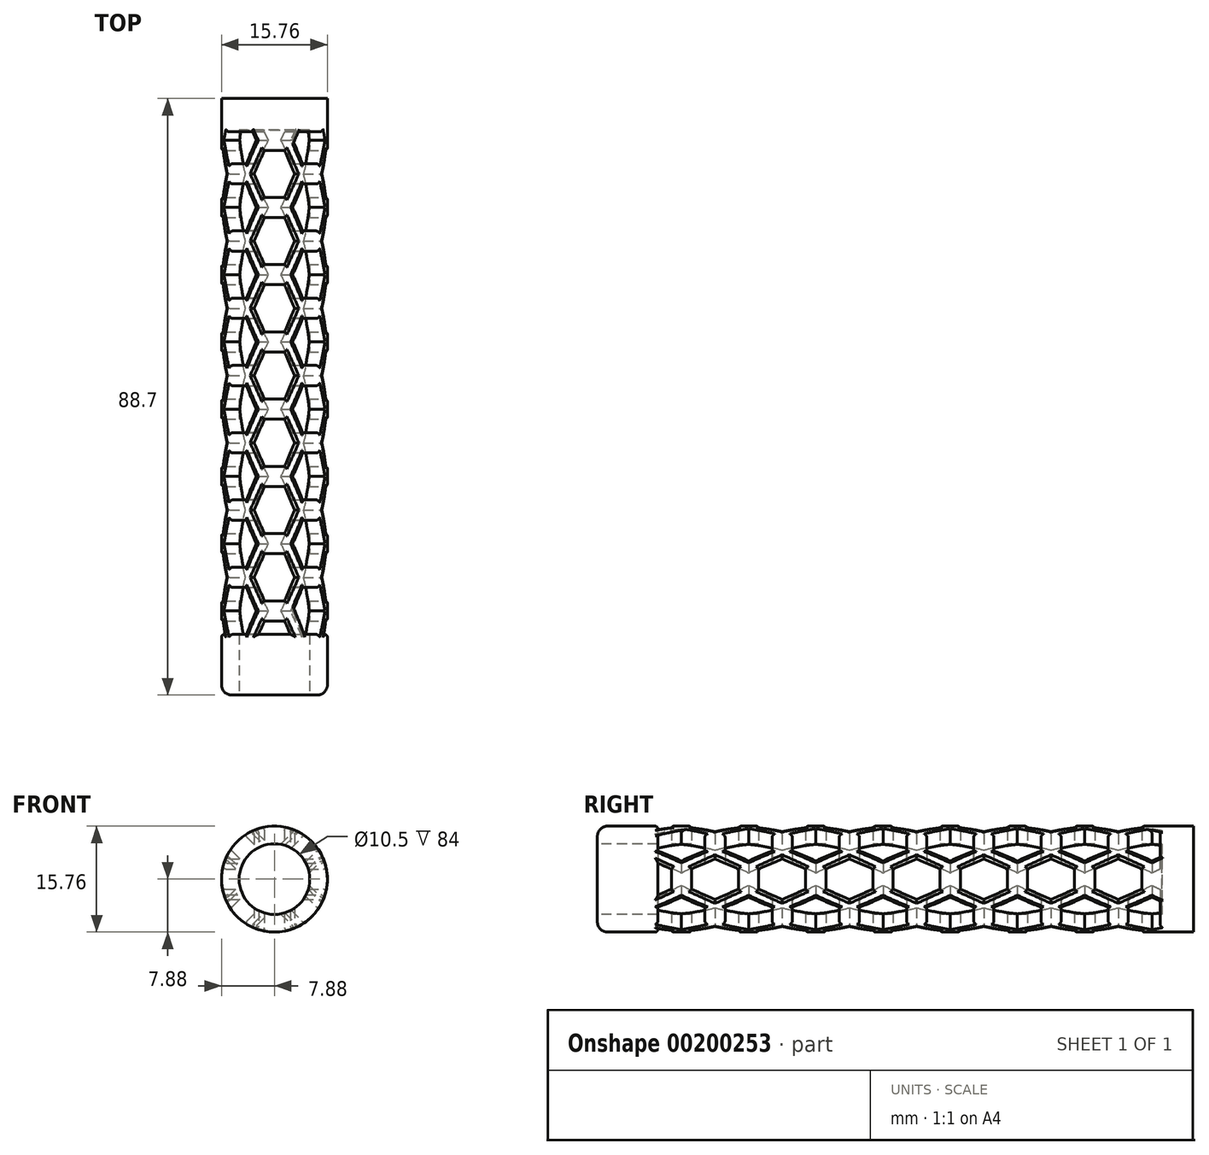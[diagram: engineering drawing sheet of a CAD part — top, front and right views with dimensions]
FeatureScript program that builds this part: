
annotation { "Feature Type Name" : "Feature", "Feature Type Description" : "" }
export const myFeature = defineFeature(function(context is Context, id is Id, definition is map)
    precondition{}
    {
        {
            var Q0;
            Q0=qCreatedBy(makeId("Front.planeOp"),FACE);
            var sketch = newSketch(context, id + "F0", { "sketchPlane" : qUnion([Q0])});
            skCircle(sketch, "E0", {"center": v(0, 0) * mm, "radius": 7.88 * mm});
            skSolve(sketch);
        }
        {
            var Q0;
            Q0=makeQuery(id+"F0.imprint","IMPRINT",FACE,{"disambiguationData":[TD([[makeQuery(id+"F0.imprint","IMPRINT",EDGE,{"derivedFrom":sQuery(id+"F0.wireOp",EDGE,"E0")}),1.0]])]});
            extrude(context, id + "F1", {"entities" : qUnion([Q0]), "oppositeDirection" : true, "depth" : 88.7 * mm});
        }
        {
            var Q0;
            Q0=makeQuery(id+"F1.opExtrude","CAP_FACE",FACE,{"disambiguationData":[OSD([sQuery(id+"F0.wireOp",EDGE,"E0")])],"isStart":true});
            var sketch = newSketch(context, id + "F2", { "sketchPlane" : qUnion([Q0])});
            skCircle(sketch, "E1", {"center": v(0, 0) * mm, "radius": 5.25 * mm});
            skSolve(sketch);
        }
        {
            var Q0;
            Q0=qSketchRegion(id+"F2",true);
            extrude(context, id + "F3", {"entities" : qUnion([Q0]), "operationType" : NewBodyOperationType.REMOVE, "oppositeDirection" : true, "depth" : 84 * mm});
        }
        {
            var Q0;
            Q0=qCreatedBy(makeId("Top.planeOp"),FACE);
            var sketch = newSketch(context, id + "F4", { "sketchPlane" : qUnion([Q0])});
            skLineSegment(sketch, "E2", {"start": v(0, 0) * mm, "end": v(0, 9) * mm, "construction": true});
            skLineSegment(sketch, "E3", {"start": v(0, 9) * mm, "end": v(-3, 9) * mm, "construction": true});
            skLineSegment(sketch, "E4", {"start": v(3, 9) * mm, "end": v(1.5, 9) * mm, "construction": true});
            skLineSegment(sketch, "E5", {"start": v(1.5, 9) * mm, "end": v(-1.5, 9) * mm, "construction": true});
            skLineSegment(sketch, "E6", {"start": v(-1.5, 9) * mm, "end": v(-3, 9) * mm, "construction": true});
            skLineSegment(sketch, "E7", {"start": v(-3, 9) * mm, "end": v(-3, 12.5) * mm, "construction": true});
            skLineSegment(sketch, "E8", {"start": v(-3, 12.5) * mm, "end": v(-3, 16) * mm, "construction": true});
            skLineSegment(sketch, "E9", {"start": v(-3, 16) * mm, "end": v(-1.5, 16) * mm, "construction": true});
            skLineSegment(sketch, "E10", {"start": v(-1.5, 16) * mm, "end": v(1.5, 16) * mm, "construction": true});
            skLineSegment(sketch, "E11", {"start": v(1.5, 16) * mm, "end": v(3, 16) * mm, "construction": true});
            skLineSegment(sketch, "E12", {"start": v(3, 16) * mm, "end": v(3, 12.5) * mm, "construction": true});
            skLineSegment(sketch, "E13", {"start": v(3, 12.5) * mm, "end": v(3, 9) * mm, "construction": true});
            skLineSegment(sketch, "E14", {"start": v(1.5, 16) * mm, "end": v(3, 12.5) * mm});
            skLineSegment(sketch, "E15", {"start": v(3, 12.5) * mm, "end": v(1.5, 9) * mm});
            skLineSegment(sketch, "E16", {"start": v(1.5, 9) * mm, "end": v(-1.5, 9) * mm});
            skLineSegment(sketch, "E17", {"start": v(-1.5, 9) * mm, "end": v(-3, 12.5) * mm});
            skLineSegment(sketch, "E18", {"start": v(-3, 12.5) * mm, "end": v(-1.5, 16) * mm});
            skLineSegment(sketch, "E19", {"start": v(-1.5, 16) * mm, "end": v(1.5, 16) * mm});
            skLineSegment(sketch, "E20", {"start": v(0, 9) * mm, "end": v(0, 19) * mm, "construction": true});
            skLineSegment(sketch, "E21", {"start": v(0, 19) * mm, "end": v(-3, 19) * mm, "construction": true});
            skLineSegment(sketch, "E22", {"start": v(3, 19) * mm, "end": v(1.5, 19) * mm, "construction": true});
            skLineSegment(sketch, "E23", {"start": v(1.5, 19) * mm, "end": v(-1.5, 19) * mm, "construction": true});
            skLineSegment(sketch, "E24", {"start": v(-1.5, 19) * mm, "end": v(-3, 19) * mm, "construction": true});
            skLineSegment(sketch, "E25", {"start": v(-3, 19) * mm, "end": v(-3, 22.5) * mm, "construction": true});
            skLineSegment(sketch, "E26", {"start": v(-3, 22.5) * mm, "end": v(-3, 26) * mm, "construction": true});
            skLineSegment(sketch, "E27", {"start": v(-3, 26) * mm, "end": v(-1.5, 26) * mm, "construction": true});
            skLineSegment(sketch, "E28", {"start": v(-1.5, 26) * mm, "end": v(1.5, 26) * mm, "construction": true});
            skLineSegment(sketch, "E29", {"start": v(1.5, 26) * mm, "end": v(3, 26) * mm, "construction": true});
            skLineSegment(sketch, "E30", {"start": v(3, 26) * mm, "end": v(3, 22.5) * mm, "construction": true});
            skLineSegment(sketch, "E31", {"start": v(3, 22.5) * mm, "end": v(3, 19) * mm, "construction": true});
            skLineSegment(sketch, "E32", {"start": v(1.5, 26) * mm, "end": v(3, 22.5) * mm});
            skLineSegment(sketch, "E33", {"start": v(3, 22.5) * mm, "end": v(1.5, 19) * mm});
            skLineSegment(sketch, "E34", {"start": v(1.5, 19) * mm, "end": v(-1.5, 19) * mm});
            skLineSegment(sketch, "E35", {"start": v(-1.5, 19) * mm, "end": v(-3, 22.5) * mm});
            skLineSegment(sketch, "E36", {"start": v(-3, 22.5) * mm, "end": v(-1.5, 26) * mm});
            skLineSegment(sketch, "E37", {"start": v(-1.5, 26) * mm, "end": v(1.5, 26) * mm});
            skLineSegment(sketch, "E38", {"start": v(0, 19) * mm, "end": v(0, 29) * mm, "construction": true});
            skLineSegment(sketch, "E39", {"start": v(0, 29) * mm, "end": v(-3, 29) * mm, "construction": true});
            skLineSegment(sketch, "E40", {"start": v(3, 29) * mm, "end": v(1.5, 29) * mm, "construction": true});
            skLineSegment(sketch, "E41", {"start": v(1.5, 29) * mm, "end": v(-1.5, 29) * mm, "construction": true});
            skLineSegment(sketch, "E42", {"start": v(-1.5, 29) * mm, "end": v(-3, 29) * mm, "construction": true});
            skLineSegment(sketch, "E43", {"start": v(-3, 29) * mm, "end": v(-3, 32.5) * mm, "construction": true});
            skLineSegment(sketch, "E44", {"start": v(-3, 32.5) * mm, "end": v(-3, 36) * mm, "construction": true});
            skLineSegment(sketch, "E45", {"start": v(-3, 36) * mm, "end": v(-1.5, 36) * mm, "construction": true});
            skLineSegment(sketch, "E46", {"start": v(-1.5, 36) * mm, "end": v(1.5, 36) * mm, "construction": true});
            skLineSegment(sketch, "E47", {"start": v(1.5, 36) * mm, "end": v(3, 36) * mm, "construction": true});
            skLineSegment(sketch, "E48", {"start": v(3, 36) * mm, "end": v(3, 32.5) * mm, "construction": true});
            skLineSegment(sketch, "E49", {"start": v(3, 32.5) * mm, "end": v(3, 29) * mm, "construction": true});
            skLineSegment(sketch, "E50", {"start": v(1.5, 36) * mm, "end": v(3, 32.5) * mm});
            skLineSegment(sketch, "E51", {"start": v(3, 32.5) * mm, "end": v(1.5, 29) * mm});
            skLineSegment(sketch, "E52", {"start": v(1.5, 29) * mm, "end": v(-1.5, 29) * mm});
            skLineSegment(sketch, "E53", {"start": v(-1.5, 29) * mm, "end": v(-3, 32.5) * mm});
            skLineSegment(sketch, "E54", {"start": v(-3, 32.5) * mm, "end": v(-1.5, 36) * mm});
            skLineSegment(sketch, "E55", {"start": v(-1.5, 36) * mm, "end": v(1.5, 36) * mm});
            skLineSegment(sketch, "E56", {"start": v(0, 29) * mm, "end": v(0, 39) * mm, "construction": true});
            skLineSegment(sketch, "E57", {"start": v(0, 39) * mm, "end": v(-3, 39) * mm, "construction": true});
            skLineSegment(sketch, "E58", {"start": v(3, 39) * mm, "end": v(1.5, 39) * mm, "construction": true});
            skLineSegment(sketch, "E59", {"start": v(1.5, 39) * mm, "end": v(-1.5, 39) * mm, "construction": true});
            skLineSegment(sketch, "E60", {"start": v(-1.5, 39) * mm, "end": v(-3, 39) * mm, "construction": true});
            skLineSegment(sketch, "E61", {"start": v(-3, 39) * mm, "end": v(-3, 42.5) * mm, "construction": true});
            skLineSegment(sketch, "E62", {"start": v(-3, 42.5) * mm, "end": v(-3, 46) * mm, "construction": true});
            skLineSegment(sketch, "E63", {"start": v(-3, 46) * mm, "end": v(-1.5, 46) * mm, "construction": true});
            skLineSegment(sketch, "E64", {"start": v(-1.5, 46) * mm, "end": v(1.5, 46) * mm, "construction": true});
            skLineSegment(sketch, "E65", {"start": v(1.5, 46) * mm, "end": v(3, 46) * mm, "construction": true});
            skLineSegment(sketch, "E66", {"start": v(3, 46) * mm, "end": v(3, 42.5) * mm, "construction": true});
            skLineSegment(sketch, "E67", {"start": v(3, 42.5) * mm, "end": v(3, 39) * mm, "construction": true});
            skLineSegment(sketch, "E68", {"start": v(1.5, 46) * mm, "end": v(3, 42.5) * mm});
            skLineSegment(sketch, "E69", {"start": v(3, 42.5) * mm, "end": v(1.5, 39) * mm});
            skLineSegment(sketch, "E70", {"start": v(1.5, 39) * mm, "end": v(-1.5, 39) * mm});
            skLineSegment(sketch, "E71", {"start": v(-1.5, 39) * mm, "end": v(-3, 42.5) * mm});
            skLineSegment(sketch, "E72", {"start": v(-3, 42.5) * mm, "end": v(-1.5, 46) * mm});
            skLineSegment(sketch, "E73", {"start": v(-1.5, 46) * mm, "end": v(1.5, 46) * mm});
            skLineSegment(sketch, "E74", {"start": v(0, 39) * mm, "end": v(0, 49) * mm, "construction": true});
            skLineSegment(sketch, "E75", {"start": v(0, 49) * mm, "end": v(-3, 49) * mm, "construction": true});
            skLineSegment(sketch, "E76", {"start": v(3, 49) * mm, "end": v(1.5, 49) * mm, "construction": true});
            skLineSegment(sketch, "E77", {"start": v(1.5, 49) * mm, "end": v(-1.5, 49) * mm, "construction": true});
            skLineSegment(sketch, "E78", {"start": v(-1.5, 49) * mm, "end": v(-3, 49) * mm, "construction": true});
            skLineSegment(sketch, "E79", {"start": v(-3, 49) * mm, "end": v(-3, 52.5) * mm, "construction": true});
            skLineSegment(sketch, "E80", {"start": v(-3, 52.5) * mm, "end": v(-3, 56) * mm, "construction": true});
            skLineSegment(sketch, "E81", {"start": v(-3, 56) * mm, "end": v(-1.5, 56) * mm, "construction": true});
            skLineSegment(sketch, "E82", {"start": v(-1.5, 56) * mm, "end": v(1.5, 56) * mm, "construction": true});
            skLineSegment(sketch, "E83", {"start": v(1.5, 56) * mm, "end": v(3, 56) * mm, "construction": true});
            skLineSegment(sketch, "E84", {"start": v(3, 56) * mm, "end": v(3, 52.5) * mm, "construction": true});
            skLineSegment(sketch, "E85", {"start": v(3, 52.5) * mm, "end": v(3, 49) * mm, "construction": true});
            skLineSegment(sketch, "E86", {"start": v(1.5, 56) * mm, "end": v(3, 52.5) * mm});
            skLineSegment(sketch, "E87", {"start": v(3, 52.5) * mm, "end": v(1.5, 49) * mm});
            skLineSegment(sketch, "E88", {"start": v(1.5, 49) * mm, "end": v(-1.5, 49) * mm});
            skLineSegment(sketch, "E89", {"start": v(-1.5, 49) * mm, "end": v(-3, 52.5) * mm});
            skLineSegment(sketch, "E90", {"start": v(-3, 52.5) * mm, "end": v(-1.5, 56) * mm});
            skLineSegment(sketch, "E91", {"start": v(-1.5, 56) * mm, "end": v(1.5, 56) * mm});
            skLineSegment(sketch, "E92", {"start": v(0, 49) * mm, "end": v(0, 59) * mm, "construction": true});
            skLineSegment(sketch, "E93", {"start": v(0, 59) * mm, "end": v(-3, 59) * mm, "construction": true});
            skLineSegment(sketch, "E94", {"start": v(3, 59) * mm, "end": v(1.5, 59) * mm, "construction": true});
            skLineSegment(sketch, "E95", {"start": v(1.5, 59) * mm, "end": v(-1.5, 59) * mm, "construction": true});
            skLineSegment(sketch, "E96", {"start": v(-1.5, 59) * mm, "end": v(-3, 59) * mm, "construction": true});
            skLineSegment(sketch, "E97", {"start": v(-3, 59) * mm, "end": v(-3, 62.5) * mm, "construction": true});
            skLineSegment(sketch, "E98", {"start": v(-3, 62.5) * mm, "end": v(-3, 66) * mm, "construction": true});
            skLineSegment(sketch, "E99", {"start": v(-3, 66) * mm, "end": v(-1.5, 66) * mm, "construction": true});
            skLineSegment(sketch, "E100", {"start": v(-1.5, 66) * mm, "end": v(1.5, 66) * mm, "construction": true});
            skLineSegment(sketch, "E101", {"start": v(1.5, 66) * mm, "end": v(3, 66) * mm, "construction": true});
            skLineSegment(sketch, "E102", {"start": v(3, 66) * mm, "end": v(3, 62.5) * mm, "construction": true});
            skLineSegment(sketch, "E103", {"start": v(3, 62.5) * mm, "end": v(3, 59) * mm, "construction": true});
            skLineSegment(sketch, "E104", {"start": v(1.5, 66) * mm, "end": v(3, 62.5) * mm});
            skLineSegment(sketch, "E105", {"start": v(3, 62.5) * mm, "end": v(1.5, 59) * mm});
            skLineSegment(sketch, "E106", {"start": v(1.5, 59) * mm, "end": v(-1.5, 59) * mm});
            skLineSegment(sketch, "E107", {"start": v(-1.5, 59) * mm, "end": v(-3, 62.5) * mm});
            skLineSegment(sketch, "E108", {"start": v(-3, 62.5) * mm, "end": v(-1.5, 66) * mm});
            skLineSegment(sketch, "E109", {"start": v(-1.5, 66) * mm, "end": v(1.5, 66) * mm});
            skLineSegment(sketch, "E110", {"start": v(0, 59) * mm, "end": v(0, 69) * mm, "construction": true});
            skLineSegment(sketch, "E111", {"start": v(0, 69) * mm, "end": v(-3, 69) * mm, "construction": true});
            skLineSegment(sketch, "E112", {"start": v(3, 69) * mm, "end": v(1.5, 69) * mm, "construction": true});
            skLineSegment(sketch, "E113", {"start": v(1.5, 69) * mm, "end": v(-1.5, 69) * mm, "construction": true});
            skLineSegment(sketch, "E114", {"start": v(-1.5, 69) * mm, "end": v(-3, 69) * mm, "construction": true});
            skLineSegment(sketch, "E115", {"start": v(-3, 69) * mm, "end": v(-3, 72.5) * mm, "construction": true});
            skLineSegment(sketch, "E116", {"start": v(-3, 72.5) * mm, "end": v(-3, 76) * mm, "construction": true});
            skLineSegment(sketch, "E117", {"start": v(-3, 76) * mm, "end": v(-1.5, 76) * mm, "construction": true});
            skLineSegment(sketch, "E118", {"start": v(-1.5, 76) * mm, "end": v(1.5, 76) * mm, "construction": true});
            skLineSegment(sketch, "E119", {"start": v(1.5, 76) * mm, "end": v(3, 76) * mm, "construction": true});
            skLineSegment(sketch, "E120", {"start": v(3, 76) * mm, "end": v(3, 72.5) * mm, "construction": true});
            skLineSegment(sketch, "E121", {"start": v(3, 72.5) * mm, "end": v(3, 69) * mm, "construction": true});
            skLineSegment(sketch, "E122", {"start": v(1.5, 76) * mm, "end": v(3, 72.5) * mm});
            skLineSegment(sketch, "E123", {"start": v(3, 72.5) * mm, "end": v(1.5, 69) * mm});
            skLineSegment(sketch, "E124", {"start": v(1.5, 69) * mm, "end": v(-1.5, 69) * mm});
            skLineSegment(sketch, "E125", {"start": v(-1.5, 69) * mm, "end": v(-3, 72.5) * mm});
            skLineSegment(sketch, "E126", {"start": v(-3, 72.5) * mm, "end": v(-1.5, 76) * mm});
            skLineSegment(sketch, "E127", {"start": v(-1.5, 76) * mm, "end": v(1.5, 76) * mm});
            skLineSegment(sketch, "E128", {"start": v(0, 69) * mm, "end": v(0, 79) * mm, "construction": true});
            skLineSegment(sketch, "E129", {"start": v(0, 79) * mm, "end": v(-3, 79) * mm, "construction": true});
            skLineSegment(sketch, "E130", {"start": v(3, 79) * mm, "end": v(1.5, 79) * mm, "construction": true});
            skLineSegment(sketch, "E131", {"start": v(1.5, 79) * mm, "end": v(-1.5, 79) * mm, "construction": true});
            skLineSegment(sketch, "E132", {"start": v(-1.5, 79) * mm, "end": v(-3, 79) * mm, "construction": true});
            skLineSegment(sketch, "E133", {"start": v(-3, 79) * mm, "end": v(-3, 82.5) * mm, "construction": true});
            skLineSegment(sketch, "E134", {"start": v(3, 82.5) * mm, "end": v(3, 79) * mm, "construction": true});
            skLineSegment(sketch, "E135", {"start": v(3, 82.5) * mm, "end": v(1.5, 79) * mm});
            skLineSegment(sketch, "E136", {"start": v(1.5, 79) * mm, "end": v(-1.5, 79) * mm});
            skLineSegment(sketch, "E137", {"start": v(-1.5, 79) * mm, "end": v(-3, 82.5) * mm});
            skLineSegment(sketch, "E138", {"start": v(0, 79) * mm, "end": v(0, 83.75) * mm, "construction": true});
            skLineSegment(sketch, "E139", {"start": v(0, 83.75) * mm, "end": v(-2.46, 83.75) * mm});
            skLineSegment(sketch, "E140", {"start": v(0, 83.75) * mm, "end": v(2.46, 83.75) * mm});
            skLineSegment(sketch, "E141", {"start": v(-2.46, 83.75) * mm, "end": v(-3, 82.5) * mm});
            skLineSegment(sketch, "E142", {"start": v(2.46, 83.75) * mm, "end": v(3, 82.5) * mm});
            skSolve(sketch);
        }
        {
            var Q0;
            Q0=qSketchRegion(id+"F4",true);
            extrude(context, id + "F5", {"entities" : qUnion([Q0]), "operationType" : NewBodyOperationType.REMOVE, "endBound" : BoundingType.SYMMETRIC, "depth" : 25 * mm});
        }
        {
            var Q0;
            Q0=qCreatedBy(makeId("Right.planeOp"),FACE);
            var sketch = newSketch(context, id + "F6", { "sketchPlane" : qUnion([Q0])});
            skLineSegment(sketch, "E143", {"start": v(0, 0) * mm, "end": v(9, 0) * mm, "construction": true});
            skLineSegment(sketch, "E144", {"start": v(9, 0) * mm, "end": v(9, 3) * mm, "construction": true});
            skLineSegment(sketch, "E145", {"start": v(9, -3) * mm, "end": v(9, -1.5) * mm, "construction": true});
            skLineSegment(sketch, "E146", {"start": v(9, -1.5) * mm, "end": v(9, 1.5) * mm, "construction": true});
            skLineSegment(sketch, "E147", {"start": v(9, 1.5) * mm, "end": v(9, 3) * mm, "construction": true});
            skLineSegment(sketch, "E148", {"start": v(9, 3) * mm, "end": v(12.5, 3) * mm, "construction": true});
            skLineSegment(sketch, "E149", {"start": v(12.5, 3) * mm, "end": v(16, 3) * mm, "construction": true});
            skLineSegment(sketch, "E150", {"start": v(16, 3) * mm, "end": v(16, 1.5) * mm, "construction": true});
            skLineSegment(sketch, "E151", {"start": v(16, 1.5) * mm, "end": v(16, -1.5) * mm, "construction": true});
            skLineSegment(sketch, "E152", {"start": v(16, -1.5) * mm, "end": v(16, -3) * mm, "construction": true});
            skLineSegment(sketch, "E153", {"start": v(16, -3) * mm, "end": v(12.5, -3) * mm, "construction": true});
            skLineSegment(sketch, "E154", {"start": v(12.5, -3) * mm, "end": v(9, -3) * mm, "construction": true});
            skLineSegment(sketch, "E155", {"start": v(16, -1.5) * mm, "end": v(12.5, -3) * mm});
            skLineSegment(sketch, "E156", {"start": v(12.5, -3) * mm, "end": v(9, -1.5) * mm});
            skLineSegment(sketch, "E157", {"start": v(9, -1.5) * mm, "end": v(9, 1.5) * mm});
            skLineSegment(sketch, "E158", {"start": v(9, 1.5) * mm, "end": v(12.5, 3) * mm});
            skLineSegment(sketch, "E159", {"start": v(12.5, 3) * mm, "end": v(16, 1.5) * mm});
            skLineSegment(sketch, "E160", {"start": v(16, 1.5) * mm, "end": v(16, -1.5) * mm});
            skLineSegment(sketch, "E161", {"start": v(9, 0) * mm, "end": v(19, 0) * mm, "construction": true});
            skLineSegment(sketch, "E162", {"start": v(19, 0) * mm, "end": v(19, 3) * mm, "construction": true});
            skLineSegment(sketch, "E163", {"start": v(19, -3) * mm, "end": v(19, -1.5) * mm, "construction": true});
            skLineSegment(sketch, "E164", {"start": v(19, -1.5) * mm, "end": v(19, 1.5) * mm, "construction": true});
            skLineSegment(sketch, "E165", {"start": v(19, 1.5) * mm, "end": v(19, 3) * mm, "construction": true});
            skLineSegment(sketch, "E166", {"start": v(19, 3) * mm, "end": v(22.5, 3) * mm, "construction": true});
            skLineSegment(sketch, "E167", {"start": v(22.5, 3) * mm, "end": v(26, 3) * mm, "construction": true});
            skLineSegment(sketch, "E168", {"start": v(26, 3) * mm, "end": v(26, 1.5) * mm, "construction": true});
            skLineSegment(sketch, "E169", {"start": v(26, 1.5) * mm, "end": v(26, -1.5) * mm, "construction": true});
            skLineSegment(sketch, "E170", {"start": v(26, -1.5) * mm, "end": v(26, -3) * mm, "construction": true});
            skLineSegment(sketch, "E171", {"start": v(26, -3) * mm, "end": v(22.5, -3) * mm, "construction": true});
            skLineSegment(sketch, "E172", {"start": v(22.5, -3) * mm, "end": v(19, -3) * mm, "construction": true});
            skLineSegment(sketch, "E173", {"start": v(26, -1.5) * mm, "end": v(22.5, -3) * mm});
            skLineSegment(sketch, "E174", {"start": v(22.5, -3) * mm, "end": v(19, -1.5) * mm});
            skLineSegment(sketch, "E175", {"start": v(19, -1.5) * mm, "end": v(19, 1.5) * mm});
            skLineSegment(sketch, "E176", {"start": v(19, 1.5) * mm, "end": v(22.5, 3) * mm});
            skLineSegment(sketch, "E177", {"start": v(22.5, 3) * mm, "end": v(26, 1.5) * mm});
            skLineSegment(sketch, "E178", {"start": v(26, 1.5) * mm, "end": v(26, -1.5) * mm});
            skLineSegment(sketch, "E179", {"start": v(19, 0) * mm, "end": v(29, 0) * mm, "construction": true});
            skLineSegment(sketch, "E180", {"start": v(29, 0) * mm, "end": v(29, 3) * mm, "construction": true});
            skLineSegment(sketch, "E181", {"start": v(29, -3) * mm, "end": v(29, -1.5) * mm, "construction": true});
            skLineSegment(sketch, "E182", {"start": v(29, -1.5) * mm, "end": v(29, 1.5) * mm, "construction": true});
            skLineSegment(sketch, "E183", {"start": v(29, 1.5) * mm, "end": v(29, 3) * mm, "construction": true});
            skLineSegment(sketch, "E184", {"start": v(29, 3) * mm, "end": v(32.5, 3) * mm, "construction": true});
            skLineSegment(sketch, "E185", {"start": v(32.5, 3) * mm, "end": v(36, 3) * mm, "construction": true});
            skLineSegment(sketch, "E186", {"start": v(36, 3) * mm, "end": v(36, 1.5) * mm, "construction": true});
            skLineSegment(sketch, "E187", {"start": v(36, 1.5) * mm, "end": v(36, -1.5) * mm, "construction": true});
            skLineSegment(sketch, "E188", {"start": v(36, -1.5) * mm, "end": v(36, -3) * mm, "construction": true});
            skLineSegment(sketch, "E189", {"start": v(36, -3) * mm, "end": v(32.5, -3) * mm, "construction": true});
            skLineSegment(sketch, "E190", {"start": v(32.5, -3) * mm, "end": v(29, -3) * mm, "construction": true});
            skLineSegment(sketch, "E191", {"start": v(36, -1.5) * mm, "end": v(32.5, -3) * mm});
            skLineSegment(sketch, "E192", {"start": v(32.5, -3) * mm, "end": v(29, -1.5) * mm});
            skLineSegment(sketch, "E193", {"start": v(29, -1.5) * mm, "end": v(29, 1.5) * mm});
            skLineSegment(sketch, "E194", {"start": v(29, 1.5) * mm, "end": v(32.5, 3) * mm});
            skLineSegment(sketch, "E195", {"start": v(32.5, 3) * mm, "end": v(36, 1.5) * mm});
            skLineSegment(sketch, "E196", {"start": v(36, 1.5) * mm, "end": v(36, -1.5) * mm});
            skLineSegment(sketch, "E197", {"start": v(29, 0) * mm, "end": v(39, 0) * mm, "construction": true});
            skLineSegment(sketch, "E198", {"start": v(39, 0) * mm, "end": v(39, 3) * mm, "construction": true});
            skLineSegment(sketch, "E199", {"start": v(39, -3) * mm, "end": v(39, -1.5) * mm, "construction": true});
            skLineSegment(sketch, "E200", {"start": v(39, -1.5) * mm, "end": v(39, 1.5) * mm, "construction": true});
            skLineSegment(sketch, "E201", {"start": v(39, 1.5) * mm, "end": v(39, 3) * mm, "construction": true});
            skLineSegment(sketch, "E202", {"start": v(39, 3) * mm, "end": v(42.5, 3) * mm, "construction": true});
            skLineSegment(sketch, "E203", {"start": v(42.5, 3) * mm, "end": v(46, 3) * mm, "construction": true});
            skLineSegment(sketch, "E204", {"start": v(46, 3) * mm, "end": v(46, 1.5) * mm, "construction": true});
            skLineSegment(sketch, "E205", {"start": v(46, 1.5) * mm, "end": v(46, -1.5) * mm, "construction": true});
            skLineSegment(sketch, "E206", {"start": v(46, -1.5) * mm, "end": v(46, -3) * mm, "construction": true});
            skLineSegment(sketch, "E207", {"start": v(46, -3) * mm, "end": v(42.5, -3) * mm, "construction": true});
            skLineSegment(sketch, "E208", {"start": v(42.5, -3) * mm, "end": v(39, -3) * mm, "construction": true});
            skLineSegment(sketch, "E209", {"start": v(46, -1.5) * mm, "end": v(42.5, -3) * mm});
            skLineSegment(sketch, "E210", {"start": v(42.5, -3) * mm, "end": v(39, -1.5) * mm});
            skLineSegment(sketch, "E211", {"start": v(39, -1.5) * mm, "end": v(39, 1.5) * mm});
            skLineSegment(sketch, "E212", {"start": v(39, 1.5) * mm, "end": v(42.5, 3) * mm});
            skLineSegment(sketch, "E213", {"start": v(42.5, 3) * mm, "end": v(46, 1.5) * mm});
            skLineSegment(sketch, "E214", {"start": v(46, 1.5) * mm, "end": v(46, -1.5) * mm});
            skLineSegment(sketch, "E215", {"start": v(39, 0) * mm, "end": v(49, 0) * mm, "construction": true});
            skLineSegment(sketch, "E216", {"start": v(49, 0) * mm, "end": v(49, 3) * mm, "construction": true});
            skLineSegment(sketch, "E217", {"start": v(49, -3) * mm, "end": v(49, -1.5) * mm, "construction": true});
            skLineSegment(sketch, "E218", {"start": v(49, -1.5) * mm, "end": v(49, 1.5) * mm, "construction": true});
            skLineSegment(sketch, "E219", {"start": v(49, 1.5) * mm, "end": v(49, 3) * mm, "construction": true});
            skLineSegment(sketch, "E220", {"start": v(49, 3) * mm, "end": v(52.5, 3) * mm, "construction": true});
            skLineSegment(sketch, "E221", {"start": v(52.5, 3) * mm, "end": v(56, 3) * mm, "construction": true});
            skLineSegment(sketch, "E222", {"start": v(56, 3) * mm, "end": v(56, 1.5) * mm, "construction": true});
            skLineSegment(sketch, "E223", {"start": v(56, 1.5) * mm, "end": v(56, -1.5) * mm, "construction": true});
            skLineSegment(sketch, "E224", {"start": v(56, -1.5) * mm, "end": v(56, -3) * mm, "construction": true});
            skLineSegment(sketch, "E225", {"start": v(56, -3) * mm, "end": v(52.5, -3) * mm, "construction": true});
            skLineSegment(sketch, "E226", {"start": v(52.5, -3) * mm, "end": v(49, -3) * mm, "construction": true});
            skLineSegment(sketch, "E227", {"start": v(56, -1.5) * mm, "end": v(52.5, -3) * mm});
            skLineSegment(sketch, "E228", {"start": v(52.5, -3) * mm, "end": v(49, -1.5) * mm});
            skLineSegment(sketch, "E229", {"start": v(49, -1.5) * mm, "end": v(49, 1.5) * mm});
            skLineSegment(sketch, "E230", {"start": v(49, 1.5) * mm, "end": v(52.5, 3) * mm});
            skLineSegment(sketch, "E231", {"start": v(52.5, 3) * mm, "end": v(56, 1.5) * mm});
            skLineSegment(sketch, "E232", {"start": v(56, 1.5) * mm, "end": v(56, -1.5) * mm});
            skLineSegment(sketch, "E233", {"start": v(49, 0) * mm, "end": v(59, 0) * mm, "construction": true});
            skLineSegment(sketch, "E234", {"start": v(59, 0) * mm, "end": v(59, 3) * mm, "construction": true});
            skLineSegment(sketch, "E235", {"start": v(59, -3) * mm, "end": v(59, -1.5) * mm, "construction": true});
            skLineSegment(sketch, "E236", {"start": v(59, -1.5) * mm, "end": v(59, 1.5) * mm, "construction": true});
            skLineSegment(sketch, "E237", {"start": v(59, 1.5) * mm, "end": v(59, 3) * mm, "construction": true});
            skLineSegment(sketch, "E238", {"start": v(59, 3) * mm, "end": v(62.5, 3) * mm, "construction": true});
            skLineSegment(sketch, "E239", {"start": v(62.5, 3) * mm, "end": v(66, 3) * mm, "construction": true});
            skLineSegment(sketch, "E240", {"start": v(66, 3) * mm, "end": v(66, 1.5) * mm, "construction": true});
            skLineSegment(sketch, "E241", {"start": v(66, 1.5) * mm, "end": v(66, -1.5) * mm, "construction": true});
            skLineSegment(sketch, "E242", {"start": v(66, -1.5) * mm, "end": v(66, -3) * mm, "construction": true});
            skLineSegment(sketch, "E243", {"start": v(66, -3) * mm, "end": v(62.5, -3) * mm, "construction": true});
            skLineSegment(sketch, "E244", {"start": v(62.5, -3) * mm, "end": v(59, -3) * mm, "construction": true});
            skLineSegment(sketch, "E245", {"start": v(66, -1.5) * mm, "end": v(62.5, -3) * mm});
            skLineSegment(sketch, "E246", {"start": v(62.5, -3) * mm, "end": v(59, -1.5) * mm});
            skLineSegment(sketch, "E247", {"start": v(59, -1.5) * mm, "end": v(59, 1.5) * mm});
            skLineSegment(sketch, "E248", {"start": v(59, 1.5) * mm, "end": v(62.5, 3) * mm});
            skLineSegment(sketch, "E249", {"start": v(62.5, 3) * mm, "end": v(66, 1.5) * mm});
            skLineSegment(sketch, "E250", {"start": v(66, 1.5) * mm, "end": v(66, -1.5) * mm});
            skLineSegment(sketch, "E251", {"start": v(59, 0) * mm, "end": v(69, 0) * mm, "construction": true});
            skLineSegment(sketch, "E252", {"start": v(69, 0) * mm, "end": v(69, 3) * mm, "construction": true});
            skLineSegment(sketch, "E253", {"start": v(69, -3) * mm, "end": v(69, -1.5) * mm, "construction": true});
            skLineSegment(sketch, "E254", {"start": v(69, -1.5) * mm, "end": v(69, 1.5) * mm, "construction": true});
            skLineSegment(sketch, "E255", {"start": v(69, 1.5) * mm, "end": v(69, 3) * mm, "construction": true});
            skLineSegment(sketch, "E256", {"start": v(69, 3) * mm, "end": v(72.5, 3) * mm, "construction": true});
            skLineSegment(sketch, "E257", {"start": v(72.5, 3) * mm, "end": v(76, 3) * mm, "construction": true});
            skLineSegment(sketch, "E258", {"start": v(76, 3) * mm, "end": v(76, 1.5) * mm, "construction": true});
            skLineSegment(sketch, "E259", {"start": v(76, 1.5) * mm, "end": v(76, -1.5) * mm, "construction": true});
            skLineSegment(sketch, "E260", {"start": v(76, -1.5) * mm, "end": v(76, -3) * mm, "construction": true});
            skLineSegment(sketch, "E261", {"start": v(76, -3) * mm, "end": v(72.5, -3) * mm, "construction": true});
            skLineSegment(sketch, "E262", {"start": v(72.5, -3) * mm, "end": v(69, -3) * mm, "construction": true});
            skLineSegment(sketch, "E263", {"start": v(76, -1.5) * mm, "end": v(72.5, -3) * mm});
            skLineSegment(sketch, "E264", {"start": v(72.5, -3) * mm, "end": v(69, -1.5) * mm});
            skLineSegment(sketch, "E265", {"start": v(69, -1.5) * mm, "end": v(69, 1.5) * mm});
            skLineSegment(sketch, "E266", {"start": v(69, 1.5) * mm, "end": v(72.5, 3) * mm});
            skLineSegment(sketch, "E267", {"start": v(72.5, 3) * mm, "end": v(76, 1.5) * mm});
            skLineSegment(sketch, "E268", {"start": v(76, 1.5) * mm, "end": v(76, -1.5) * mm});
            skLineSegment(sketch, "E269", {"start": v(69, 0) * mm, "end": v(79, 0) * mm, "construction": true});
            skLineSegment(sketch, "E270", {"start": v(79, 0) * mm, "end": v(79, 3) * mm, "construction": true});
            skLineSegment(sketch, "E271", {"start": v(79, -3) * mm, "end": v(79, -1.5) * mm, "construction": true});
            skLineSegment(sketch, "E272", {"start": v(79, -1.5) * mm, "end": v(79, 1.5) * mm, "construction": true});
            skLineSegment(sketch, "E273", {"start": v(79, 1.5) * mm, "end": v(79, 3) * mm, "construction": true});
            skLineSegment(sketch, "E274", {"start": v(79, 3) * mm, "end": v(82.5, 3) * mm, "construction": true});
            skLineSegment(sketch, "E275", {"start": v(82.5, -3) * mm, "end": v(79, -3) * mm, "construction": true});
            skLineSegment(sketch, "E276", {"start": v(82.5, -3) * mm, "end": v(79, -1.5) * mm});
            skLineSegment(sketch, "E277", {"start": v(79, -1.5) * mm, "end": v(79, 1.5) * mm});
            skLineSegment(sketch, "E278", {"start": v(79, 1.5) * mm, "end": v(82.5, 3) * mm});
            skLineSegment(sketch, "E279", {"start": v(79, 0) * mm, "end": v(83.75, 0) * mm, "construction": true});
            skLineSegment(sketch, "E280", {"start": v(83.75, 0) * mm, "end": v(83.75, -2.46) * mm});
            skLineSegment(sketch, "E281", {"start": v(83.75, 0) * mm, "end": v(83.75, 2.46) * mm});
            skLineSegment(sketch, "E282", {"start": v(83.75, -2.46) * mm, "end": v(82.5, -3) * mm});
            skLineSegment(sketch, "E283", {"start": v(83.75, 2.46) * mm, "end": v(82.5, 3) * mm});
            skSolve(sketch);
        }
        {
            var Q0;
            Q0=qSketchRegion(id+"F6",true);
            extrude(context, id + "F7", {"entities" : qUnion([Q0]), "operationType" : NewBodyOperationType.REMOVE, "endBound" : BoundingType.SYMMETRIC, "oppositeDirection" : true, "depth" : 25 * mm});
        }
        {
            var Q0;
            Q0=makeQuery(id+"F1.opExtrude","SWEPT_BODY",BODY,{"disambiguationData":[OSD([sQuery(id+"F0.wireOp",EDGE,"E0")])]});
            var Q1;
            Q1=makeQuery(id+"F1.opExtrude","SWEPT_FACE",FACE,{"disambiguationData":[OSD([sQuery(id+"F0.wireOp",EDGE,"E0")])]});
            transform(context, id + "F8", {"entities" : qUnion([Q0]), "transformType" : TransformType.ROTATION, "transformAxis" : qUnion([Q1]), "angle" : 45 * degree, "makeCopy" : false});
        }
        {
            var Q0;
            Q0=qCreatedBy(makeId("Top.planeOp"),FACE);
            var sketch = newSketch(context, id + "F9", { "sketchPlane" : qUnion([Q0])});
            skLineSegment(sketch, "E284", {"start": v(0, 0) * mm, "end": v(0, 4) * mm, "construction": true});
            skLineSegment(sketch, "E285", {"start": v(-3, 7.5) * mm, "end": v(-3, 11) * mm, "construction": true});
            skLineSegment(sketch, "E286", {"start": v(-3, 11) * mm, "end": v(-1.5, 11) * mm, "construction": true});
            skLineSegment(sketch, "E287", {"start": v(-1.5, 11) * mm, "end": v(1.5, 11) * mm, "construction": true});
            skLineSegment(sketch, "E288", {"start": v(1.5, 11) * mm, "end": v(3, 11) * mm, "construction": true});
            skLineSegment(sketch, "E289", {"start": v(3, 11) * mm, "end": v(3, 7.5) * mm, "construction": true});
            skLineSegment(sketch, "E290", {"start": v(-1.5, 11) * mm, "end": v(1.5, 11) * mm});
            skLineSegment(sketch, "E291", {"start": v(0, 4) * mm, "end": v(0, 14) * mm, "construction": true});
            skPoint(sketch, "E291.endSnap0", {"position": v(0, 11) * mm});
            skLineSegment(sketch, "E292", {"start": v(0, 14) * mm, "end": v(-3, 14) * mm, "construction": true});
            skLineSegment(sketch, "E293", {"start": v(3, 14) * mm, "end": v(1.5, 14) * mm, "construction": true});
            skLineSegment(sketch, "E294", {"start": v(1.5, 14) * mm, "end": v(-1.5, 14) * mm, "construction": true});
            skLineSegment(sketch, "E295", {"start": v(-1.5, 14) * mm, "end": v(-3, 14) * mm, "construction": true});
            skLineSegment(sketch, "E296", {"start": v(-3, 14) * mm, "end": v(-3, 17.5) * mm, "construction": true});
            skLineSegment(sketch, "E297", {"start": v(-3, 17.5) * mm, "end": v(-3, 21) * mm, "construction": true});
            skLineSegment(sketch, "E298", {"start": v(-3, 21) * mm, "end": v(-1.5, 21) * mm, "construction": true});
            skLineSegment(sketch, "E299", {"start": v(-1.5, 21) * mm, "end": v(1.5, 21) * mm, "construction": true});
            skLineSegment(sketch, "E300", {"start": v(1.5, 21) * mm, "end": v(3, 21) * mm, "construction": true});
            skLineSegment(sketch, "E301", {"start": v(3, 21) * mm, "end": v(3, 17.5) * mm, "construction": true});
            skLineSegment(sketch, "E302", {"start": v(3, 17.5) * mm, "end": v(3, 14) * mm, "construction": true});
            skLineSegment(sketch, "E303", {"start": v(1.5, 21) * mm, "end": v(3, 17.5) * mm});
            skLineSegment(sketch, "E304", {"start": v(3, 17.5) * mm, "end": v(1.5, 14) * mm});
            skLineSegment(sketch, "E305", {"start": v(1.5, 14) * mm, "end": v(-1.5, 14) * mm});
            skLineSegment(sketch, "E306", {"start": v(-1.5, 14) * mm, "end": v(-3, 17.5) * mm});
            skLineSegment(sketch, "E307", {"start": v(-3, 17.5) * mm, "end": v(-1.5, 21) * mm});
            skLineSegment(sketch, "E308", {"start": v(-1.5, 21) * mm, "end": v(1.5, 21) * mm});
            skLineSegment(sketch, "E309", {"start": v(0, 14) * mm, "end": v(0, 24) * mm, "construction": true});
            skLineSegment(sketch, "E310", {"start": v(0, 24) * mm, "end": v(-3, 24) * mm, "construction": true});
            skLineSegment(sketch, "E311", {"start": v(3, 24) * mm, "end": v(1.5, 24) * mm, "construction": true});
            skLineSegment(sketch, "E312", {"start": v(1.5, 24) * mm, "end": v(-1.5, 24) * mm, "construction": true});
            skLineSegment(sketch, "E313", {"start": v(-1.5, 24) * mm, "end": v(-3, 24) * mm, "construction": true});
            skLineSegment(sketch, "E314", {"start": v(-3, 24) * mm, "end": v(-3, 27.5) * mm, "construction": true});
            skLineSegment(sketch, "E315", {"start": v(-3, 27.5) * mm, "end": v(-3, 31) * mm, "construction": true});
            skLineSegment(sketch, "E316", {"start": v(-3, 31) * mm, "end": v(-1.5, 31) * mm, "construction": true});
            skLineSegment(sketch, "E317", {"start": v(-1.5, 31) * mm, "end": v(1.5, 31) * mm, "construction": true});
            skLineSegment(sketch, "E318", {"start": v(1.5, 31) * mm, "end": v(3, 31) * mm, "construction": true});
            skLineSegment(sketch, "E319", {"start": v(3, 31) * mm, "end": v(3, 27.5) * mm, "construction": true});
            skLineSegment(sketch, "E320", {"start": v(3, 27.5) * mm, "end": v(3, 24) * mm, "construction": true});
            skLineSegment(sketch, "E321", {"start": v(1.5, 31) * mm, "end": v(3, 27.5) * mm});
            skLineSegment(sketch, "E322", {"start": v(3, 27.5) * mm, "end": v(1.5, 24) * mm});
            skLineSegment(sketch, "E323", {"start": v(1.5, 24) * mm, "end": v(-1.5, 24) * mm});
            skLineSegment(sketch, "E324", {"start": v(-1.5, 24) * mm, "end": v(-3, 27.5) * mm});
            skLineSegment(sketch, "E325", {"start": v(-3, 27.5) * mm, "end": v(-1.5, 31) * mm});
            skLineSegment(sketch, "E326", {"start": v(-1.5, 31) * mm, "end": v(1.5, 31) * mm});
            skLineSegment(sketch, "E327", {"start": v(0, 24) * mm, "end": v(0, 34) * mm, "construction": true});
            skLineSegment(sketch, "E328", {"start": v(0, 34) * mm, "end": v(-3, 34) * mm, "construction": true});
            skLineSegment(sketch, "E329", {"start": v(3, 34) * mm, "end": v(1.5, 34) * mm, "construction": true});
            skLineSegment(sketch, "E330", {"start": v(1.5, 34) * mm, "end": v(-1.5, 34) * mm, "construction": true});
            skLineSegment(sketch, "E331", {"start": v(-1.5, 34) * mm, "end": v(-3, 34) * mm, "construction": true});
            skLineSegment(sketch, "E332", {"start": v(-3, 34) * mm, "end": v(-3, 37.5) * mm, "construction": true});
            skLineSegment(sketch, "E333", {"start": v(-3, 37.5) * mm, "end": v(-3, 41) * mm, "construction": true});
            skLineSegment(sketch, "E334", {"start": v(-3, 41) * mm, "end": v(-1.5, 41) * mm, "construction": true});
            skLineSegment(sketch, "E335", {"start": v(-1.5, 41) * mm, "end": v(1.5, 41) * mm, "construction": true});
            skLineSegment(sketch, "E336", {"start": v(1.5, 41) * mm, "end": v(3, 41) * mm, "construction": true});
            skLineSegment(sketch, "E337", {"start": v(3, 41) * mm, "end": v(3, 37.5) * mm, "construction": true});
            skLineSegment(sketch, "E338", {"start": v(3, 37.5) * mm, "end": v(3, 34) * mm, "construction": true});
            skLineSegment(sketch, "E339", {"start": v(1.5, 41) * mm, "end": v(3, 37.5) * mm});
            skLineSegment(sketch, "E340", {"start": v(3, 37.5) * mm, "end": v(1.5, 34) * mm});
            skLineSegment(sketch, "E341", {"start": v(1.5, 34) * mm, "end": v(-1.5, 34) * mm});
            skLineSegment(sketch, "E342", {"start": v(-1.5, 34) * mm, "end": v(-3, 37.5) * mm});
            skLineSegment(sketch, "E343", {"start": v(-3, 37.5) * mm, "end": v(-1.5, 41) * mm});
            skLineSegment(sketch, "E344", {"start": v(-1.5, 41) * mm, "end": v(1.5, 41) * mm});
            skLineSegment(sketch, "E345", {"start": v(0, 34) * mm, "end": v(0, 44) * mm, "construction": true});
            skLineSegment(sketch, "E346", {"start": v(0, 44) * mm, "end": v(-3, 44) * mm, "construction": true});
            skLineSegment(sketch, "E347", {"start": v(3, 44) * mm, "end": v(1.5, 44) * mm, "construction": true});
            skLineSegment(sketch, "E348", {"start": v(1.5, 44) * mm, "end": v(-1.5, 44) * mm, "construction": true});
            skLineSegment(sketch, "E349", {"start": v(-1.5, 44) * mm, "end": v(-3, 44) * mm, "construction": true});
            skLineSegment(sketch, "E350", {"start": v(-3, 44) * mm, "end": v(-3, 47.5) * mm, "construction": true});
            skLineSegment(sketch, "E351", {"start": v(-3, 47.5) * mm, "end": v(-3, 51) * mm, "construction": true});
            skLineSegment(sketch, "E352", {"start": v(-3, 51) * mm, "end": v(-1.5, 51) * mm, "construction": true});
            skLineSegment(sketch, "E353", {"start": v(-1.5, 51) * mm, "end": v(1.5, 51) * mm, "construction": true});
            skLineSegment(sketch, "E354", {"start": v(1.5, 51) * mm, "end": v(3, 51) * mm, "construction": true});
            skLineSegment(sketch, "E355", {"start": v(3, 51) * mm, "end": v(3, 47.5) * mm, "construction": true});
            skLineSegment(sketch, "E356", {"start": v(3, 47.5) * mm, "end": v(3, 44) * mm, "construction": true});
            skLineSegment(sketch, "E357", {"start": v(1.5, 51) * mm, "end": v(3, 47.5) * mm});
            skLineSegment(sketch, "E358", {"start": v(3, 47.5) * mm, "end": v(1.5, 44) * mm});
            skLineSegment(sketch, "E359", {"start": v(1.5, 44) * mm, "end": v(-1.5, 44) * mm});
            skLineSegment(sketch, "E360", {"start": v(-1.5, 44) * mm, "end": v(-3, 47.5) * mm});
            skLineSegment(sketch, "E361", {"start": v(-3, 47.5) * mm, "end": v(-1.5, 51) * mm});
            skLineSegment(sketch, "E362", {"start": v(-1.5, 51) * mm, "end": v(1.5, 51) * mm});
            skLineSegment(sketch, "E363", {"start": v(0, 44) * mm, "end": v(0, 54) * mm, "construction": true});
            skLineSegment(sketch, "E364", {"start": v(0, 54) * mm, "end": v(-3, 54) * mm, "construction": true});
            skLineSegment(sketch, "E365", {"start": v(3, 54) * mm, "end": v(1.5, 54) * mm, "construction": true});
            skLineSegment(sketch, "E366", {"start": v(1.5, 54) * mm, "end": v(-1.5, 54) * mm, "construction": true});
            skLineSegment(sketch, "E367", {"start": v(-1.5, 54) * mm, "end": v(-3, 54) * mm, "construction": true});
            skLineSegment(sketch, "E368", {"start": v(-3, 54) * mm, "end": v(-3, 57.5) * mm, "construction": true});
            skLineSegment(sketch, "E369", {"start": v(-3, 57.5) * mm, "end": v(-3, 61) * mm, "construction": true});
            skLineSegment(sketch, "E370", {"start": v(-3, 61) * mm, "end": v(-1.5, 61) * mm, "construction": true});
            skLineSegment(sketch, "E371", {"start": v(-1.5, 61) * mm, "end": v(1.5, 61) * mm, "construction": true});
            skLineSegment(sketch, "E372", {"start": v(1.5, 61) * mm, "end": v(3, 61) * mm, "construction": true});
            skLineSegment(sketch, "E373", {"start": v(3, 61) * mm, "end": v(3, 57.5) * mm, "construction": true});
            skLineSegment(sketch, "E374", {"start": v(3, 57.5) * mm, "end": v(3, 54) * mm, "construction": true});
            skLineSegment(sketch, "E375", {"start": v(1.5, 61) * mm, "end": v(3, 57.5) * mm});
            skLineSegment(sketch, "E376", {"start": v(3, 57.5) * mm, "end": v(1.5, 54) * mm});
            skLineSegment(sketch, "E377", {"start": v(1.5, 54) * mm, "end": v(-1.5, 54) * mm});
            skLineSegment(sketch, "E378", {"start": v(-1.5, 54) * mm, "end": v(-3, 57.5) * mm});
            skLineSegment(sketch, "E379", {"start": v(-3, 57.5) * mm, "end": v(-1.5, 61) * mm});
            skLineSegment(sketch, "E380", {"start": v(-1.5, 61) * mm, "end": v(1.5, 61) * mm});
            skLineSegment(sketch, "E381", {"start": v(0, 54) * mm, "end": v(0, 64) * mm, "construction": true});
            skLineSegment(sketch, "E382", {"start": v(0, 64) * mm, "end": v(-3, 64) * mm, "construction": true});
            skLineSegment(sketch, "E383", {"start": v(3, 64) * mm, "end": v(1.5, 64) * mm, "construction": true});
            skLineSegment(sketch, "E384", {"start": v(1.5, 64) * mm, "end": v(-1.5, 64) * mm, "construction": true});
            skLineSegment(sketch, "E385", {"start": v(-1.5, 64) * mm, "end": v(-3, 64) * mm, "construction": true});
            skLineSegment(sketch, "E386", {"start": v(-3, 64) * mm, "end": v(-3, 67.5) * mm, "construction": true});
            skLineSegment(sketch, "E387", {"start": v(-3, 67.5) * mm, "end": v(-3, 71) * mm, "construction": true});
            skLineSegment(sketch, "E388", {"start": v(-3, 71) * mm, "end": v(-1.5, 71) * mm, "construction": true});
            skLineSegment(sketch, "E389", {"start": v(-1.5, 71) * mm, "end": v(1.5, 71) * mm, "construction": true});
            skLineSegment(sketch, "E390", {"start": v(1.5, 71) * mm, "end": v(3, 71) * mm, "construction": true});
            skLineSegment(sketch, "E391", {"start": v(3, 71) * mm, "end": v(3, 67.5) * mm, "construction": true});
            skLineSegment(sketch, "E392", {"start": v(3, 67.5) * mm, "end": v(3, 64) * mm, "construction": true});
            skLineSegment(sketch, "E393", {"start": v(1.5, 71) * mm, "end": v(3, 67.5) * mm});
            skLineSegment(sketch, "E394", {"start": v(3, 67.5) * mm, "end": v(1.5, 64) * mm});
            skLineSegment(sketch, "E395", {"start": v(1.5, 64) * mm, "end": v(-1.5, 64) * mm});
            skLineSegment(sketch, "E396", {"start": v(-1.5, 64) * mm, "end": v(-3, 67.5) * mm});
            skLineSegment(sketch, "E397", {"start": v(-3, 67.5) * mm, "end": v(-1.5, 71) * mm});
            skLineSegment(sketch, "E398", {"start": v(-1.5, 71) * mm, "end": v(1.5, 71) * mm});
            skLineSegment(sketch, "E399", {"start": v(0, 64) * mm, "end": v(0, 74) * mm, "construction": true});
            skLineSegment(sketch, "E400", {"start": v(0, 74) * mm, "end": v(-3, 74) * mm, "construction": true});
            skLineSegment(sketch, "E401", {"start": v(3, 74) * mm, "end": v(1.5, 74) * mm, "construction": true});
            skLineSegment(sketch, "E402", {"start": v(1.5, 74) * mm, "end": v(-1.5, 74) * mm, "construction": true});
            skLineSegment(sketch, "E403", {"start": v(-1.5, 74) * mm, "end": v(-3, 74) * mm, "construction": true});
            skLineSegment(sketch, "E404", {"start": v(-3, 74) * mm, "end": v(-3, 77.5) * mm, "construction": true});
            skLineSegment(sketch, "E405", {"start": v(-3, 77.5) * mm, "end": v(-3, 81) * mm, "construction": true});
            skLineSegment(sketch, "E406", {"start": v(-3, 81) * mm, "end": v(-1.5, 81) * mm, "construction": true});
            skLineSegment(sketch, "E407", {"start": v(-1.5, 81) * mm, "end": v(1.5, 81) * mm, "construction": true});
            skLineSegment(sketch, "E408", {"start": v(1.5, 81) * mm, "end": v(3, 81) * mm, "construction": true});
            skLineSegment(sketch, "E409", {"start": v(3, 81) * mm, "end": v(3, 77.5) * mm, "construction": true});
            skLineSegment(sketch, "E410", {"start": v(3, 77.5) * mm, "end": v(3, 74) * mm, "construction": true});
            skLineSegment(sketch, "E411", {"start": v(1.5, 81) * mm, "end": v(3, 77.5) * mm});
            skLineSegment(sketch, "E412", {"start": v(3, 77.5) * mm, "end": v(1.5, 74) * mm});
            skLineSegment(sketch, "E413", {"start": v(1.5, 74) * mm, "end": v(-1.5, 74) * mm});
            skLineSegment(sketch, "E414", {"start": v(-1.5, 74) * mm, "end": v(-3, 77.5) * mm});
            skLineSegment(sketch, "E415", {"start": v(-3, 77.5) * mm, "end": v(-1.5, 81) * mm});
            skLineSegment(sketch, "E416", {"start": v(-1.5, 81) * mm, "end": v(1.5, 81) * mm});
            skLineSegment(sketch, "E417", {"start": v(1.5, 11) * mm, "end": v(1.5, 9) * mm, "construction": true});
            skLineSegment(sketch, "E418", {"start": v(1.5, 9) * mm, "end": v(2.36, 9) * mm});
            skLineSegment(sketch, "E419", {"start": v(1.5, 9) * mm, "end": v(-2.36, 9) * mm});
            skLineSegment(sketch, "E420", {"start": v(1.5, 11) * mm, "end": v(2.36, 9) * mm});
            skLineSegment(sketch, "E421", {"start": v(-1.5, 11) * mm, "end": v(-2.36, 9) * mm});
            skSolve(sketch);
        }
        {
            var Q0;
            Q0=qSketchRegion(id+"F9",true);
            extrude(context, id + "F10", {"entities" : qUnion([Q0]), "operationType" : NewBodyOperationType.REMOVE, "endBound" : BoundingType.SYMMETRIC, "depth" : 25 * mm});
        }
        {
            var Q0;
            Q0=qCreatedBy(makeId("Right.planeOp"),FACE);
            var sketch = newSketch(context, id + "F11", { "sketchPlane" : qUnion([Q0])});
            skLineSegment(sketch, "E422", {"start": v(0, 0) * mm, "end": v(4, 0) * mm, "construction": true});
            skLineSegment(sketch, "E423", {"start": v(7.5, 3) * mm, "end": v(11, 3) * mm, "construction": true});
            skLineSegment(sketch, "E424", {"start": v(11, 3) * mm, "end": v(11, 1.5) * mm, "construction": true});
            skLineSegment(sketch, "E425", {"start": v(11, 1.5) * mm, "end": v(11, -1.5) * mm, "construction": true});
            skLineSegment(sketch, "E426", {"start": v(11, -1.5) * mm, "end": v(11, -3) * mm, "construction": true});
            skLineSegment(sketch, "E427", {"start": v(11, -3) * mm, "end": v(7.5, -3) * mm, "construction": true});
            skLineSegment(sketch, "E428", {"start": v(11, 1.5) * mm, "end": v(11, -1.5) * mm});
            skLineSegment(sketch, "E429", {"start": v(4, 0) * mm, "end": v(14, 0) * mm, "construction": true});
            skPoint(sketch, "E429.endSnap0", {"position": v(11, 0) * mm});
            skLineSegment(sketch, "E430", {"start": v(14, 0) * mm, "end": v(14, 3) * mm, "construction": true});
            skLineSegment(sketch, "E431", {"start": v(14, -3) * mm, "end": v(14, -1.5) * mm, "construction": true});
            skLineSegment(sketch, "E432", {"start": v(14, -1.5) * mm, "end": v(14, 1.5) * mm, "construction": true});
            skLineSegment(sketch, "E433", {"start": v(14, 1.5) * mm, "end": v(14, 3) * mm, "construction": true});
            skLineSegment(sketch, "E434", {"start": v(14, 3) * mm, "end": v(17.5, 3) * mm, "construction": true});
            skLineSegment(sketch, "E435", {"start": v(17.5, 3) * mm, "end": v(21, 3) * mm, "construction": true});
            skLineSegment(sketch, "E436", {"start": v(21, 3) * mm, "end": v(21, 1.5) * mm, "construction": true});
            skLineSegment(sketch, "E437", {"start": v(21, 1.5) * mm, "end": v(21, -1.5) * mm, "construction": true});
            skLineSegment(sketch, "E438", {"start": v(21, -1.5) * mm, "end": v(21, -3) * mm, "construction": true});
            skLineSegment(sketch, "E439", {"start": v(21, -3) * mm, "end": v(17.5, -3) * mm, "construction": true});
            skLineSegment(sketch, "E440", {"start": v(17.5, -3) * mm, "end": v(14, -3) * mm, "construction": true});
            skLineSegment(sketch, "E441", {"start": v(21, -1.5) * mm, "end": v(17.5, -3) * mm});
            skLineSegment(sketch, "E442", {"start": v(17.5, -3) * mm, "end": v(14, -1.5) * mm});
            skLineSegment(sketch, "E443", {"start": v(14, -1.5) * mm, "end": v(14, 1.5) * mm});
            skLineSegment(sketch, "E444", {"start": v(14, 1.5) * mm, "end": v(17.5, 3) * mm});
            skLineSegment(sketch, "E445", {"start": v(17.5, 3) * mm, "end": v(21, 1.5) * mm});
            skLineSegment(sketch, "E446", {"start": v(21, 1.5) * mm, "end": v(21, -1.5) * mm});
            skLineSegment(sketch, "E447", {"start": v(14, 0) * mm, "end": v(24, 0) * mm, "construction": true});
            skLineSegment(sketch, "E448", {"start": v(24, 0) * mm, "end": v(24, 3) * mm, "construction": true});
            skLineSegment(sketch, "E449", {"start": v(24, -3) * mm, "end": v(24, -1.5) * mm, "construction": true});
            skLineSegment(sketch, "E450", {"start": v(24, -1.5) * mm, "end": v(24, 1.5) * mm, "construction": true});
            skLineSegment(sketch, "E451", {"start": v(24, 1.5) * mm, "end": v(24, 3) * mm, "construction": true});
            skLineSegment(sketch, "E452", {"start": v(24, 3) * mm, "end": v(27.5, 3) * mm, "construction": true});
            skLineSegment(sketch, "E453", {"start": v(27.5, 3) * mm, "end": v(31, 3) * mm, "construction": true});
            skLineSegment(sketch, "E454", {"start": v(31, 3) * mm, "end": v(31, 1.5) * mm, "construction": true});
            skLineSegment(sketch, "E455", {"start": v(31, 1.5) * mm, "end": v(31, -1.5) * mm, "construction": true});
            skLineSegment(sketch, "E456", {"start": v(31, -1.5) * mm, "end": v(31, -3) * mm, "construction": true});
            skLineSegment(sketch, "E457", {"start": v(31, -3) * mm, "end": v(27.5, -3) * mm, "construction": true});
            skLineSegment(sketch, "E458", {"start": v(27.5, -3) * mm, "end": v(24, -3) * mm, "construction": true});
            skLineSegment(sketch, "E459", {"start": v(31, -1.5) * mm, "end": v(27.5, -3) * mm});
            skLineSegment(sketch, "E460", {"start": v(27.5, -3) * mm, "end": v(24, -1.5) * mm});
            skLineSegment(sketch, "E461", {"start": v(24, -1.5) * mm, "end": v(24, 1.5) * mm});
            skLineSegment(sketch, "E462", {"start": v(24, 1.5) * mm, "end": v(27.5, 3) * mm});
            skLineSegment(sketch, "E463", {"start": v(27.5, 3) * mm, "end": v(31, 1.5) * mm});
            skLineSegment(sketch, "E464", {"start": v(31, 1.5) * mm, "end": v(31, -1.5) * mm});
            skLineSegment(sketch, "E465", {"start": v(24, 0) * mm, "end": v(34, 0) * mm, "construction": true});
            skLineSegment(sketch, "E466", {"start": v(34, 0) * mm, "end": v(34, 3) * mm, "construction": true});
            skLineSegment(sketch, "E467", {"start": v(34, -3) * mm, "end": v(34, -1.5) * mm, "construction": true});
            skLineSegment(sketch, "E468", {"start": v(34, -1.5) * mm, "end": v(34, 1.5) * mm, "construction": true});
            skLineSegment(sketch, "E469", {"start": v(34, 1.5) * mm, "end": v(34, 3) * mm, "construction": true});
            skLineSegment(sketch, "E470", {"start": v(34, 3) * mm, "end": v(37.5, 3) * mm, "construction": true});
            skLineSegment(sketch, "E471", {"start": v(37.5, 3) * mm, "end": v(41, 3) * mm, "construction": true});
            skLineSegment(sketch, "E472", {"start": v(41, 3) * mm, "end": v(41, 1.5) * mm, "construction": true});
            skLineSegment(sketch, "E473", {"start": v(41, 1.5) * mm, "end": v(41, -1.5) * mm, "construction": true});
            skLineSegment(sketch, "E474", {"start": v(41, -1.5) * mm, "end": v(41, -3) * mm, "construction": true});
            skLineSegment(sketch, "E475", {"start": v(41, -3) * mm, "end": v(37.5, -3) * mm, "construction": true});
            skLineSegment(sketch, "E476", {"start": v(37.5, -3) * mm, "end": v(34, -3) * mm, "construction": true});
            skLineSegment(sketch, "E477", {"start": v(41, -1.5) * mm, "end": v(37.5, -3) * mm});
            skLineSegment(sketch, "E478", {"start": v(37.5, -3) * mm, "end": v(34, -1.5) * mm});
            skLineSegment(sketch, "E479", {"start": v(34, -1.5) * mm, "end": v(34, 1.5) * mm});
            skLineSegment(sketch, "E480", {"start": v(34, 1.5) * mm, "end": v(37.5, 3) * mm});
            skLineSegment(sketch, "E481", {"start": v(37.5, 3) * mm, "end": v(41, 1.5) * mm});
            skLineSegment(sketch, "E482", {"start": v(41, 1.5) * mm, "end": v(41, -1.5) * mm});
            skLineSegment(sketch, "E483", {"start": v(34, 0) * mm, "end": v(44, 0) * mm, "construction": true});
            skLineSegment(sketch, "E484", {"start": v(44, 0) * mm, "end": v(44, 3) * mm, "construction": true});
            skLineSegment(sketch, "E485", {"start": v(44, -3) * mm, "end": v(44, -1.5) * mm, "construction": true});
            skLineSegment(sketch, "E486", {"start": v(44, -1.5) * mm, "end": v(44, 1.5) * mm, "construction": true});
            skLineSegment(sketch, "E487", {"start": v(44, 1.5) * mm, "end": v(44, 3) * mm, "construction": true});
            skLineSegment(sketch, "E488", {"start": v(44, 3) * mm, "end": v(47.5, 3) * mm, "construction": true});
            skLineSegment(sketch, "E489", {"start": v(47.5, 3) * mm, "end": v(51, 3) * mm, "construction": true});
            skLineSegment(sketch, "E490", {"start": v(51, 3) * mm, "end": v(51, 1.5) * mm, "construction": true});
            skLineSegment(sketch, "E491", {"start": v(51, 1.5) * mm, "end": v(51, -1.5) * mm, "construction": true});
            skLineSegment(sketch, "E492", {"start": v(51, -1.5) * mm, "end": v(51, -3) * mm, "construction": true});
            skLineSegment(sketch, "E493", {"start": v(51, -3) * mm, "end": v(47.5, -3) * mm, "construction": true});
            skLineSegment(sketch, "E494", {"start": v(47.5, -3) * mm, "end": v(44, -3) * mm, "construction": true});
            skLineSegment(sketch, "E495", {"start": v(51, -1.5) * mm, "end": v(47.5, -3) * mm});
            skLineSegment(sketch, "E496", {"start": v(47.5, -3) * mm, "end": v(44, -1.5) * mm});
            skLineSegment(sketch, "E497", {"start": v(44, -1.5) * mm, "end": v(44, 1.5) * mm});
            skLineSegment(sketch, "E498", {"start": v(44, 1.5) * mm, "end": v(47.5, 3) * mm});
            skLineSegment(sketch, "E499", {"start": v(47.5, 3) * mm, "end": v(51, 1.5) * mm});
            skLineSegment(sketch, "E500", {"start": v(51, 1.5) * mm, "end": v(51, -1.5) * mm});
            skLineSegment(sketch, "E501", {"start": v(44, 0) * mm, "end": v(54, 0) * mm, "construction": true});
            skLineSegment(sketch, "E502", {"start": v(54, 0) * mm, "end": v(54, 3) * mm, "construction": true});
            skLineSegment(sketch, "E503", {"start": v(54, -3) * mm, "end": v(54, -1.5) * mm, "construction": true});
            skLineSegment(sketch, "E504", {"start": v(54, -1.5) * mm, "end": v(54, 1.5) * mm, "construction": true});
            skLineSegment(sketch, "E505", {"start": v(54, 1.5) * mm, "end": v(54, 3) * mm, "construction": true});
            skLineSegment(sketch, "E506", {"start": v(54, 3) * mm, "end": v(57.5, 3) * mm, "construction": true});
            skLineSegment(sketch, "E507", {"start": v(57.5, 3) * mm, "end": v(61, 3) * mm, "construction": true});
            skLineSegment(sketch, "E508", {"start": v(61, 3) * mm, "end": v(61, 1.5) * mm, "construction": true});
            skLineSegment(sketch, "E509", {"start": v(61, 1.5) * mm, "end": v(61, -1.5) * mm, "construction": true});
            skLineSegment(sketch, "E510", {"start": v(61, -1.5) * mm, "end": v(61, -3) * mm, "construction": true});
            skLineSegment(sketch, "E511", {"start": v(61, -3) * mm, "end": v(57.5, -3) * mm, "construction": true});
            skLineSegment(sketch, "E512", {"start": v(57.5, -3) * mm, "end": v(54, -3) * mm, "construction": true});
            skLineSegment(sketch, "E513", {"start": v(61, -1.5) * mm, "end": v(57.5, -3) * mm});
            skLineSegment(sketch, "E514", {"start": v(57.5, -3) * mm, "end": v(54, -1.5) * mm});
            skLineSegment(sketch, "E515", {"start": v(54, -1.5) * mm, "end": v(54, 1.5) * mm});
            skLineSegment(sketch, "E516", {"start": v(54, 1.5) * mm, "end": v(57.5, 3) * mm});
            skLineSegment(sketch, "E517", {"start": v(57.5, 3) * mm, "end": v(61, 1.5) * mm});
            skLineSegment(sketch, "E518", {"start": v(61, 1.5) * mm, "end": v(61, -1.5) * mm});
            skLineSegment(sketch, "E519", {"start": v(54, 0) * mm, "end": v(64, 0) * mm, "construction": true});
            skLineSegment(sketch, "E520", {"start": v(64, 0) * mm, "end": v(64, 3) * mm, "construction": true});
            skLineSegment(sketch, "E521", {"start": v(64, -3) * mm, "end": v(64, -1.5) * mm, "construction": true});
            skLineSegment(sketch, "E522", {"start": v(64, -1.5) * mm, "end": v(64, 1.5) * mm, "construction": true});
            skLineSegment(sketch, "E523", {"start": v(64, 1.5) * mm, "end": v(64, 3) * mm, "construction": true});
            skLineSegment(sketch, "E524", {"start": v(64, 3) * mm, "end": v(67.5, 3) * mm, "construction": true});
            skLineSegment(sketch, "E525", {"start": v(67.5, 3) * mm, "end": v(71, 3) * mm, "construction": true});
            skLineSegment(sketch, "E526", {"start": v(71, 3) * mm, "end": v(71, 1.5) * mm, "construction": true});
            skLineSegment(sketch, "E527", {"start": v(71, 1.5) * mm, "end": v(71, -1.5) * mm, "construction": true});
            skLineSegment(sketch, "E528", {"start": v(71, -1.5) * mm, "end": v(71, -3) * mm, "construction": true});
            skLineSegment(sketch, "E529", {"start": v(71, -3) * mm, "end": v(67.5, -3) * mm, "construction": true});
            skLineSegment(sketch, "E530", {"start": v(67.5, -3) * mm, "end": v(64, -3) * mm, "construction": true});
            skLineSegment(sketch, "E531", {"start": v(71, -1.5) * mm, "end": v(67.5, -3) * mm});
            skLineSegment(sketch, "E532", {"start": v(67.5, -3) * mm, "end": v(64, -1.5) * mm});
            skLineSegment(sketch, "E533", {"start": v(64, -1.5) * mm, "end": v(64, 1.5) * mm});
            skLineSegment(sketch, "E534", {"start": v(64, 1.5) * mm, "end": v(67.5, 3) * mm});
            skLineSegment(sketch, "E535", {"start": v(67.5, 3) * mm, "end": v(71, 1.5) * mm});
            skLineSegment(sketch, "E536", {"start": v(71, 1.5) * mm, "end": v(71, -1.5) * mm});
            skLineSegment(sketch, "E537", {"start": v(64, 0) * mm, "end": v(74, 0) * mm, "construction": true});
            skLineSegment(sketch, "E538", {"start": v(74, 0) * mm, "end": v(74, 3) * mm, "construction": true});
            skLineSegment(sketch, "E539", {"start": v(74, -3) * mm, "end": v(74, -1.5) * mm, "construction": true});
            skLineSegment(sketch, "E540", {"start": v(74, -1.5) * mm, "end": v(74, 1.5) * mm, "construction": true});
            skLineSegment(sketch, "E541", {"start": v(74, 1.5) * mm, "end": v(74, 3) * mm, "construction": true});
            skLineSegment(sketch, "E542", {"start": v(74, 3) * mm, "end": v(77.5, 3) * mm, "construction": true});
            skLineSegment(sketch, "E543", {"start": v(77.5, 3) * mm, "end": v(81, 3) * mm, "construction": true});
            skLineSegment(sketch, "E544", {"start": v(81, 3) * mm, "end": v(81, 1.5) * mm, "construction": true});
            skLineSegment(sketch, "E545", {"start": v(81, 1.5) * mm, "end": v(81, -1.5) * mm, "construction": true});
            skLineSegment(sketch, "E546", {"start": v(81, -1.5) * mm, "end": v(81, -3) * mm, "construction": true});
            skLineSegment(sketch, "E547", {"start": v(81, -3) * mm, "end": v(77.5, -3) * mm, "construction": true});
            skLineSegment(sketch, "E548", {"start": v(77.5, -3) * mm, "end": v(74, -3) * mm, "construction": true});
            skLineSegment(sketch, "E549", {"start": v(81, -1.5) * mm, "end": v(77.5, -3) * mm});
            skLineSegment(sketch, "E550", {"start": v(77.5, -3) * mm, "end": v(74, -1.5) * mm});
            skLineSegment(sketch, "E551", {"start": v(74, -1.5) * mm, "end": v(74, 1.5) * mm});
            skLineSegment(sketch, "E552", {"start": v(74, 1.5) * mm, "end": v(77.5, 3) * mm});
            skLineSegment(sketch, "E553", {"start": v(77.5, 3) * mm, "end": v(81, 1.5) * mm});
            skLineSegment(sketch, "E554", {"start": v(81, 1.5) * mm, "end": v(81, -1.5) * mm});
            skLineSegment(sketch, "E555", {"start": v(11, -1.5) * mm, "end": v(9, -1.5) * mm, "construction": true});
            skLineSegment(sketch, "E556", {"start": v(9, -1.5) * mm, "end": v(9, -2.36) * mm});
            skLineSegment(sketch, "E557", {"start": v(9, -1.5) * mm, "end": v(9, 2.36) * mm});
            skLineSegment(sketch, "E558", {"start": v(11, -1.5) * mm, "end": v(9, -2.36) * mm});
            skLineSegment(sketch, "E559", {"start": v(11, 1.5) * mm, "end": v(9, 2.36) * mm});
            skSolve(sketch);
        }
        {
            var Q0;
            Q0=qSketchRegion(id+"F11",true);
            extrude(context, id + "F12", {"entities" : qUnion([Q0]), "operationType" : NewBodyOperationType.REMOVE, "endBound" : BoundingType.SYMMETRIC, "oppositeDirection" : true, "depth" : 25 * mm});
        }
        {
            var Q0;
            Q0=makeQuery(id+"F1.opExtrude","CAP_EDGE",EDGE,{"disambiguationData":[OSD([sQuery(id+"F0.wireOp",EDGE,"E0")])],"isStart":true});
            fillet(context, id + "F13", {"entities" : qUnion([Q0]), "radius" : 1.5 * mm, "tangentPropagation" : true, "allowEdgeOverflow" : false});
        }
        {
            var Q0;
            Q0=makeQuery(id+"F5.boolean.opBoolean","INTERSECT",EDGE,{"disambiguationData":[OD(0.0)],"derivedFrom":[makeQuery(id+"F1.opExtrude","SWEPT_FACE",FACE,{"disambiguationData":[OSD([sQuery(id+"F0.wireOp",EDGE,"E0")])]}),makeQuery(id+"F5.opExtrude","SWEPT_FACE",FACE,{"disambiguationData":[OSD([sQuery(id+"F4.wireOp",EDGE,"b579cf08-57c8-4be4-a64a-6a7c8f7f1ba5")])]})]});
            var Q1;
            Q1=makeQuery(id+"F5.boolean.opBoolean","INTERSECT",EDGE,{"disambiguationData":[OD(0.0)],"derivedFrom":[makeQuery(id+"F1.opExtrude","SWEPT_FACE",FACE,{"disambiguationData":[OSD([sQuery(id+"F0.wireOp",EDGE,"E0")])]}),makeQuery(id+"F5.opExtrude","SWEPT_FACE",FACE,{"disambiguationData":[OSD([sQuery(id+"F4.wireOp",EDGE,"bcb0f5b9-98e4-4035-bb5b-1a8c92403a19")])]})]});
            var Q2;
            Q2=makeQuery(id+"F5.boolean.opBoolean","INTERSECT",EDGE,{"disambiguationData":[OD(0.0)],"derivedFrom":[makeQuery(id+"F1.opExtrude","SWEPT_FACE",FACE,{"disambiguationData":[OSD([sQuery(id+"F0.wireOp",EDGE,"E0")])]}),makeQuery(id+"F5.opExtrude","SWEPT_FACE",FACE,{"disambiguationData":[OSD([sQuery(id+"F4.wireOp",EDGE,"09477fc4-9d29-4f20-8901-aec53dcd1546")])]})]});
            var Q3;
            Q3=makeQuery(id+"F5.boolean.opBoolean","INTERSECT",EDGE,{"disambiguationData":[OD(0.0)],"derivedFrom":[makeQuery(id+"F1.opExtrude","SWEPT_FACE",FACE,{"disambiguationData":[OSD([sQuery(id+"F0.wireOp",EDGE,"E0")])]}),makeQuery(id+"F5.opExtrude","SWEPT_FACE",FACE,{"disambiguationData":[OSD([sQuery(id+"F4.wireOp",EDGE,"92af876a-0958-4a7c-97b2-f4e8acbef095")])]})]});
            var Q4;
            Q4=makeQuery(id+"F5.boolean.opBoolean","INTERSECT",EDGE,{"disambiguationData":[OD(0.0)],"derivedFrom":[makeQuery(id+"F1.opExtrude","SWEPT_FACE",FACE,{"disambiguationData":[OSD([sQuery(id+"F0.wireOp",EDGE,"E0")])]}),makeQuery(id+"F5.opExtrude","SWEPT_FACE",FACE,{"disambiguationData":[OSD([sQuery(id+"F4.wireOp",EDGE,"67b481ec-10fe-46d3-8faa-ebe6010fe4f1")])]})]});
            var Q5;
            Q5=makeQuery(id+"F5.boolean.opBoolean","INTERSECT",EDGE,{"disambiguationData":[OD(0.0)],"derivedFrom":[makeQuery(id+"F1.opExtrude","SWEPT_FACE",FACE,{"disambiguationData":[OSD([sQuery(id+"F0.wireOp",EDGE,"E0")])]}),makeQuery(id+"F5.opExtrude","SWEPT_FACE",FACE,{"disambiguationData":[OSD([sQuery(id+"F4.wireOp",EDGE,"aca02d5f-46a9-486e-88e3-eb9aae4273e8")])]})]});
            var Q6;
            Q6=makeQuery(id+"F5.boolean.opBoolean","INTERSECT",EDGE,{"disambiguationData":[OD(0.0)],"derivedFrom":[makeQuery(id+"F1.opExtrude","SWEPT_FACE",FACE,{"disambiguationData":[OSD([sQuery(id+"F0.wireOp",EDGE,"E0")])]}),makeQuery(id+"F5.opExtrude","SWEPT_FACE",FACE,{"disambiguationData":[OSD([sQuery(id+"F4.wireOp",EDGE,"76385219-3691-4f38-9da5-edf1140a4629")])]})]});
            var Q7;
            Q7=makeQuery(id+"F5.boolean.opBoolean","INTERSECT",EDGE,{"disambiguationData":[OD(0.0)],"derivedFrom":[makeQuery(id+"F1.opExtrude","SWEPT_FACE",FACE,{"disambiguationData":[OSD([sQuery(id+"F0.wireOp",EDGE,"E0")])]}),makeQuery(id+"F5.opExtrude","SWEPT_FACE",FACE,{"disambiguationData":[OSD([sQuery(id+"F4.wireOp",EDGE,"30311b2f-ed17-4601-a199-a8278ef993fb")])]})]});
            var Q8;
            Q8=makeQuery(id+"F5.boolean.opBoolean","INTERSECT",EDGE,{"disambiguationData":[OD(0.0)],"derivedFrom":[makeQuery(id+"F1.opExtrude","SWEPT_FACE",FACE,{"disambiguationData":[OSD([sQuery(id+"F0.wireOp",EDGE,"E0")])]}),makeQuery(id+"F5.opExtrude","SWEPT_FACE",FACE,{"disambiguationData":[OSD([sQuery(id+"F4.wireOp",EDGE,"ed008b68-955d-4315-9cc0-8abb2c6860b0")])]})]});
            var Q9;
            Q9=makeQuery(id+"F5.boolean.opBoolean","INTERSECT",EDGE,{"disambiguationData":[OD(0.0)],"derivedFrom":[makeQuery(id+"F1.opExtrude","SWEPT_FACE",FACE,{"disambiguationData":[OSD([sQuery(id+"F0.wireOp",EDGE,"E0")])]}),makeQuery(id+"F5.opExtrude","SWEPT_FACE",FACE,{"disambiguationData":[OSD([sQuery(id+"F4.wireOp",EDGE,"efc5e5b1-0746-45f0-90e3-bd883f3492f4")])]})]});
            var Q10;
            Q10=makeQuery(id+"F5.boolean.opBoolean","INTERSECT",EDGE,{"disambiguationData":[OD(0.0)],"derivedFrom":[makeQuery(id+"F1.opExtrude","SWEPT_FACE",FACE,{"disambiguationData":[OSD([sQuery(id+"F0.wireOp",EDGE,"E0")])]}),makeQuery(id+"F5.opExtrude","SWEPT_FACE",FACE,{"disambiguationData":[OSD([sQuery(id+"F4.wireOp",EDGE,"562b9cc4-530f-4157-bc84-2c37910fa221")])]})]});
            var Q11;
            Q11=makeQuery(id+"F5.boolean.opBoolean","INTERSECT",EDGE,{"disambiguationData":[OD(0.0)],"derivedFrom":[makeQuery(id+"F1.opExtrude","SWEPT_FACE",FACE,{"disambiguationData":[OSD([sQuery(id+"F0.wireOp",EDGE,"E0")])]}),makeQuery(id+"F5.opExtrude","SWEPT_FACE",FACE,{"disambiguationData":[OSD([sQuery(id+"F4.wireOp",EDGE,"ab9f0dd0-8a88-45b5-9e6c-47f07906d12f")])]})]});
            var Q12;
            Q12=makeQuery(id+"F5.boolean.opBoolean","INTERSECT",EDGE,{"disambiguationData":[OD(0.0)],"derivedFrom":[makeQuery(id+"F1.opExtrude","SWEPT_FACE",FACE,{"disambiguationData":[OSD([sQuery(id+"F0.wireOp",EDGE,"E0")])]}),makeQuery(id+"F5.opExtrude","SWEPT_FACE",FACE,{"disambiguationData":[OSD([sQuery(id+"F4.wireOp",EDGE,"5e54ec67-0438-4ccb-ab1e-fb0c5627ff7a")])]})]});
            var Q13;
            Q13=makeQuery(id+"F5.boolean.opBoolean","INTERSECT",EDGE,{"disambiguationData":[OD(0.0)],"derivedFrom":[makeQuery(id+"F1.opExtrude","SWEPT_FACE",FACE,{"disambiguationData":[OSD([sQuery(id+"F0.wireOp",EDGE,"E0")])]}),makeQuery(id+"F5.opExtrude","SWEPT_FACE",FACE,{"disambiguationData":[OSD([sQuery(id+"F4.wireOp",EDGE,"1da9000e-137c-457e-9dd6-58b65176467c")])]})]});
            var Q14;
            Q14=makeQuery(id+"F5.boolean.opBoolean","INTERSECT",EDGE,{"disambiguationData":[OD(0.0)],"derivedFrom":[makeQuery(id+"F1.opExtrude","SWEPT_FACE",FACE,{"disambiguationData":[OSD([sQuery(id+"F0.wireOp",EDGE,"E0")])]}),makeQuery(id+"F5.opExtrude","SWEPT_FACE",FACE,{"disambiguationData":[OSD([sQuery(id+"F4.wireOp",EDGE,"15ec9440-3994-4756-befc-73e6937f9073")])]})]});
            var Q15;
            Q15=makeQuery(id+"F5.boolean.opBoolean","INTERSECT",EDGE,{"disambiguationData":[OD(0.0)],"derivedFrom":[makeQuery(id+"F1.opExtrude","SWEPT_FACE",FACE,{"disambiguationData":[OSD([sQuery(id+"F0.wireOp",EDGE,"E0")])]}),makeQuery(id+"F5.opExtrude","SWEPT_FACE",FACE,{"disambiguationData":[OSD([sQuery(id+"F4.wireOp",EDGE,"70ca714e-c3bb-4dc2-844f-e69955e1961d")])]})]});
            var Q16;
            Q16=makeQuery(id+"F5.boolean.opBoolean","INTERSECT",EDGE,{"disambiguationData":[OD(0.0)],"derivedFrom":[makeQuery(id+"F1.opExtrude","SWEPT_FACE",FACE,{"disambiguationData":[OSD([sQuery(id+"F0.wireOp",EDGE,"E0")])]}),makeQuery(id+"F5.opExtrude","SWEPT_FACE",FACE,{"disambiguationData":[OSD([sQuery(id+"F4.wireOp",EDGE,"b9a5c8a8-e1c1-4ccb-a6a4-30bc00998619")])]})]});
            var Q17;
            Q17=makeQuery(id+"F5.boolean.opBoolean","INTERSECT",EDGE,{"disambiguationData":[OD(0.0)],"derivedFrom":[makeQuery(id+"F1.opExtrude","SWEPT_FACE",FACE,{"disambiguationData":[OSD([sQuery(id+"F0.wireOp",EDGE,"E0")])]}),makeQuery(id+"F5.opExtrude","SWEPT_FACE",FACE,{"disambiguationData":[OSD([sQuery(id+"F4.wireOp",EDGE,"66c2d1b9-9082-457f-8158-46fefb0d0b5d")])]})]});
            var Q18;
            Q18=makeQuery(id+"F5.boolean.opBoolean","INTERSECT",EDGE,{"disambiguationData":[OD(0.0)],"derivedFrom":[makeQuery(id+"F1.opExtrude","SWEPT_FACE",FACE,{"disambiguationData":[OSD([sQuery(id+"F0.wireOp",EDGE,"E0")])]}),makeQuery(id+"F5.opExtrude","SWEPT_FACE",FACE,{"disambiguationData":[OSD([sQuery(id+"F4.wireOp",EDGE,"fd9b85d0-086e-4753-9286-7d80f3d11dd9")])]})]});
            var Q19;
            Q19=makeQuery(id+"F5.boolean.opBoolean","INTERSECT",EDGE,{"disambiguationData":[OD(0.0)],"derivedFrom":[makeQuery(id+"F1.opExtrude","SWEPT_FACE",FACE,{"disambiguationData":[OSD([sQuery(id+"F0.wireOp",EDGE,"E0")])]}),makeQuery(id+"F5.opExtrude","SWEPT_FACE",FACE,{"disambiguationData":[OSD([sQuery(id+"F4.wireOp",EDGE,"82180203-eaff-47f3-b606-d8d7c32d142f")])]})]});
            var Q20;
            Q20=makeQuery(id+"F5.boolean.opBoolean","INTERSECT",EDGE,{"disambiguationData":[OD(0.0)],"derivedFrom":[makeQuery(id+"F1.opExtrude","SWEPT_FACE",FACE,{"disambiguationData":[OSD([sQuery(id+"F0.wireOp",EDGE,"E0")])]}),makeQuery(id+"F5.opExtrude","SWEPT_FACE",FACE,{"disambiguationData":[OSD([sQuery(id+"F4.wireOp",EDGE,"536ab4de-4fb2-4d7d-9807-1d714ccadb66")])]})]});
            var Q21;
            Q21=makeQuery(id+"F5.boolean.opBoolean","INTERSECT",EDGE,{"disambiguationData":[OD(0.0)],"derivedFrom":[makeQuery(id+"F1.opExtrude","SWEPT_FACE",FACE,{"disambiguationData":[OSD([sQuery(id+"F0.wireOp",EDGE,"E0")])]}),makeQuery(id+"F5.opExtrude","SWEPT_FACE",FACE,{"disambiguationData":[OSD([sQuery(id+"F4.wireOp",EDGE,"c5cda94b-8dbb-4131-8629-d94229ce36f8")])]})]});
            var Q22;
            Q22=makeQuery(id+"F5.boolean.opBoolean","INTERSECT",EDGE,{"disambiguationData":[OD(0.0)],"derivedFrom":[makeQuery(id+"F1.opExtrude","SWEPT_FACE",FACE,{"disambiguationData":[OSD([sQuery(id+"F0.wireOp",EDGE,"E0")])]}),makeQuery(id+"F5.opExtrude","SWEPT_FACE",FACE,{"disambiguationData":[OSD([sQuery(id+"F4.wireOp",EDGE,"b8538754-f3f1-4cf7-bfe9-078eb6985bef")])]})]});
            var Q23;
            Q23=makeQuery(id+"F5.boolean.opBoolean","INTERSECT",EDGE,{"disambiguationData":[OD(0.0)],"derivedFrom":[makeQuery(id+"F1.opExtrude","SWEPT_FACE",FACE,{"disambiguationData":[OSD([sQuery(id+"F0.wireOp",EDGE,"E0")])]}),makeQuery(id+"F5.opExtrude","SWEPT_FACE",FACE,{"disambiguationData":[OSD([sQuery(id+"F4.wireOp",EDGE,"9e1b2bd2-a8a3-4caa-b598-0f2db5d1325d")])]})]});
            var Q24;
            Q24=makeQuery(id+"F5.boolean.opBoolean","INTERSECT",EDGE,{"disambiguationData":[OD(0.0)],"derivedFrom":[makeQuery(id+"F1.opExtrude","SWEPT_FACE",FACE,{"disambiguationData":[OSD([sQuery(id+"F0.wireOp",EDGE,"E0")])]}),makeQuery(id+"F5.opExtrude","SWEPT_FACE",FACE,{"disambiguationData":[OSD([sQuery(id+"F4.wireOp",EDGE,"c0d87fc6-e010-4d73-961e-dfed47c8a1b3")])]})]});
            var Q25;
            Q25=makeQuery(id+"F5.boolean.opBoolean","INTERSECT",EDGE,{"disambiguationData":[OD(0.0)],"derivedFrom":[makeQuery(id+"F1.opExtrude","SWEPT_FACE",FACE,{"disambiguationData":[OSD([sQuery(id+"F0.wireOp",EDGE,"E0")])]}),makeQuery(id+"F5.opExtrude","SWEPT_FACE",FACE,{"disambiguationData":[OSD([sQuery(id+"F4.wireOp",EDGE,"14d064f9-5360-4d18-9d9e-82328bf9daba")])]})]});
            var Q26;
            Q26=makeQuery(id+"F5.boolean.opBoolean","INTERSECT",EDGE,{"disambiguationData":[OD(0.0)],"derivedFrom":[makeQuery(id+"F1.opExtrude","SWEPT_FACE",FACE,{"disambiguationData":[OSD([sQuery(id+"F0.wireOp",EDGE,"E0")])]}),makeQuery(id+"F5.opExtrude","SWEPT_FACE",FACE,{"disambiguationData":[OSD([sQuery(id+"F4.wireOp",EDGE,"b60fa973-c727-4668-bfa0-a1e16f7a99aa")])]})]});
            var Q27;
            Q27=makeQuery(id+"F5.boolean.opBoolean","INTERSECT",EDGE,{"disambiguationData":[OD(0.0)],"derivedFrom":[makeQuery(id+"F1.opExtrude","SWEPT_FACE",FACE,{"disambiguationData":[OSD([sQuery(id+"F0.wireOp",EDGE,"E0")])]}),makeQuery(id+"F5.opExtrude","SWEPT_FACE",FACE,{"disambiguationData":[OSD([sQuery(id+"F4.wireOp",EDGE,"978e1622-7887-4f07-a91b-81f9d5efcfbf")])]})]});
            var Q28;
            Q28=makeQuery(id+"F5.boolean.opBoolean","INTERSECT",EDGE,{"disambiguationData":[OD(0.0)],"derivedFrom":[makeQuery(id+"F1.opExtrude","SWEPT_FACE",FACE,{"disambiguationData":[OSD([sQuery(id+"F0.wireOp",EDGE,"E0")])]}),makeQuery(id+"F5.opExtrude","SWEPT_FACE",FACE,{"disambiguationData":[OSD([sQuery(id+"F4.wireOp",EDGE,"d0a2849f-a89e-4989-ab6e-8e188e140a90")])]})]});
            var Q29;
            Q29=makeQuery(id+"F5.boolean.opBoolean","INTERSECT",EDGE,{"disambiguationData":[OD(0.0)],"derivedFrom":[makeQuery(id+"F1.opExtrude","SWEPT_FACE",FACE,{"disambiguationData":[OSD([sQuery(id+"F0.wireOp",EDGE,"E0")])]}),makeQuery(id+"F5.opExtrude","SWEPT_FACE",FACE,{"disambiguationData":[OSD([sQuery(id+"F4.wireOp",EDGE,"f55199c0-7004-4acb-b4c7-226994b61401")])]})]});
            var Q30;
            Q30=makeQuery(id+"F5.boolean.opBoolean","INTERSECT",EDGE,{"disambiguationData":[OD(0.0)],"derivedFrom":[makeQuery(id+"F1.opExtrude","SWEPT_FACE",FACE,{"disambiguationData":[OSD([sQuery(id+"F0.wireOp",EDGE,"E0")])]}),makeQuery(id+"F5.opExtrude","SWEPT_FACE",FACE,{"disambiguationData":[OSD([sQuery(id+"F4.wireOp",EDGE,"8a1b3b7c-f627-453a-8324-eadb2e6b2aa6")])]})]});
            var Q31;
            Q31=makeQuery(id+"F5.boolean.opBoolean","INTERSECT",EDGE,{"disambiguationData":[OD(0.0)],"derivedFrom":[makeQuery(id+"F1.opExtrude","SWEPT_FACE",FACE,{"disambiguationData":[OSD([sQuery(id+"F0.wireOp",EDGE,"E0")])]}),makeQuery(id+"F5.opExtrude","SWEPT_FACE",FACE,{"disambiguationData":[OSD([sQuery(id+"F4.wireOp",EDGE,"d52b0a11-5b01-40f3-ab4f-3d3d9242be96")])]})]});
            var Q32;
            Q32=makeQuery(id+"F5.boolean.opBoolean","INTERSECT",EDGE,{"disambiguationData":[OD(0.0)],"derivedFrom":[makeQuery(id+"F1.opExtrude","SWEPT_FACE",FACE,{"disambiguationData":[OSD([sQuery(id+"F0.wireOp",EDGE,"E0")])]}),makeQuery(id+"F5.opExtrude","SWEPT_FACE",FACE,{"disambiguationData":[OSD([sQuery(id+"F4.wireOp",EDGE,"E137")])]})]});
            var Q33;
            Q33=makeQuery(id+"F5.boolean.opBoolean","INTERSECT",EDGE,{"disambiguationData":[OD(0.0)],"derivedFrom":[makeQuery(id+"F1.opExtrude","SWEPT_FACE",FACE,{"disambiguationData":[OSD([sQuery(id+"F0.wireOp",EDGE,"E0")])]}),makeQuery(id+"F5.opExtrude","SWEPT_FACE",FACE,{"disambiguationData":[OSD([sQuery(id+"F4.wireOp",EDGE,"E136")])]})]});
            var Q34;
            Q34=makeQuery(id+"F5.boolean.opBoolean","INTERSECT",EDGE,{"disambiguationData":[OD(0.0)],"derivedFrom":[makeQuery(id+"F1.opExtrude","SWEPT_FACE",FACE,{"disambiguationData":[OSD([sQuery(id+"F0.wireOp",EDGE,"E0")])]}),makeQuery(id+"F5.opExtrude","SWEPT_FACE",FACE,{"disambiguationData":[OSD([sQuery(id+"F4.wireOp",EDGE,"E135")])]})]});
            var Q35;
            Q35=makeQuery(id+"F5.boolean.opBoolean","INTERSECT",EDGE,{"disambiguationData":[OD(0.0)],"derivedFrom":[makeQuery(id+"F1.opExtrude","SWEPT_FACE",FACE,{"disambiguationData":[OSD([sQuery(id+"F0.wireOp",EDGE,"E0")])]}),makeQuery(id+"F5.opExtrude","SWEPT_FACE",FACE,{"disambiguationData":[OSD([sQuery(id+"F4.wireOp",EDGE,"c79ec3c5-8163-43ca-85dc-8d9b1c829184")])]})]});
            var Q36;
            Q36=makeQuery(id+"F5.boolean.opBoolean","INTERSECT",EDGE,{"disambiguationData":[OD(0.0)],"derivedFrom":[makeQuery(id+"F1.opExtrude","SWEPT_FACE",FACE,{"disambiguationData":[OSD([sQuery(id+"F0.wireOp",EDGE,"E0")])]}),makeQuery(id+"F5.opExtrude","SWEPT_FACE",FACE,{"disambiguationData":[OSD([sQuery(id+"F4.wireOp",EDGE,"E125")])]})]});
            var Q37;
            Q37=makeQuery(id+"F5.boolean.opBoolean","INTERSECT",EDGE,{"disambiguationData":[OD(0.0)],"derivedFrom":[makeQuery(id+"F1.opExtrude","SWEPT_FACE",FACE,{"disambiguationData":[OSD([sQuery(id+"F0.wireOp",EDGE,"E0")])]}),makeQuery(id+"F5.opExtrude","SWEPT_FACE",FACE,{"disambiguationData":[OSD([sQuery(id+"F4.wireOp",EDGE,"E126")])]})]});
            var Q38;
            Q38=makeQuery(id+"F5.boolean.opBoolean","INTERSECT",EDGE,{"disambiguationData":[OD(0.0)],"derivedFrom":[makeQuery(id+"F1.opExtrude","SWEPT_FACE",FACE,{"disambiguationData":[OSD([sQuery(id+"F0.wireOp",EDGE,"E0")])]}),makeQuery(id+"F5.opExtrude","SWEPT_FACE",FACE,{"disambiguationData":[OSD([sQuery(id+"F4.wireOp",EDGE,"E127")])]})]});
            var Q39;
            Q39=makeQuery(id+"F5.boolean.opBoolean","INTERSECT",EDGE,{"disambiguationData":[OD(0.0)],"derivedFrom":[makeQuery(id+"F1.opExtrude","SWEPT_FACE",FACE,{"disambiguationData":[OSD([sQuery(id+"F0.wireOp",EDGE,"E0")])]}),makeQuery(id+"F5.opExtrude","SWEPT_FACE",FACE,{"disambiguationData":[OSD([sQuery(id+"F4.wireOp",EDGE,"E122")])]})]});
            var Q40;
            Q40=makeQuery(id+"F5.boolean.opBoolean","INTERSECT",EDGE,{"disambiguationData":[OD(0.0)],"derivedFrom":[makeQuery(id+"F1.opExtrude","SWEPT_FACE",FACE,{"disambiguationData":[OSD([sQuery(id+"F0.wireOp",EDGE,"E0")])]}),makeQuery(id+"F5.opExtrude","SWEPT_FACE",FACE,{"disambiguationData":[OSD([sQuery(id+"F4.wireOp",EDGE,"E123")])]})]});
            var Q41;
            Q41=makeQuery(id+"F5.boolean.opBoolean","INTERSECT",EDGE,{"disambiguationData":[OD(0.0)],"derivedFrom":[makeQuery(id+"F1.opExtrude","SWEPT_FACE",FACE,{"disambiguationData":[OSD([sQuery(id+"F0.wireOp",EDGE,"E0")])]}),makeQuery(id+"F5.opExtrude","SWEPT_FACE",FACE,{"disambiguationData":[OSD([sQuery(id+"F4.wireOp",EDGE,"E124")])]})]});
            var Q42;
            Q42=makeQuery(id+"F5.boolean.opBoolean","INTERSECT",EDGE,{"disambiguationData":[OD(0.0)],"derivedFrom":[makeQuery(id+"F1.opExtrude","SWEPT_FACE",FACE,{"disambiguationData":[OSD([sQuery(id+"F0.wireOp",EDGE,"E0")])]}),makeQuery(id+"F5.opExtrude","SWEPT_FACE",FACE,{"disambiguationData":[OSD([sQuery(id+"F4.wireOp",EDGE,"E109")])]})]});
            var Q43;
            Q43=makeQuery(id+"F5.boolean.opBoolean","INTERSECT",EDGE,{"disambiguationData":[OD(0.0)],"derivedFrom":[makeQuery(id+"F1.opExtrude","SWEPT_FACE",FACE,{"disambiguationData":[OSD([sQuery(id+"F0.wireOp",EDGE,"E0")])]}),makeQuery(id+"F5.opExtrude","SWEPT_FACE",FACE,{"disambiguationData":[OSD([sQuery(id+"F4.wireOp",EDGE,"E108")])]})]});
            var Q44;
            Q44=makeQuery(id+"F5.boolean.opBoolean","INTERSECT",EDGE,{"disambiguationData":[OD(0.0)],"derivedFrom":[makeQuery(id+"F1.opExtrude","SWEPT_FACE",FACE,{"disambiguationData":[OSD([sQuery(id+"F0.wireOp",EDGE,"E0")])]}),makeQuery(id+"F5.opExtrude","SWEPT_FACE",FACE,{"disambiguationData":[OSD([sQuery(id+"F4.wireOp",EDGE,"E107")])]})]});
            var Q45;
            Q45=makeQuery(id+"F5.boolean.opBoolean","INTERSECT",EDGE,{"disambiguationData":[OD(0.0)],"derivedFrom":[makeQuery(id+"F1.opExtrude","SWEPT_FACE",FACE,{"disambiguationData":[OSD([sQuery(id+"F0.wireOp",EDGE,"E0")])]}),makeQuery(id+"F5.opExtrude","SWEPT_FACE",FACE,{"disambiguationData":[OSD([sQuery(id+"F4.wireOp",EDGE,"E106")])]})]});
            var Q46;
            Q46=makeQuery(id+"F5.boolean.opBoolean","INTERSECT",EDGE,{"disambiguationData":[OD(0.0)],"derivedFrom":[makeQuery(id+"F1.opExtrude","SWEPT_FACE",FACE,{"disambiguationData":[OSD([sQuery(id+"F0.wireOp",EDGE,"E0")])]}),makeQuery(id+"F5.opExtrude","SWEPT_FACE",FACE,{"disambiguationData":[OSD([sQuery(id+"F4.wireOp",EDGE,"E105")])]})]});
            var Q47;
            Q47=makeQuery(id+"F5.boolean.opBoolean","INTERSECT",EDGE,{"disambiguationData":[OD(0.0)],"derivedFrom":[makeQuery(id+"F1.opExtrude","SWEPT_FACE",FACE,{"disambiguationData":[OSD([sQuery(id+"F0.wireOp",EDGE,"E0")])]}),makeQuery(id+"F5.opExtrude","SWEPT_FACE",FACE,{"disambiguationData":[OSD([sQuery(id+"F4.wireOp",EDGE,"E104")])]})]});
            var Q48;
            Q48=makeQuery(id+"F5.boolean.opBoolean","INTERSECT",EDGE,{"disambiguationData":[OD(0.0)],"derivedFrom":[makeQuery(id+"F1.opExtrude","SWEPT_FACE",FACE,{"disambiguationData":[OSD([sQuery(id+"F0.wireOp",EDGE,"E0")])]}),makeQuery(id+"F5.opExtrude","SWEPT_FACE",FACE,{"disambiguationData":[OSD([sQuery(id+"F4.wireOp",EDGE,"E86")])]})]});
            var Q49;
            Q49=makeQuery(id+"F5.boolean.opBoolean","INTERSECT",EDGE,{"disambiguationData":[OD(0.0)],"derivedFrom":[makeQuery(id+"F1.opExtrude","SWEPT_FACE",FACE,{"disambiguationData":[OSD([sQuery(id+"F0.wireOp",EDGE,"E0")])]}),makeQuery(id+"F5.opExtrude","SWEPT_FACE",FACE,{"disambiguationData":[OSD([sQuery(id+"F4.wireOp",EDGE,"E91")])]})]});
            var Q50;
            Q50=makeQuery(id+"F5.boolean.opBoolean","INTERSECT",EDGE,{"disambiguationData":[OD(0.0)],"derivedFrom":[makeQuery(id+"F1.opExtrude","SWEPT_FACE",FACE,{"disambiguationData":[OSD([sQuery(id+"F0.wireOp",EDGE,"E0")])]}),makeQuery(id+"F5.opExtrude","SWEPT_FACE",FACE,{"disambiguationData":[OSD([sQuery(id+"F4.wireOp",EDGE,"E90")])]})]});
            var Q51;
            Q51=makeQuery(id+"F5.boolean.opBoolean","INTERSECT",EDGE,{"disambiguationData":[OD(0.0)],"derivedFrom":[makeQuery(id+"F1.opExtrude","SWEPT_FACE",FACE,{"disambiguationData":[OSD([sQuery(id+"F0.wireOp",EDGE,"E0")])]}),makeQuery(id+"F5.opExtrude","SWEPT_FACE",FACE,{"disambiguationData":[OSD([sQuery(id+"F4.wireOp",EDGE,"E89")])]})]});
            var Q52;
            Q52=makeQuery(id+"F5.boolean.opBoolean","INTERSECT",EDGE,{"disambiguationData":[OD(0.0)],"derivedFrom":[makeQuery(id+"F1.opExtrude","SWEPT_FACE",FACE,{"disambiguationData":[OSD([sQuery(id+"F0.wireOp",EDGE,"E0")])]}),makeQuery(id+"F5.opExtrude","SWEPT_FACE",FACE,{"disambiguationData":[OSD([sQuery(id+"F4.wireOp",EDGE,"E88")])]})]});
            var Q53;
            Q53=makeQuery(id+"F5.boolean.opBoolean","INTERSECT",EDGE,{"disambiguationData":[OD(0.0)],"derivedFrom":[makeQuery(id+"F1.opExtrude","SWEPT_FACE",FACE,{"disambiguationData":[OSD([sQuery(id+"F0.wireOp",EDGE,"E0")])]}),makeQuery(id+"F5.opExtrude","SWEPT_FACE",FACE,{"disambiguationData":[OSD([sQuery(id+"F4.wireOp",EDGE,"E87")])]})]});
            var Q54;
            Q54=makeQuery(id+"F5.boolean.opBoolean","INTERSECT",EDGE,{"disambiguationData":[OD(0.0)],"derivedFrom":[makeQuery(id+"F1.opExtrude","SWEPT_FACE",FACE,{"disambiguationData":[OSD([sQuery(id+"F0.wireOp",EDGE,"E0")])]}),makeQuery(id+"F5.opExtrude","SWEPT_FACE",FACE,{"disambiguationData":[OSD([sQuery(id+"F4.wireOp",EDGE,"E71")])]})]});
            var Q55;
            Q55=makeQuery(id+"F5.boolean.opBoolean","INTERSECT",EDGE,{"disambiguationData":[OD(0.0)],"derivedFrom":[makeQuery(id+"F1.opExtrude","SWEPT_FACE",FACE,{"disambiguationData":[OSD([sQuery(id+"F0.wireOp",EDGE,"E0")])]}),makeQuery(id+"F5.opExtrude","SWEPT_FACE",FACE,{"disambiguationData":[OSD([sQuery(id+"F4.wireOp",EDGE,"E72")])]})]});
            var Q56;
            Q56=makeQuery(id+"F5.boolean.opBoolean","INTERSECT",EDGE,{"disambiguationData":[OD(0.0)],"derivedFrom":[makeQuery(id+"F1.opExtrude","SWEPT_FACE",FACE,{"disambiguationData":[OSD([sQuery(id+"F0.wireOp",EDGE,"E0")])]}),makeQuery(id+"F5.opExtrude","SWEPT_FACE",FACE,{"disambiguationData":[OSD([sQuery(id+"F4.wireOp",EDGE,"E73")])]})]});
            var Q57;
            Q57=makeQuery(id+"F5.boolean.opBoolean","INTERSECT",EDGE,{"disambiguationData":[OD(0.0)],"derivedFrom":[makeQuery(id+"F1.opExtrude","SWEPT_FACE",FACE,{"disambiguationData":[OSD([sQuery(id+"F0.wireOp",EDGE,"E0")])]}),makeQuery(id+"F5.opExtrude","SWEPT_FACE",FACE,{"disambiguationData":[OSD([sQuery(id+"F4.wireOp",EDGE,"E68")])]})]});
            var Q58;
            Q58=makeQuery(id+"F5.boolean.opBoolean","INTERSECT",EDGE,{"disambiguationData":[OD(0.0)],"derivedFrom":[makeQuery(id+"F1.opExtrude","SWEPT_FACE",FACE,{"disambiguationData":[OSD([sQuery(id+"F0.wireOp",EDGE,"E0")])]}),makeQuery(id+"F5.opExtrude","SWEPT_FACE",FACE,{"disambiguationData":[OSD([sQuery(id+"F4.wireOp",EDGE,"E69")])]})]});
            var Q59;
            Q59=makeQuery(id+"F5.boolean.opBoolean","INTERSECT",EDGE,{"disambiguationData":[OD(0.0)],"derivedFrom":[makeQuery(id+"F1.opExtrude","SWEPT_FACE",FACE,{"disambiguationData":[OSD([sQuery(id+"F0.wireOp",EDGE,"E0")])]}),makeQuery(id+"F5.opExtrude","SWEPT_FACE",FACE,{"disambiguationData":[OSD([sQuery(id+"F4.wireOp",EDGE,"E70")])]})]});
            var Q60;
            Q60=makeQuery(id+"F5.boolean.opBoolean","INTERSECT",EDGE,{"disambiguationData":[OD(0.0)],"derivedFrom":[makeQuery(id+"F1.opExtrude","SWEPT_FACE",FACE,{"disambiguationData":[OSD([sQuery(id+"F0.wireOp",EDGE,"E0")])]}),makeQuery(id+"F5.opExtrude","SWEPT_FACE",FACE,{"disambiguationData":[OSD([sQuery(id+"F4.wireOp",EDGE,"E55")])]})]});
            var Q61;
            Q61=makeQuery(id+"F5.boolean.opBoolean","INTERSECT",EDGE,{"disambiguationData":[OD(0.0)],"derivedFrom":[makeQuery(id+"F1.opExtrude","SWEPT_FACE",FACE,{"disambiguationData":[OSD([sQuery(id+"F0.wireOp",EDGE,"E0")])]}),makeQuery(id+"F5.opExtrude","SWEPT_FACE",FACE,{"disambiguationData":[OSD([sQuery(id+"F4.wireOp",EDGE,"E54")])]})]});
            var Q62;
            Q62=makeQuery(id+"F5.boolean.opBoolean","INTERSECT",EDGE,{"disambiguationData":[OD(0.0)],"derivedFrom":[makeQuery(id+"F1.opExtrude","SWEPT_FACE",FACE,{"disambiguationData":[OSD([sQuery(id+"F0.wireOp",EDGE,"E0")])]}),makeQuery(id+"F5.opExtrude","SWEPT_FACE",FACE,{"disambiguationData":[OSD([sQuery(id+"F4.wireOp",EDGE,"E53")])]})]});
            var Q63;
            Q63=makeQuery(id+"F5.boolean.opBoolean","INTERSECT",EDGE,{"disambiguationData":[OD(0.0)],"derivedFrom":[makeQuery(id+"F1.opExtrude","SWEPT_FACE",FACE,{"disambiguationData":[OSD([sQuery(id+"F0.wireOp",EDGE,"E0")])]}),makeQuery(id+"F5.opExtrude","SWEPT_FACE",FACE,{"disambiguationData":[OSD([sQuery(id+"F4.wireOp",EDGE,"E52")])]})]});
            var Q64;
            Q64=makeQuery(id+"F5.boolean.opBoolean","INTERSECT",EDGE,{"disambiguationData":[OD(0.0)],"derivedFrom":[makeQuery(id+"F1.opExtrude","SWEPT_FACE",FACE,{"disambiguationData":[OSD([sQuery(id+"F0.wireOp",EDGE,"E0")])]}),makeQuery(id+"F5.opExtrude","SWEPT_FACE",FACE,{"disambiguationData":[OSD([sQuery(id+"F4.wireOp",EDGE,"E51")])]})]});
            var Q65;
            Q65=makeQuery(id+"F5.boolean.opBoolean","INTERSECT",EDGE,{"disambiguationData":[OD(0.0)],"derivedFrom":[makeQuery(id+"F1.opExtrude","SWEPT_FACE",FACE,{"disambiguationData":[OSD([sQuery(id+"F0.wireOp",EDGE,"E0")])]}),makeQuery(id+"F5.opExtrude","SWEPT_FACE",FACE,{"disambiguationData":[OSD([sQuery(id+"F4.wireOp",EDGE,"E50")])]})]});
            var Q66;
            Q66=makeQuery(id+"F5.boolean.opBoolean","INTERSECT",EDGE,{"disambiguationData":[OD(0.0)],"derivedFrom":[makeQuery(id+"F1.opExtrude","SWEPT_FACE",FACE,{"disambiguationData":[OSD([sQuery(id+"F0.wireOp",EDGE,"E0")])]}),makeQuery(id+"F5.opExtrude","SWEPT_FACE",FACE,{"disambiguationData":[OSD([sQuery(id+"F4.wireOp",EDGE,"E37")])]})]});
            var Q67;
            Q67=makeQuery(id+"F5.boolean.opBoolean","INTERSECT",EDGE,{"disambiguationData":[OD(0.0)],"derivedFrom":[makeQuery(id+"F1.opExtrude","SWEPT_FACE",FACE,{"disambiguationData":[OSD([sQuery(id+"F0.wireOp",EDGE,"E0")])]}),makeQuery(id+"F5.opExtrude","SWEPT_FACE",FACE,{"disambiguationData":[OSD([sQuery(id+"F4.wireOp",EDGE,"E35")])]})]});
            var Q68;
            Q68=makeQuery(id+"F5.boolean.opBoolean","INTERSECT",EDGE,{"disambiguationData":[OD(0.0)],"derivedFrom":[makeQuery(id+"F1.opExtrude","SWEPT_FACE",FACE,{"disambiguationData":[OSD([sQuery(id+"F0.wireOp",EDGE,"E0")])]}),makeQuery(id+"F5.opExtrude","SWEPT_FACE",FACE,{"disambiguationData":[OSD([sQuery(id+"F4.wireOp",EDGE,"E34")])]})]});
            var Q69;
            Q69=makeQuery(id+"F5.boolean.opBoolean","INTERSECT",EDGE,{"disambiguationData":[OD(0.0)],"derivedFrom":[makeQuery(id+"F1.opExtrude","SWEPT_FACE",FACE,{"disambiguationData":[OSD([sQuery(id+"F0.wireOp",EDGE,"E0")])]}),makeQuery(id+"F5.opExtrude","SWEPT_FACE",FACE,{"disambiguationData":[OSD([sQuery(id+"F4.wireOp",EDGE,"E33")])]})]});
            var Q70;
            Q70=makeQuery(id+"F5.boolean.opBoolean","INTERSECT",EDGE,{"disambiguationData":[OD(0.0)],"derivedFrom":[makeQuery(id+"F1.opExtrude","SWEPT_FACE",FACE,{"disambiguationData":[OSD([sQuery(id+"F0.wireOp",EDGE,"E0")])]}),makeQuery(id+"F5.opExtrude","SWEPT_FACE",FACE,{"disambiguationData":[OSD([sQuery(id+"F4.wireOp",EDGE,"E32")])]})]});
            var Q71;
            Q71=makeQuery(id+"F5.boolean.opBoolean","INTERSECT",EDGE,{"disambiguationData":[OD(0.0)],"derivedFrom":[makeQuery(id+"F1.opExtrude","SWEPT_FACE",FACE,{"disambiguationData":[OSD([sQuery(id+"F0.wireOp",EDGE,"E0")])]}),makeQuery(id+"F5.opExtrude","SWEPT_FACE",FACE,{"disambiguationData":[OSD([sQuery(id+"F4.wireOp",EDGE,"E36")])]})]});
            var Q72;
            Q72=makeQuery(id+"F5.boolean.opBoolean","INTERSECT",EDGE,{"disambiguationData":[OD(0.0)],"derivedFrom":[makeQuery(id+"F1.opExtrude","SWEPT_FACE",FACE,{"disambiguationData":[OSD([sQuery(id+"F0.wireOp",EDGE,"E0")])]}),makeQuery(id+"F5.opExtrude","SWEPT_FACE",FACE,{"disambiguationData":[OSD([sQuery(id+"F4.wireOp",EDGE,"E17")])]})]});
            var Q73;
            Q73=makeQuery(id+"F5.boolean.opBoolean","INTERSECT",EDGE,{"disambiguationData":[OD(0.0)],"derivedFrom":[makeQuery(id+"F1.opExtrude","SWEPT_FACE",FACE,{"disambiguationData":[OSD([sQuery(id+"F0.wireOp",EDGE,"E0")])]}),makeQuery(id+"F5.opExtrude","SWEPT_FACE",FACE,{"disambiguationData":[OSD([sQuery(id+"F4.wireOp",EDGE,"E18")])]})]});
            var Q74;
            Q74=makeQuery(id+"F5.boolean.opBoolean","INTERSECT",EDGE,{"disambiguationData":[OD(0.0)],"derivedFrom":[makeQuery(id+"F1.opExtrude","SWEPT_FACE",FACE,{"disambiguationData":[OSD([sQuery(id+"F0.wireOp",EDGE,"E0")])]}),makeQuery(id+"F5.opExtrude","SWEPT_FACE",FACE,{"disambiguationData":[OSD([sQuery(id+"F4.wireOp",EDGE,"E19")])]})]});
            var Q75;
            Q75=makeQuery(id+"F5.boolean.opBoolean","INTERSECT",EDGE,{"disambiguationData":[OD(0.0)],"derivedFrom":[makeQuery(id+"F1.opExtrude","SWEPT_FACE",FACE,{"disambiguationData":[OSD([sQuery(id+"F0.wireOp",EDGE,"E0")])]}),makeQuery(id+"F5.opExtrude","SWEPT_FACE",FACE,{"disambiguationData":[OSD([sQuery(id+"F4.wireOp",EDGE,"E14")])]})]});
            var Q76;
            Q76=makeQuery(id+"F5.boolean.opBoolean","INTERSECT",EDGE,{"disambiguationData":[OD(0.0)],"derivedFrom":[makeQuery(id+"F1.opExtrude","SWEPT_FACE",FACE,{"disambiguationData":[OSD([sQuery(id+"F0.wireOp",EDGE,"E0")])]}),makeQuery(id+"F5.opExtrude","SWEPT_FACE",FACE,{"disambiguationData":[OSD([sQuery(id+"F4.wireOp",EDGE,"E15")])]})]});
            var Q77;
            Q77=makeQuery(id+"F5.boolean.opBoolean","INTERSECT",EDGE,{"disambiguationData":[OD(0.0)],"derivedFrom":[makeQuery(id+"F1.opExtrude","SWEPT_FACE",FACE,{"disambiguationData":[OSD([sQuery(id+"F0.wireOp",EDGE,"E0")])]}),makeQuery(id+"F5.opExtrude","SWEPT_FACE",FACE,{"disambiguationData":[OSD([sQuery(id+"F4.wireOp",EDGE,"E16")])]})]});
            var Q78;
            Q78=makeQuery(id+"F5.boolean.opBoolean","INTERSECT",EDGE,{"disambiguationData":[OD(0.0)],"derivedFrom":[makeQuery(id+"F1.opExtrude","SWEPT_FACE",FACE,{"disambiguationData":[OSD([sQuery(id+"F0.wireOp",EDGE,"E0")])]}),makeQuery(id+"F5.opExtrude","SWEPT_FACE",FACE,{"disambiguationData":[OSD([sQuery(id+"F4.wireOp",EDGE,"f02fcaa4-8809-4191-8bb9-9daee93d77e2")])]})]});
            var Q79;
            Q79=makeQuery(id+"F5.boolean.opBoolean","INTERSECT",EDGE,{"disambiguationData":[OD(0.0)],"derivedFrom":[makeQuery(id+"F1.opExtrude","SWEPT_FACE",FACE,{"disambiguationData":[OSD([sQuery(id+"F0.wireOp",EDGE,"E0")])]}),makeQuery(id+"F5.opExtrude","SWEPT_FACE",FACE,{"disambiguationData":[OSD([sQuery(id+"F4.wireOp",EDGE,"d264c38f-4b04-4a21-be61-ebc556e8b4dc")])]})]});
            var Q80;
            Q80=makeQuery(id+"F5.boolean.opBoolean","INTERSECT",EDGE,{"disambiguationData":[OD(0.0)],"derivedFrom":[makeQuery(id+"F1.opExtrude","SWEPT_FACE",FACE,{"disambiguationData":[OSD([sQuery(id+"F0.wireOp",EDGE,"E0")])]}),makeQuery(id+"F5.opExtrude","SWEPT_FACE",FACE,{"disambiguationData":[OSD([sQuery(id+"F4.wireOp",EDGE,"bd2a5c31-cc9d-444b-baf1-6f7b9b2beccf")])]})]});
            var Q81;
            Q81=makeQuery(id+"F5.boolean.opBoolean","INTERSECT",EDGE,{"disambiguationData":[OD(0.0)],"derivedFrom":[makeQuery(id+"F1.opExtrude","SWEPT_FACE",FACE,{"disambiguationData":[OSD([sQuery(id+"F0.wireOp",EDGE,"E0")])]}),makeQuery(id+"F5.opExtrude","SWEPT_FACE",FACE,{"disambiguationData":[OSD([sQuery(id+"F4.wireOp",EDGE,"19f739e4-1ef2-45c8-9f20-bd755fe40443")])]})]});
            var Q82;
            Q82=makeQuery(id+"F5.boolean.opBoolean","INTERSECT",EDGE,{"disambiguationData":[OD(0.0)],"derivedFrom":[makeQuery(id+"F1.opExtrude","SWEPT_FACE",FACE,{"disambiguationData":[OSD([sQuery(id+"F0.wireOp",EDGE,"E0")])]}),makeQuery(id+"F5.opExtrude","SWEPT_FACE",FACE,{"disambiguationData":[OSD([sQuery(id+"F4.wireOp",EDGE,"03b36015-34d2-4950-84e9-b550512b4ec9")])]})]});
            var Q83;
            Q83=makeQuery(id+"F5.boolean.opBoolean","INTERSECT",EDGE,{"disambiguationData":[OD(0.0)],"derivedFrom":[makeQuery(id+"F1.opExtrude","SWEPT_FACE",FACE,{"disambiguationData":[OSD([sQuery(id+"F0.wireOp",EDGE,"E0")])]}),makeQuery(id+"F5.opExtrude","SWEPT_FACE",FACE,{"disambiguationData":[OSD([sQuery(id+"F4.wireOp",EDGE,"10851094-9e06-4481-a16a-60cc523c1961")])]})]});
            var Q84;
            Q84=makeQuery(id+"F7.boolean.opBoolean","INTERSECT",EDGE,{"disambiguationData":[OD(0.0)],"derivedFrom":[makeQuery(id+"F1.opExtrude","SWEPT_FACE",FACE,{"disambiguationData":[OSD([sQuery(id+"F0.wireOp",EDGE,"E0")])]}),makeQuery(id+"F7.opExtrude","SWEPT_FACE",FACE,{"disambiguationData":[OSD([sQuery(id+"F6.wireOp",EDGE,"22307501-336a-4987-af9f-3473d2358a36")])]})]});
            var Q85;
            Q85=makeQuery(id+"F7.boolean.opBoolean","INTERSECT",EDGE,{"disambiguationData":[OD(0.0)],"derivedFrom":[makeQuery(id+"F1.opExtrude","SWEPT_FACE",FACE,{"disambiguationData":[OSD([sQuery(id+"F0.wireOp",EDGE,"E0")])]}),makeQuery(id+"F7.opExtrude","SWEPT_FACE",FACE,{"disambiguationData":[OSD([sQuery(id+"F6.wireOp",EDGE,"7a5957e4-cc16-4d21-8b24-b71f9a09db7a")])]})]});
            var Q86;
            Q86=makeQuery(id+"F7.boolean.opBoolean","INTERSECT",EDGE,{"disambiguationData":[OD(0.0)],"derivedFrom":[makeQuery(id+"F1.opExtrude","SWEPT_FACE",FACE,{"disambiguationData":[OSD([sQuery(id+"F0.wireOp",EDGE,"E0")])]}),makeQuery(id+"F7.opExtrude","SWEPT_FACE",FACE,{"disambiguationData":[OSD([sQuery(id+"F6.wireOp",EDGE,"f5a73cac-6e2b-4509-98b7-614c817debd5")])]})]});
            var Q87;
            Q87=makeQuery(id+"F7.boolean.opBoolean","INTERSECT",EDGE,{"disambiguationData":[OD(0.0)],"derivedFrom":[makeQuery(id+"F1.opExtrude","SWEPT_FACE",FACE,{"disambiguationData":[OSD([sQuery(id+"F0.wireOp",EDGE,"E0")])]}),makeQuery(id+"F7.opExtrude","SWEPT_FACE",FACE,{"disambiguationData":[OSD([sQuery(id+"F6.wireOp",EDGE,"3257f0e8-a14c-4f57-a5a9-66824f5aab70")])]})]});
            var Q88;
            Q88=makeQuery(id+"F7.boolean.opBoolean","INTERSECT",EDGE,{"disambiguationData":[OD(0.0)],"derivedFrom":[makeQuery(id+"F1.opExtrude","SWEPT_FACE",FACE,{"disambiguationData":[OSD([sQuery(id+"F0.wireOp",EDGE,"E0")])]}),makeQuery(id+"F7.opExtrude","SWEPT_FACE",FACE,{"disambiguationData":[OSD([sQuery(id+"F6.wireOp",EDGE,"ee405ad0-9952-4166-b40a-09788f6ddfb5")])]})]});
            var Q89;
            Q89=makeQuery(id+"F7.boolean.opBoolean","INTERSECT",EDGE,{"disambiguationData":[OD(0.0)],"derivedFrom":[makeQuery(id+"F1.opExtrude","SWEPT_FACE",FACE,{"disambiguationData":[OSD([sQuery(id+"F0.wireOp",EDGE,"E0")])]}),makeQuery(id+"F7.opExtrude","SWEPT_FACE",FACE,{"disambiguationData":[OSD([sQuery(id+"F6.wireOp",EDGE,"2fa87e37-a699-481d-8a24-3aeddef2e244")])]})]});
            var Q90;
            Q90=makeQuery(id+"F7.boolean.opBoolean","INTERSECT",EDGE,{"disambiguationData":[OD(0.0)],"derivedFrom":[makeQuery(id+"F1.opExtrude","SWEPT_FACE",FACE,{"disambiguationData":[OSD([sQuery(id+"F0.wireOp",EDGE,"E0")])]}),makeQuery(id+"F7.opExtrude","SWEPT_FACE",FACE,{"disambiguationData":[OSD([sQuery(id+"F6.wireOp",EDGE,"4cac9c55-7efd-43a6-b3a8-6db941ce081a")])]})]});
            var Q91;
            Q91=makeQuery(id+"F7.boolean.opBoolean","INTERSECT",EDGE,{"disambiguationData":[OD(0.0)],"derivedFrom":[makeQuery(id+"F1.opExtrude","SWEPT_FACE",FACE,{"disambiguationData":[OSD([sQuery(id+"F0.wireOp",EDGE,"E0")])]}),makeQuery(id+"F7.opExtrude","SWEPT_FACE",FACE,{"disambiguationData":[OSD([sQuery(id+"F6.wireOp",EDGE,"b7c61857-15d8-4b71-81a2-4fbbf24b3784")])]})]});
            var Q92;
            Q92=makeQuery(id+"F7.boolean.opBoolean","INTERSECT",EDGE,{"disambiguationData":[OD(0.0)],"derivedFrom":[makeQuery(id+"F1.opExtrude","SWEPT_FACE",FACE,{"disambiguationData":[OSD([sQuery(id+"F0.wireOp",EDGE,"E0")])]}),makeQuery(id+"F7.opExtrude","SWEPT_FACE",FACE,{"disambiguationData":[OSD([sQuery(id+"F6.wireOp",EDGE,"48937804-74be-4d1d-a780-8159de361928")])]})]});
            var Q93;
            Q93=makeQuery(id+"F7.boolean.opBoolean","INTERSECT",EDGE,{"disambiguationData":[OD(0.0)],"derivedFrom":[makeQuery(id+"F1.opExtrude","SWEPT_FACE",FACE,{"disambiguationData":[OSD([sQuery(id+"F0.wireOp",EDGE,"E0")])]}),makeQuery(id+"F7.opExtrude","SWEPT_FACE",FACE,{"disambiguationData":[OSD([sQuery(id+"F6.wireOp",EDGE,"f4b3b797-2859-490d-b7b5-c2bfef3c68df")])]})]});
            var Q94;
            Q94=makeQuery(id+"F7.boolean.opBoolean","INTERSECT",EDGE,{"disambiguationData":[OD(0.0)],"derivedFrom":[makeQuery(id+"F1.opExtrude","SWEPT_FACE",FACE,{"disambiguationData":[OSD([sQuery(id+"F0.wireOp",EDGE,"E0")])]}),makeQuery(id+"F7.opExtrude","SWEPT_FACE",FACE,{"disambiguationData":[OSD([sQuery(id+"F6.wireOp",EDGE,"1201f4c5-c131-4895-a1f1-c302d83bce6e")])]})]});
            var Q95;
            Q95=makeQuery(id+"F7.boolean.opBoolean","INTERSECT",EDGE,{"disambiguationData":[OD(0.0)],"derivedFrom":[makeQuery(id+"F1.opExtrude","SWEPT_FACE",FACE,{"disambiguationData":[OSD([sQuery(id+"F0.wireOp",EDGE,"E0")])]}),makeQuery(id+"F7.opExtrude","SWEPT_FACE",FACE,{"disambiguationData":[OSD([sQuery(id+"F6.wireOp",EDGE,"de09daf4-2825-49fb-a621-eb4d3bd58af1")])]})]});
            var Q96;
            Q96=makeQuery(id+"F7.boolean.opBoolean","INTERSECT",EDGE,{"disambiguationData":[OD(0.0)],"derivedFrom":[makeQuery(id+"F1.opExtrude","SWEPT_FACE",FACE,{"disambiguationData":[OSD([sQuery(id+"F0.wireOp",EDGE,"E0")])]}),makeQuery(id+"F7.opExtrude","SWEPT_FACE",FACE,{"disambiguationData":[OSD([sQuery(id+"F6.wireOp",EDGE,"2a262191-3a4f-451e-b395-dc7af2397be1")])]})]});
            var Q97;
            Q97=makeQuery(id+"F7.boolean.opBoolean","INTERSECT",EDGE,{"disambiguationData":[OD(0.0)],"derivedFrom":[makeQuery(id+"F1.opExtrude","SWEPT_FACE",FACE,{"disambiguationData":[OSD([sQuery(id+"F0.wireOp",EDGE,"E0")])]}),makeQuery(id+"F7.opExtrude","SWEPT_FACE",FACE,{"disambiguationData":[OSD([sQuery(id+"F6.wireOp",EDGE,"9832b7fa-ab71-4669-b3d5-036fdeb69183")])]})]});
            var Q98;
            Q98=makeQuery(id+"F7.boolean.opBoolean","INTERSECT",EDGE,{"disambiguationData":[OD(0.0)],"derivedFrom":[makeQuery(id+"F1.opExtrude","SWEPT_FACE",FACE,{"disambiguationData":[OSD([sQuery(id+"F0.wireOp",EDGE,"E0")])]}),makeQuery(id+"F7.opExtrude","SWEPT_FACE",FACE,{"disambiguationData":[OSD([sQuery(id+"F6.wireOp",EDGE,"5a534d87-88aa-4def-9ebb-4f3525dad718")])]})]});
            var Q99;
            Q99=makeQuery(id+"F7.boolean.opBoolean","INTERSECT",EDGE,{"disambiguationData":[OD(0.0)],"derivedFrom":[makeQuery(id+"F1.opExtrude","SWEPT_FACE",FACE,{"disambiguationData":[OSD([sQuery(id+"F0.wireOp",EDGE,"E0")])]}),makeQuery(id+"F7.opExtrude","SWEPT_FACE",FACE,{"disambiguationData":[OSD([sQuery(id+"F6.wireOp",EDGE,"af5d01d9-e0bb-42d4-a9e9-53d224fa13c4")])]})]});
            var Q100;
            Q100=makeQuery(id+"F7.boolean.opBoolean","INTERSECT",EDGE,{"disambiguationData":[OD(0.0)],"derivedFrom":[makeQuery(id+"F1.opExtrude","SWEPT_FACE",FACE,{"disambiguationData":[OSD([sQuery(id+"F0.wireOp",EDGE,"E0")])]}),makeQuery(id+"F7.opExtrude","SWEPT_FACE",FACE,{"disambiguationData":[OSD([sQuery(id+"F6.wireOp",EDGE,"63af3750-506c-4288-83c5-8929affd3ff9")])]})]});
            var Q101;
            Q101=makeQuery(id+"F7.boolean.opBoolean","INTERSECT",EDGE,{"disambiguationData":[OD(0.0)],"derivedFrom":[makeQuery(id+"F1.opExtrude","SWEPT_FACE",FACE,{"disambiguationData":[OSD([sQuery(id+"F0.wireOp",EDGE,"E0")])]}),makeQuery(id+"F7.opExtrude","SWEPT_FACE",FACE,{"disambiguationData":[OSD([sQuery(id+"F6.wireOp",EDGE,"2db1c546-a54b-418f-a515-398807a46512")])]})]});
            var Q102;
            Q102=makeQuery(id+"F10.boolean.opBoolean","INTERSECT",EDGE,{"disambiguationData":[OD(0.0)],"derivedFrom":[makeQuery(id+"F1.opExtrude","SWEPT_FACE",FACE,{"disambiguationData":[OSD([sQuery(id+"F0.wireOp",EDGE,"E0")])]}),makeQuery(id+"F10.opExtrude","SWEPT_FACE",FACE,{"disambiguationData":[OSD([sQuery(id+"F9.wireOp",EDGE,"429d95a1-3c8a-48cf-b1fd-65ae80db6ffc")])]})]});
            var Q103;
            Q103=makeQuery(id+"F10.boolean.opBoolean","INTERSECT",EDGE,{"disambiguationData":[OD(0.0)],"derivedFrom":[makeQuery(id+"F1.opExtrude","SWEPT_FACE",FACE,{"disambiguationData":[OSD([sQuery(id+"F0.wireOp",EDGE,"E0")])]}),makeQuery(id+"F10.opExtrude","SWEPT_FACE",FACE,{"disambiguationData":[OSD([sQuery(id+"F9.wireOp",EDGE,"88dc3317-14d6-4f39-a813-642e505b3db3")])]})]});
            var Q104;
            Q104=makeQuery(id+"F10.boolean.opBoolean","INTERSECT",EDGE,{"disambiguationData":[OD(0.0)],"derivedFrom":[makeQuery(id+"F1.opExtrude","SWEPT_FACE",FACE,{"disambiguationData":[OSD([sQuery(id+"F0.wireOp",EDGE,"E0")])]}),makeQuery(id+"F10.opExtrude","SWEPT_FACE",FACE,{"disambiguationData":[OSD([sQuery(id+"F9.wireOp",EDGE,"c61f0de6-50a4-4502-a890-74c6c6ac1cd3")])]})]});
            var Q105;
            Q105=makeQuery(id+"F10.boolean.opBoolean","INTERSECT",EDGE,{"disambiguationData":[OD(0.0)],"derivedFrom":[makeQuery(id+"F1.opExtrude","SWEPT_FACE",FACE,{"disambiguationData":[OSD([sQuery(id+"F0.wireOp",EDGE,"E0")])]}),makeQuery(id+"F10.opExtrude","SWEPT_FACE",FACE,{"disambiguationData":[OSD([sQuery(id+"F9.wireOp",EDGE,"479dec23-3f8f-44ee-8e45-d2b113d31b07")])]})]});
            var Q106;
            Q106=makeQuery(id+"F10.boolean.opBoolean","INTERSECT",EDGE,{"disambiguationData":[OD(0.0)],"derivedFrom":[makeQuery(id+"F1.opExtrude","SWEPT_FACE",FACE,{"disambiguationData":[OSD([sQuery(id+"F0.wireOp",EDGE,"E0")])]}),makeQuery(id+"F10.opExtrude","SWEPT_FACE",FACE,{"disambiguationData":[OSD([sQuery(id+"F9.wireOp",EDGE,"fce1ec24-8c70-45cc-92f2-20edd6db3c88")])]})]});
            var Q107;
            Q107=makeQuery(id+"F10.boolean.opBoolean","INTERSECT",EDGE,{"disambiguationData":[OD(0.0)],"derivedFrom":[makeQuery(id+"F1.opExtrude","SWEPT_FACE",FACE,{"disambiguationData":[OSD([sQuery(id+"F0.wireOp",EDGE,"E0")])]}),makeQuery(id+"F10.opExtrude","SWEPT_FACE",FACE,{"disambiguationData":[OSD([sQuery(id+"F9.wireOp",EDGE,"0975aea8-55f6-417d-8d6b-6ad5a96ef988")])]})]});
            var Q108;
            Q108=makeQuery(id+"F10.boolean.opBoolean","INTERSECT",EDGE,{"disambiguationData":[OD(0.0)],"derivedFrom":[makeQuery(id+"F1.opExtrude","SWEPT_FACE",FACE,{"disambiguationData":[OSD([sQuery(id+"F0.wireOp",EDGE,"E0")])]}),makeQuery(id+"F10.opExtrude","SWEPT_FACE",FACE,{"disambiguationData":[OSD([sQuery(id+"F9.wireOp",EDGE,"e0e213fe-66f1-429b-aeb4-bda37cd8a542")])]})]});
            var Q109;
            Q109=makeQuery(id+"F10.boolean.opBoolean","INTERSECT",EDGE,{"disambiguationData":[OD(0.0)],"derivedFrom":[makeQuery(id+"F1.opExtrude","SWEPT_FACE",FACE,{"disambiguationData":[OSD([sQuery(id+"F0.wireOp",EDGE,"E0")])]}),makeQuery(id+"F10.opExtrude","SWEPT_FACE",FACE,{"disambiguationData":[OSD([sQuery(id+"F9.wireOp",EDGE,"OpU4Ypz6-Hcb8-YkKV-7chd-lZCeiZS7tYYF")])]})]});
            var Q110;
            Q110=makeQuery(id+"F10.boolean.opBoolean","INTERSECT",EDGE,{"disambiguationData":[OD(0.0)],"derivedFrom":[makeQuery(id+"F1.opExtrude","SWEPT_FACE",FACE,{"disambiguationData":[OSD([sQuery(id+"F0.wireOp",EDGE,"E0")])]}),makeQuery(id+"F10.opExtrude","SWEPT_FACE",FACE,{"disambiguationData":[OSD([sQuery(id+"F9.wireOp",EDGE,"7meaahbg-dbg3-uSPd-PEJJ-e7DtyzYx0gQt"),sQuery(id+"F9.wireOp",EDGE,"vEAYXyeL-ay2Z-WL7a-7Ha5-VfRoazVvpcCo")])]})]});
            var Q111;
            Q111=makeQuery(id+"F10.boolean.opBoolean","INTERSECT",EDGE,{"disambiguationData":[OD(0.0)],"derivedFrom":[makeQuery(id+"F1.opExtrude","SWEPT_FACE",FACE,{"disambiguationData":[OSD([sQuery(id+"F0.wireOp",EDGE,"E0")])]}),makeQuery(id+"F10.opExtrude","SWEPT_FACE",FACE,{"disambiguationData":[OSD([sQuery(id+"F9.wireOp",EDGE,"1QEsIIjE-87yi-7XXF-o0p4-XyzEA0SBXInf")])]})]});
            var Q112;
            Q112=makeQuery(id+"F10.boolean.opBoolean","INTERSECT",EDGE,{"disambiguationData":[OD(0.0)],"derivedFrom":[makeQuery(id+"F1.opExtrude","SWEPT_FACE",FACE,{"disambiguationData":[OSD([sQuery(id+"F0.wireOp",EDGE,"E0")])]}),makeQuery(id+"F10.opExtrude","SWEPT_FACE",FACE,{"disambiguationData":[OSD([sQuery(id+"F9.wireOp",EDGE,"4fa15834-391d-4db3-8b3b-82f9d2034739")])]})]});
            var Q113;
            Q113=makeQuery(id+"F10.boolean.opBoolean","INTERSECT",EDGE,{"disambiguationData":[OD(0.0)],"derivedFrom":[makeQuery(id+"F1.opExtrude","SWEPT_FACE",FACE,{"disambiguationData":[OSD([sQuery(id+"F0.wireOp",EDGE,"E0")])]}),makeQuery(id+"F10.opExtrude","SWEPT_FACE",FACE,{"disambiguationData":[OSD([sQuery(id+"F9.wireOp",EDGE,"cf1de00f-3169-4f70-98fb-b7290205bd4b")])]})]});
            var Q114;
            Q114=makeQuery(id+"F10.boolean.opBoolean","INTERSECT",EDGE,{"disambiguationData":[OD(0.0)],"derivedFrom":[makeQuery(id+"F1.opExtrude","SWEPT_FACE",FACE,{"disambiguationData":[OSD([sQuery(id+"F0.wireOp",EDGE,"E0")])]}),makeQuery(id+"F10.opExtrude","SWEPT_FACE",FACE,{"disambiguationData":[OSD([sQuery(id+"F9.wireOp",EDGE,"e82f161c-c8f9-431a-b111-592f8292c69f")])]})]});
            var Q115;
            Q115=makeQuery(id+"F10.boolean.opBoolean","INTERSECT",EDGE,{"disambiguationData":[OD(0.0)],"derivedFrom":[makeQuery(id+"F1.opExtrude","SWEPT_FACE",FACE,{"disambiguationData":[OSD([sQuery(id+"F0.wireOp",EDGE,"E0")])]}),makeQuery(id+"F10.opExtrude","SWEPT_FACE",FACE,{"disambiguationData":[OSD([sQuery(id+"F9.wireOp",EDGE,"17f8cebd-a2bc-4d80-8a13-7e07ce9ceaf0")])]})]});
            var Q116;
            Q116=makeQuery(id+"F10.boolean.opBoolean","INTERSECT",EDGE,{"disambiguationData":[OD(0.0)],"derivedFrom":[makeQuery(id+"F1.opExtrude","SWEPT_FACE",FACE,{"disambiguationData":[OSD([sQuery(id+"F0.wireOp",EDGE,"E0")])]}),makeQuery(id+"F10.opExtrude","SWEPT_FACE",FACE,{"disambiguationData":[OSD([sQuery(id+"F9.wireOp",EDGE,"4653122c-81e7-43b8-a175-0e9b4399c1dd")])]})]});
            var Q117;
            Q117=makeQuery(id+"F10.boolean.opBoolean","INTERSECT",EDGE,{"disambiguationData":[OD(0.0)],"derivedFrom":[makeQuery(id+"F1.opExtrude","SWEPT_FACE",FACE,{"disambiguationData":[OSD([sQuery(id+"F0.wireOp",EDGE,"E0")])]}),makeQuery(id+"F10.opExtrude","SWEPT_FACE",FACE,{"disambiguationData":[OSD([sQuery(id+"F9.wireOp",EDGE,"f7332d99-994a-4820-91d6-0eb80c66d826")])]})]});
            var Q118;
            Q118=makeQuery(id+"F10.boolean.opBoolean","INTERSECT",EDGE,{"disambiguationData":[OD(0.0)],"derivedFrom":[makeQuery(id+"F1.opExtrude","SWEPT_FACE",FACE,{"disambiguationData":[OSD([sQuery(id+"F0.wireOp",EDGE,"E0")])]}),makeQuery(id+"F10.opExtrude","SWEPT_FACE",FACE,{"disambiguationData":[OSD([sQuery(id+"F9.wireOp",EDGE,"917abea8-5958-4d13-b49a-d9c63b39efb4")])]})]});
            var Q119;
            Q119=makeQuery(id+"F10.boolean.opBoolean","INTERSECT",EDGE,{"disambiguationData":[OD(0.0)],"derivedFrom":[makeQuery(id+"F1.opExtrude","SWEPT_FACE",FACE,{"disambiguationData":[OSD([sQuery(id+"F0.wireOp",EDGE,"E0")])]}),makeQuery(id+"F10.opExtrude","SWEPT_FACE",FACE,{"disambiguationData":[OSD([sQuery(id+"F9.wireOp",EDGE,"5ad42132-cac8-4035-b0a1-ce6f07b595eb")])]})]});
            var Q120;
            Q120=makeQuery(id+"F10.boolean.opBoolean","INTERSECT",EDGE,{"disambiguationData":[OD(0.0)],"derivedFrom":[makeQuery(id+"F1.opExtrude","SWEPT_FACE",FACE,{"disambiguationData":[OSD([sQuery(id+"F0.wireOp",EDGE,"E0")])]}),makeQuery(id+"F10.opExtrude","SWEPT_FACE",FACE,{"disambiguationData":[OSD([sQuery(id+"F9.wireOp",EDGE,"423f58d8-1f19-46c3-b5b6-1235c5f2b6ac")])]})]});
            var Q121;
            Q121=makeQuery(id+"F10.boolean.opBoolean","INTERSECT",EDGE,{"disambiguationData":[OD(0.0)],"derivedFrom":[makeQuery(id+"F1.opExtrude","SWEPT_FACE",FACE,{"disambiguationData":[OSD([sQuery(id+"F0.wireOp",EDGE,"E0")])]}),makeQuery(id+"F10.opExtrude","SWEPT_FACE",FACE,{"disambiguationData":[OSD([sQuery(id+"F9.wireOp",EDGE,"a8de5c63-b59d-4111-aaf0-c59ceeb84539")])]})]});
            var Q122;
            Q122=makeQuery(id+"F10.boolean.opBoolean","INTERSECT",EDGE,{"disambiguationData":[OD(0.0)],"derivedFrom":[makeQuery(id+"F1.opExtrude","SWEPT_FACE",FACE,{"disambiguationData":[OSD([sQuery(id+"F0.wireOp",EDGE,"E0")])]}),makeQuery(id+"F10.opExtrude","SWEPT_FACE",FACE,{"disambiguationData":[OSD([sQuery(id+"F9.wireOp",EDGE,"43266347-99e5-4a65-87d8-d68d1b57105e")])]})]});
            var Q123;
            Q123=makeQuery(id+"F10.boolean.opBoolean","INTERSECT",EDGE,{"disambiguationData":[OD(0.0)],"derivedFrom":[makeQuery(id+"F1.opExtrude","SWEPT_FACE",FACE,{"disambiguationData":[OSD([sQuery(id+"F0.wireOp",EDGE,"E0")])]}),makeQuery(id+"F10.opExtrude","SWEPT_FACE",FACE,{"disambiguationData":[OSD([sQuery(id+"F9.wireOp",EDGE,"2193aa8a-cfb0-48d0-87fc-1cfe83a7fd52")])]})]});
            var Q124;
            Q124=makeQuery(id+"F10.boolean.opBoolean","INTERSECT",EDGE,{"disambiguationData":[OD(0.0)],"derivedFrom":[makeQuery(id+"F1.opExtrude","SWEPT_FACE",FACE,{"disambiguationData":[OSD([sQuery(id+"F0.wireOp",EDGE,"E0")])]}),makeQuery(id+"F10.opExtrude","SWEPT_FACE",FACE,{"disambiguationData":[OSD([sQuery(id+"F9.wireOp",EDGE,"589360f9-4b1b-47cd-a11b-2a67260c207c")])]})]});
            var Q125;
            Q125=makeQuery(id+"F10.boolean.opBoolean","INTERSECT",EDGE,{"disambiguationData":[OD(0.0)],"derivedFrom":[makeQuery(id+"F1.opExtrude","SWEPT_FACE",FACE,{"disambiguationData":[OSD([sQuery(id+"F0.wireOp",EDGE,"E0")])]}),makeQuery(id+"F10.opExtrude","SWEPT_FACE",FACE,{"disambiguationData":[OSD([sQuery(id+"F9.wireOp",EDGE,"d7004727-f34f-4852-a492-ed529d9aa36c")])]})]});
            var Q126;
            Q126=makeQuery(id+"F10.boolean.opBoolean","INTERSECT",EDGE,{"disambiguationData":[OD(0.0)],"derivedFrom":[makeQuery(id+"F1.opExtrude","SWEPT_FACE",FACE,{"disambiguationData":[OSD([sQuery(id+"F0.wireOp",EDGE,"E0")])]}),makeQuery(id+"F10.opExtrude","SWEPT_FACE",FACE,{"disambiguationData":[OSD([sQuery(id+"F9.wireOp",EDGE,"b6c25ba9-2617-4775-a0b3-41ef528efab6")])]})]});
            var Q127;
            Q127=makeQuery(id+"F10.boolean.opBoolean","INTERSECT",EDGE,{"disambiguationData":[OD(0.0)],"derivedFrom":[makeQuery(id+"F1.opExtrude","SWEPT_FACE",FACE,{"disambiguationData":[OSD([sQuery(id+"F0.wireOp",EDGE,"E0")])]}),makeQuery(id+"F10.opExtrude","SWEPT_FACE",FACE,{"disambiguationData":[OSD([sQuery(id+"F9.wireOp",EDGE,"0749a5eb-1656-439a-a869-05d76e53423e")])]})]});
            var Q128;
            Q128=makeQuery(id+"F10.boolean.opBoolean","INTERSECT",EDGE,{"disambiguationData":[OD(0.0)],"derivedFrom":[makeQuery(id+"F1.opExtrude","SWEPT_FACE",FACE,{"disambiguationData":[OSD([sQuery(id+"F0.wireOp",EDGE,"E0")])]}),makeQuery(id+"F10.opExtrude","SWEPT_FACE",FACE,{"disambiguationData":[OSD([sQuery(id+"F9.wireOp",EDGE,"8357bcdf-6207-4d5b-93da-fad6725d465d")])]})]});
            var Q129;
            Q129=makeQuery(id+"F10.boolean.opBoolean","INTERSECT",EDGE,{"disambiguationData":[OD(0.0)],"derivedFrom":[makeQuery(id+"F1.opExtrude","SWEPT_FACE",FACE,{"disambiguationData":[OSD([sQuery(id+"F0.wireOp",EDGE,"E0")])]}),makeQuery(id+"F10.opExtrude","SWEPT_FACE",FACE,{"disambiguationData":[OSD([sQuery(id+"F9.wireOp",EDGE,"c678ade0-3d66-4aad-85d1-643d7c5f28b6")])]})]});
            var Q130;
            Q130=makeQuery(id+"F7.boolean.opBoolean","INTERSECT",EDGE,{"disambiguationData":[OD(0.0)],"derivedFrom":[makeQuery(id+"F1.opExtrude","SWEPT_FACE",FACE,{"disambiguationData":[OSD([sQuery(id+"F0.wireOp",EDGE,"E0")])]}),makeQuery(id+"F7.opExtrude","SWEPT_FACE",FACE,{"disambiguationData":[OSD([sQuery(id+"F6.wireOp",EDGE,"31c7d22c-81f8-4662-bd11-6a8b92b7cb61")])]})]});
            var Q131;
            Q131=makeQuery(id+"F7.boolean.opBoolean","INTERSECT",EDGE,{"disambiguationData":[OD(0.0)],"derivedFrom":[makeQuery(id+"F1.opExtrude","SWEPT_FACE",FACE,{"disambiguationData":[OSD([sQuery(id+"F0.wireOp",EDGE,"E0")])]}),makeQuery(id+"F7.opExtrude","SWEPT_FACE",FACE,{"disambiguationData":[OSD([sQuery(id+"F6.wireOp",EDGE,"9760f720-9e2d-42e7-b9e9-8ad347021829")])]})]});
            var Q132;
            Q132=makeQuery(id+"F7.boolean.opBoolean","INTERSECT",EDGE,{"disambiguationData":[OD(0.0)],"derivedFrom":[makeQuery(id+"F1.opExtrude","SWEPT_FACE",FACE,{"disambiguationData":[OSD([sQuery(id+"F0.wireOp",EDGE,"E0")])]}),makeQuery(id+"F7.opExtrude","SWEPT_FACE",FACE,{"disambiguationData":[OSD([sQuery(id+"F6.wireOp",EDGE,"f669afdf-d7ad-41c0-aa00-2f38db0ae71b")])]})]});
            var Q133;
            Q133=makeQuery(id+"F7.boolean.opBoolean","INTERSECT",EDGE,{"disambiguationData":[OD(0.0)],"derivedFrom":[makeQuery(id+"F1.opExtrude","SWEPT_FACE",FACE,{"disambiguationData":[OSD([sQuery(id+"F0.wireOp",EDGE,"E0")])]}),makeQuery(id+"F7.opExtrude","SWEPT_FACE",FACE,{"disambiguationData":[OSD([sQuery(id+"F6.wireOp",EDGE,"27ce2371-831d-4e51-9e08-e601952e9ea9")])]})]});
            var Q134;
            Q134=makeQuery(id+"F7.boolean.opBoolean","INTERSECT",EDGE,{"disambiguationData":[OD(0.0)],"derivedFrom":[makeQuery(id+"F1.opExtrude","SWEPT_FACE",FACE,{"disambiguationData":[OSD([sQuery(id+"F0.wireOp",EDGE,"E0")])]}),makeQuery(id+"F7.opExtrude","SWEPT_FACE",FACE,{"disambiguationData":[OSD([sQuery(id+"F6.wireOp",EDGE,"e27b1b56-f1a0-4449-8924-ff9f4a1ebb5a")])]})]});
            var Q135;
            Q135=makeQuery(id+"F10.boolean.opBoolean","INTERSECT",EDGE,{"disambiguationData":[OD(0.0)],"derivedFrom":[makeQuery(id+"F1.opExtrude","SWEPT_FACE",FACE,{"disambiguationData":[OSD([sQuery(id+"F0.wireOp",EDGE,"E0")])]}),makeQuery(id+"F10.opExtrude","SWEPT_FACE",FACE,{"disambiguationData":[OSD([sQuery(id+"F9.wireOp",EDGE,"bc574ee6-e8d7-4402-b7bf-a31d76de5201")])]})]});
            var Q136;
            Q136=makeQuery(id+"F10.boolean.opBoolean","INTERSECT",EDGE,{"disambiguationData":[OD(0.0)],"derivedFrom":[makeQuery(id+"F1.opExtrude","SWEPT_FACE",FACE,{"disambiguationData":[OSD([sQuery(id+"F0.wireOp",EDGE,"E0")])]}),makeQuery(id+"F10.opExtrude","SWEPT_FACE",FACE,{"disambiguationData":[OSD([sQuery(id+"F9.wireOp",EDGE,"34f3141e-2481-4cad-a724-18fe9355e9ac")])]})]});
            var Q137;
            Q137=makeQuery(id+"F10.boolean.opBoolean","INTERSECT",EDGE,{"disambiguationData":[OD(0.0)],"derivedFrom":[makeQuery(id+"F1.opExtrude","SWEPT_FACE",FACE,{"disambiguationData":[OSD([sQuery(id+"F0.wireOp",EDGE,"E0")])]}),makeQuery(id+"F10.opExtrude","SWEPT_FACE",FACE,{"disambiguationData":[OSD([sQuery(id+"F9.wireOp",EDGE,"6dc2a6c8-a69d-41e3-9ee2-05e60369f11b")])]})]});
            var Q138;
            Q138=makeQuery(id+"F10.boolean.opBoolean","INTERSECT",EDGE,{"disambiguationData":[OD(0.0)],"derivedFrom":[makeQuery(id+"F1.opExtrude","SWEPT_FACE",FACE,{"disambiguationData":[OSD([sQuery(id+"F0.wireOp",EDGE,"E0")])]}),makeQuery(id+"F10.opExtrude","SWEPT_FACE",FACE,{"disambiguationData":[OSD([sQuery(id+"F9.wireOp",EDGE,"2db869a3-9406-4888-bcbb-00bb43a69eba")])]})]});
            var Q139;
            Q139=makeQuery(id+"F10.boolean.opBoolean","INTERSECT",EDGE,{"disambiguationData":[OD(0.0)],"derivedFrom":[makeQuery(id+"F1.opExtrude","SWEPT_FACE",FACE,{"disambiguationData":[OSD([sQuery(id+"F0.wireOp",EDGE,"E0")])]}),makeQuery(id+"F10.opExtrude","SWEPT_FACE",FACE,{"disambiguationData":[OSD([sQuery(id+"F9.wireOp",EDGE,"7b437f7c-4576-4f11-8c60-76c3eb11ba37")])]})]});
            var Q140;
            Q140=makeQuery(id+"F10.boolean.opBoolean","INTERSECT",EDGE,{"disambiguationData":[OD(0.0)],"derivedFrom":[makeQuery(id+"F1.opExtrude","SWEPT_FACE",FACE,{"disambiguationData":[OSD([sQuery(id+"F0.wireOp",EDGE,"E0")])]}),makeQuery(id+"F10.opExtrude","SWEPT_FACE",FACE,{"disambiguationData":[OSD([sQuery(id+"F9.wireOp",EDGE,"7bb27c30-01e1-4c30-9b62-d81abe0e1569")])]})]});
            var Q141;
            Q141=makeQuery(id+"F7.boolean.opBoolean","INTERSECT",EDGE,{"disambiguationData":[OD(0.0)],"derivedFrom":[makeQuery(id+"F1.opExtrude","SWEPT_FACE",FACE,{"disambiguationData":[OSD([sQuery(id+"F0.wireOp",EDGE,"E0")])]}),makeQuery(id+"F7.opExtrude","SWEPT_FACE",FACE,{"disambiguationData":[OSD([sQuery(id+"F6.wireOp",EDGE,"93935017-728a-4f1c-903b-dfa4ee534358")])]})]});
            var Q142;
            Q142=makeQuery(id+"F7.boolean.opBoolean","INTERSECT",EDGE,{"disambiguationData":[OD(0.0)],"derivedFrom":[makeQuery(id+"F1.opExtrude","SWEPT_FACE",FACE,{"disambiguationData":[OSD([sQuery(id+"F0.wireOp",EDGE,"E0")])]}),makeQuery(id+"F7.opExtrude","SWEPT_FACE",FACE,{"disambiguationData":[OSD([sQuery(id+"F6.wireOp",EDGE,"1be80a28-2c43-4fd4-89f8-f32c44110b3f")])]})]});
            var Q143;
            Q143=makeQuery(id+"F7.boolean.opBoolean","INTERSECT",EDGE,{"disambiguationData":[OD(0.0)],"derivedFrom":[makeQuery(id+"F1.opExtrude","SWEPT_FACE",FACE,{"disambiguationData":[OSD([sQuery(id+"F0.wireOp",EDGE,"E0")])]}),makeQuery(id+"F7.opExtrude","SWEPT_FACE",FACE,{"disambiguationData":[OSD([sQuery(id+"F6.wireOp",EDGE,"bd02c535-79a8-436b-9978-bd3653fcbfbf")])]})]});
            var Q144;
            Q144=makeQuery(id+"F7.boolean.opBoolean","INTERSECT",EDGE,{"disambiguationData":[OD(0.0)],"derivedFrom":[makeQuery(id+"F1.opExtrude","SWEPT_FACE",FACE,{"disambiguationData":[OSD([sQuery(id+"F0.wireOp",EDGE,"E0")])]}),makeQuery(id+"F7.opExtrude","SWEPT_FACE",FACE,{"disambiguationData":[OSD([sQuery(id+"F6.wireOp",EDGE,"8923652c-60ee-40cc-b4c6-e39304594786")])]})]});
            var Q145;
            Q145=makeQuery(id+"F7.boolean.opBoolean","INTERSECT",EDGE,{"disambiguationData":[OD(0.0)],"derivedFrom":[makeQuery(id+"F1.opExtrude","SWEPT_FACE",FACE,{"disambiguationData":[OSD([sQuery(id+"F0.wireOp",EDGE,"E0")])]}),makeQuery(id+"F7.opExtrude","SWEPT_FACE",FACE,{"disambiguationData":[OSD([sQuery(id+"F6.wireOp",EDGE,"a1de85a8-8a62-40c6-b726-1736eda7a2da")])]})]});
            var Q146;
            Q146=makeQuery(id+"F7.boolean.opBoolean","INTERSECT",EDGE,{"disambiguationData":[OD(0.0)],"derivedFrom":[makeQuery(id+"F1.opExtrude","SWEPT_FACE",FACE,{"disambiguationData":[OSD([sQuery(id+"F0.wireOp",EDGE,"E0")])]}),makeQuery(id+"F7.opExtrude","SWEPT_FACE",FACE,{"disambiguationData":[OSD([sQuery(id+"F6.wireOp",EDGE,"5c94e7fe-7667-4b5c-a899-a170bc688a63")])]})]});
            var Q147;
            Q147=makeQuery(id+"F10.boolean.opBoolean","INTERSECT",EDGE,{"disambiguationData":[OD(0.0)],"derivedFrom":[makeQuery(id+"F1.opExtrude","SWEPT_FACE",FACE,{"disambiguationData":[OSD([sQuery(id+"F0.wireOp",EDGE,"E0")])]}),makeQuery(id+"F10.opExtrude","SWEPT_FACE",FACE,{"disambiguationData":[OSD([sQuery(id+"F9.wireOp",EDGE,"ad162529-5cfe-4944-83b4-e317f5486a3e")])]})]});
            var Q148;
            Q148=makeQuery(id+"F10.boolean.opBoolean","INTERSECT",EDGE,{"disambiguationData":[OD(0.0)],"derivedFrom":[makeQuery(id+"F1.opExtrude","SWEPT_FACE",FACE,{"disambiguationData":[OSD([sQuery(id+"F0.wireOp",EDGE,"E0")])]}),makeQuery(id+"F10.opExtrude","SWEPT_FACE",FACE,{"disambiguationData":[OSD([sQuery(id+"F9.wireOp",EDGE,"68b86c13-7ece-4168-b183-e17e549264ea")])]})]});
            var Q149;
            Q149=makeQuery(id+"F10.boolean.opBoolean","INTERSECT",EDGE,{"disambiguationData":[OD(0.0)],"derivedFrom":[makeQuery(id+"F1.opExtrude","SWEPT_FACE",FACE,{"disambiguationData":[OSD([sQuery(id+"F0.wireOp",EDGE,"E0")])]}),makeQuery(id+"F10.opExtrude","SWEPT_FACE",FACE,{"disambiguationData":[OSD([sQuery(id+"F9.wireOp",EDGE,"b2bf0872-2c35-4f65-a834-23150e7e820b")])]})]});
            var Q150;
            Q150=makeQuery(id+"F10.boolean.opBoolean","INTERSECT",EDGE,{"disambiguationData":[OD(0.0)],"derivedFrom":[makeQuery(id+"F1.opExtrude","SWEPT_FACE",FACE,{"disambiguationData":[OSD([sQuery(id+"F0.wireOp",EDGE,"E0")])]}),makeQuery(id+"F10.opExtrude","SWEPT_FACE",FACE,{"disambiguationData":[OSD([sQuery(id+"F9.wireOp",EDGE,"8715a638-6380-49e4-8166-a35da90eea4d")])]})]});
            var Q151;
            Q151=makeQuery(id+"F10.boolean.opBoolean","INTERSECT",EDGE,{"disambiguationData":[OD(0.0)],"derivedFrom":[makeQuery(id+"F1.opExtrude","SWEPT_FACE",FACE,{"disambiguationData":[OSD([sQuery(id+"F0.wireOp",EDGE,"E0")])]}),makeQuery(id+"F10.opExtrude","SWEPT_FACE",FACE,{"disambiguationData":[OSD([sQuery(id+"F9.wireOp",EDGE,"1193cbdb-8a08-404e-b46e-3bccfaa25342")])]})]});
            var Q152;
            Q152=makeQuery(id+"F10.boolean.opBoolean","INTERSECT",EDGE,{"disambiguationData":[OD(0.0)],"derivedFrom":[makeQuery(id+"F1.opExtrude","SWEPT_FACE",FACE,{"disambiguationData":[OSD([sQuery(id+"F0.wireOp",EDGE,"E0")])]}),makeQuery(id+"F10.opExtrude","SWEPT_FACE",FACE,{"disambiguationData":[OSD([sQuery(id+"F9.wireOp",EDGE,"9310307e-7862-42e2-8ad8-274fad6d12ca")])]})]});
            var Q153;
            Q153=makeQuery(id+"F7.boolean.opBoolean","INTERSECT",EDGE,{"disambiguationData":[OD(0.0)],"derivedFrom":[makeQuery(id+"F1.opExtrude","SWEPT_FACE",FACE,{"disambiguationData":[OSD([sQuery(id+"F0.wireOp",EDGE,"E0")])]}),makeQuery(id+"F7.opExtrude","SWEPT_FACE",FACE,{"disambiguationData":[OSD([sQuery(id+"F6.wireOp",EDGE,"a7bcfd16-c37a-45c4-b358-1ae0edba8923")])]})]});
            var Q154;
            Q154=makeQuery(id+"F7.boolean.opBoolean","INTERSECT",EDGE,{"disambiguationData":[OD(0.0)],"derivedFrom":[makeQuery(id+"F1.opExtrude","SWEPT_FACE",FACE,{"disambiguationData":[OSD([sQuery(id+"F0.wireOp",EDGE,"E0")])]}),makeQuery(id+"F7.opExtrude","SWEPT_FACE",FACE,{"disambiguationData":[OSD([sQuery(id+"F6.wireOp",EDGE,"ccd121b1-441a-4014-95ef-4c36e07d2233")])]})]});
            var Q155;
            Q155=makeQuery(id+"F7.boolean.opBoolean","INTERSECT",EDGE,{"disambiguationData":[OD(0.0)],"derivedFrom":[makeQuery(id+"F1.opExtrude","SWEPT_FACE",FACE,{"disambiguationData":[OSD([sQuery(id+"F0.wireOp",EDGE,"E0")])]}),makeQuery(id+"F7.opExtrude","SWEPT_FACE",FACE,{"disambiguationData":[OSD([sQuery(id+"F6.wireOp",EDGE,"1a29ebeb-8835-42a1-b92c-50c246a9d529")])]})]});
            var Q156;
            Q156=makeQuery(id+"F7.boolean.opBoolean","INTERSECT",EDGE,{"disambiguationData":[OD(0.0)],"derivedFrom":[makeQuery(id+"F1.opExtrude","SWEPT_FACE",FACE,{"disambiguationData":[OSD([sQuery(id+"F0.wireOp",EDGE,"E0")])]}),makeQuery(id+"F7.opExtrude","SWEPT_FACE",FACE,{"disambiguationData":[OSD([sQuery(id+"F6.wireOp",EDGE,"b31f20a5-7ea0-4ac5-bdea-8d9f319a5f5b")])]})]});
            var Q157;
            Q157=makeQuery(id+"F7.boolean.opBoolean","INTERSECT",EDGE,{"disambiguationData":[OD(0.0)],"derivedFrom":[makeQuery(id+"F1.opExtrude","SWEPT_FACE",FACE,{"disambiguationData":[OSD([sQuery(id+"F0.wireOp",EDGE,"E0")])]}),makeQuery(id+"F7.opExtrude","SWEPT_FACE",FACE,{"disambiguationData":[OSD([sQuery(id+"F6.wireOp",EDGE,"066ffb92-3af2-4bb7-b7a5-d42d1a48a872")])]})]});
            var Q158;
            Q158=makeQuery(id+"F7.boolean.opBoolean","INTERSECT",EDGE,{"disambiguationData":[OD(0.0)],"derivedFrom":[makeQuery(id+"F1.opExtrude","SWEPT_FACE",FACE,{"disambiguationData":[OSD([sQuery(id+"F0.wireOp",EDGE,"E0")])]}),makeQuery(id+"F7.opExtrude","SWEPT_FACE",FACE,{"disambiguationData":[OSD([sQuery(id+"F6.wireOp",EDGE,"ced44ab8-ddc7-4aad-977b-2de9040397a9")])]})]});
            var Q159;
            Q159=makeQuery(id+"F10.boolean.opBoolean","INTERSECT",EDGE,{"disambiguationData":[OD(0.0)],"derivedFrom":[makeQuery(id+"F1.opExtrude","SWEPT_FACE",FACE,{"disambiguationData":[OSD([sQuery(id+"F0.wireOp",EDGE,"E0")])]}),makeQuery(id+"F10.opExtrude","SWEPT_FACE",FACE,{"disambiguationData":[OSD([sQuery(id+"F9.wireOp",EDGE,"E413")])]})]});
            var Q160;
            Q160=makeQuery(id+"F10.boolean.opBoolean","INTERSECT",EDGE,{"disambiguationData":[OD(0.0)],"derivedFrom":[makeQuery(id+"F1.opExtrude","SWEPT_FACE",FACE,{"disambiguationData":[OSD([sQuery(id+"F0.wireOp",EDGE,"E0")])]}),makeQuery(id+"F10.opExtrude","SWEPT_FACE",FACE,{"disambiguationData":[OSD([sQuery(id+"F9.wireOp",EDGE,"E412")])]})]});
            var Q161;
            Q161=makeQuery(id+"F10.boolean.opBoolean","INTERSECT",EDGE,{"disambiguationData":[OD(0.0)],"derivedFrom":[makeQuery(id+"F1.opExtrude","SWEPT_FACE",FACE,{"disambiguationData":[OSD([sQuery(id+"F0.wireOp",EDGE,"E0")])]}),makeQuery(id+"F10.opExtrude","SWEPT_FACE",FACE,{"disambiguationData":[OSD([sQuery(id+"F9.wireOp",EDGE,"E411")])]})]});
            var Q162;
            Q162=makeQuery(id+"F10.boolean.opBoolean","INTERSECT",EDGE,{"disambiguationData":[OD(0.0)],"derivedFrom":[makeQuery(id+"F1.opExtrude","SWEPT_FACE",FACE,{"disambiguationData":[OSD([sQuery(id+"F0.wireOp",EDGE,"E0")])]}),makeQuery(id+"F10.opExtrude","SWEPT_FACE",FACE,{"disambiguationData":[OSD([sQuery(id+"F9.wireOp",EDGE,"E416")])]})]});
            var Q163;
            Q163=makeQuery(id+"F10.boolean.opBoolean","INTERSECT",EDGE,{"disambiguationData":[OD(0.0)],"derivedFrom":[makeQuery(id+"F1.opExtrude","SWEPT_FACE",FACE,{"disambiguationData":[OSD([sQuery(id+"F0.wireOp",EDGE,"E0")])]}),makeQuery(id+"F10.opExtrude","SWEPT_FACE",FACE,{"disambiguationData":[OSD([sQuery(id+"F9.wireOp",EDGE,"E415")])]})]});
            var Q164;
            Q164=makeQuery(id+"F10.boolean.opBoolean","INTERSECT",EDGE,{"disambiguationData":[OD(0.0)],"derivedFrom":[makeQuery(id+"F1.opExtrude","SWEPT_FACE",FACE,{"disambiguationData":[OSD([sQuery(id+"F0.wireOp",EDGE,"E0")])]}),makeQuery(id+"F10.opExtrude","SWEPT_FACE",FACE,{"disambiguationData":[OSD([sQuery(id+"F9.wireOp",EDGE,"E414")])]})]});
            var Q165;
            Q165=makeQuery(id+"F10.boolean.opBoolean","INTERSECT",EDGE,{"disambiguationData":[OD(0.0)],"derivedFrom":[makeQuery(id+"F1.opExtrude","SWEPT_FACE",FACE,{"disambiguationData":[OSD([sQuery(id+"F0.wireOp",EDGE,"E0")])]}),makeQuery(id+"F10.opExtrude","SWEPT_FACE",FACE,{"disambiguationData":[OSD([sQuery(id+"F9.wireOp",EDGE,"E416")])]})]});
            var Q166;
            Q166=makeQuery(id+"F10.boolean.opBoolean","INTERSECT",EDGE,{"disambiguationData":[OD(0.0)],"derivedFrom":[makeQuery(id+"F1.opExtrude","SWEPT_FACE",FACE,{"disambiguationData":[OSD([sQuery(id+"F0.wireOp",EDGE,"E0")])]}),makeQuery(id+"F10.opExtrude","SWEPT_FACE",FACE,{"disambiguationData":[OSD([sQuery(id+"F9.wireOp",EDGE,"E398")])]})]});
            var Q167;
            Q167=makeQuery(id+"F10.boolean.opBoolean","INTERSECT",EDGE,{"disambiguationData":[OD(0.0)],"derivedFrom":[makeQuery(id+"F1.opExtrude","SWEPT_FACE",FACE,{"disambiguationData":[OSD([sQuery(id+"F0.wireOp",EDGE,"E0")])]}),makeQuery(id+"F10.opExtrude","SWEPT_FACE",FACE,{"disambiguationData":[OSD([sQuery(id+"F9.wireOp",EDGE,"E393")])]})]});
            var Q168;
            Q168=makeQuery(id+"F10.boolean.opBoolean","INTERSECT",EDGE,{"disambiguationData":[OD(0.0)],"derivedFrom":[makeQuery(id+"F1.opExtrude","SWEPT_FACE",FACE,{"disambiguationData":[OSD([sQuery(id+"F0.wireOp",EDGE,"E0")])]}),makeQuery(id+"F10.opExtrude","SWEPT_FACE",FACE,{"disambiguationData":[OSD([sQuery(id+"F9.wireOp",EDGE,"E394")])]})]});
            var Q169;
            Q169=makeQuery(id+"F10.boolean.opBoolean","INTERSECT",EDGE,{"disambiguationData":[OD(0.0)],"derivedFrom":[makeQuery(id+"F1.opExtrude","SWEPT_FACE",FACE,{"disambiguationData":[OSD([sQuery(id+"F0.wireOp",EDGE,"E0")])]}),makeQuery(id+"F10.opExtrude","SWEPT_FACE",FACE,{"disambiguationData":[OSD([sQuery(id+"F9.wireOp",EDGE,"E395")])]})]});
            var Q170;
            Q170=makeQuery(id+"F10.boolean.opBoolean","INTERSECT",EDGE,{"disambiguationData":[OD(0.0)],"derivedFrom":[makeQuery(id+"F1.opExtrude","SWEPT_FACE",FACE,{"disambiguationData":[OSD([sQuery(id+"F0.wireOp",EDGE,"E0")])]}),makeQuery(id+"F10.opExtrude","SWEPT_FACE",FACE,{"disambiguationData":[OSD([sQuery(id+"F9.wireOp",EDGE,"E396")])]})]});
            var Q171;
            Q171=makeQuery(id+"F10.boolean.opBoolean","INTERSECT",EDGE,{"disambiguationData":[OD(0.0)],"derivedFrom":[makeQuery(id+"F1.opExtrude","SWEPT_FACE",FACE,{"disambiguationData":[OSD([sQuery(id+"F0.wireOp",EDGE,"E0")])]}),makeQuery(id+"F10.opExtrude","SWEPT_FACE",FACE,{"disambiguationData":[OSD([sQuery(id+"F9.wireOp",EDGE,"E397")])]})]});
            var Q172;
            Q172=makeQuery(id+"F7.boolean.opBoolean","INTERSECT",EDGE,{"disambiguationData":[OD(0.0)],"derivedFrom":[makeQuery(id+"F1.opExtrude","SWEPT_FACE",FACE,{"disambiguationData":[OSD([sQuery(id+"F0.wireOp",EDGE,"E0")])]}),makeQuery(id+"F7.opExtrude","SWEPT_FACE",FACE,{"disambiguationData":[OSD([sQuery(id+"F6.wireOp",EDGE,"E265")])]})]});
            var Q173;
            Q173=makeQuery(id+"F7.boolean.opBoolean","INTERSECT",EDGE,{"disambiguationData":[OD(0.0)],"derivedFrom":[makeQuery(id+"F1.opExtrude","SWEPT_FACE",FACE,{"disambiguationData":[OSD([sQuery(id+"F0.wireOp",EDGE,"E0")])]}),makeQuery(id+"F7.opExtrude","SWEPT_FACE",FACE,{"disambiguationData":[OSD([sQuery(id+"F6.wireOp",EDGE,"E266")])]})]});
            var Q174;
            Q174=makeQuery(id+"F7.boolean.opBoolean","INTERSECT",EDGE,{"disambiguationData":[OD(0.0)],"derivedFrom":[makeQuery(id+"F1.opExtrude","SWEPT_FACE",FACE,{"disambiguationData":[OSD([sQuery(id+"F0.wireOp",EDGE,"E0")])]}),makeQuery(id+"F7.opExtrude","SWEPT_FACE",FACE,{"disambiguationData":[OSD([sQuery(id+"F6.wireOp",EDGE,"E267")])]})]});
            var Q175;
            Q175=makeQuery(id+"F7.boolean.opBoolean","INTERSECT",EDGE,{"disambiguationData":[OD(0.0)],"derivedFrom":[makeQuery(id+"F1.opExtrude","SWEPT_FACE",FACE,{"disambiguationData":[OSD([sQuery(id+"F0.wireOp",EDGE,"E0")])]}),makeQuery(id+"F7.opExtrude","SWEPT_FACE",FACE,{"disambiguationData":[OSD([sQuery(id+"F6.wireOp",EDGE,"E268")])]})]});
            var Q176;
            Q176=makeQuery(id+"F7.boolean.opBoolean","INTERSECT",EDGE,{"disambiguationData":[OD(0.0)],"derivedFrom":[makeQuery(id+"F1.opExtrude","SWEPT_FACE",FACE,{"disambiguationData":[OSD([sQuery(id+"F0.wireOp",EDGE,"E0")])]}),makeQuery(id+"F7.opExtrude","SWEPT_FACE",FACE,{"disambiguationData":[OSD([sQuery(id+"F6.wireOp",EDGE,"E263")])]})]});
            var Q177;
            Q177=makeQuery(id+"F7.boolean.opBoolean","INTERSECT",EDGE,{"disambiguationData":[OD(0.0)],"derivedFrom":[makeQuery(id+"F1.opExtrude","SWEPT_FACE",FACE,{"disambiguationData":[OSD([sQuery(id+"F0.wireOp",EDGE,"E0")])]}),makeQuery(id+"F7.opExtrude","SWEPT_FACE",FACE,{"disambiguationData":[OSD([sQuery(id+"F6.wireOp",EDGE,"E264")])]})]});
            var Q178;
            Q178=makeQuery(id+"F7.boolean.opBoolean","INTERSECT",EDGE,{"disambiguationData":[OD(0.0)],"derivedFrom":[makeQuery(id+"F1.opExtrude","SWEPT_FACE",FACE,{"disambiguationData":[OSD([sQuery(id+"F0.wireOp",EDGE,"E0")])]}),makeQuery(id+"F7.opExtrude","SWEPT_FACE",FACE,{"disambiguationData":[OSD([sQuery(id+"F6.wireOp",EDGE,"E277")])]})]});
            var Q179;
            Q179=makeQuery(id+"F7.boolean.opBoolean","INTERSECT",EDGE,{"disambiguationData":[OD(0.0)],"derivedFrom":[makeQuery(id+"F1.opExtrude","SWEPT_FACE",FACE,{"disambiguationData":[OSD([sQuery(id+"F0.wireOp",EDGE,"E0")])]}),makeQuery(id+"F7.opExtrude","SWEPT_FACE",FACE,{"disambiguationData":[OSD([sQuery(id+"F6.wireOp",EDGE,"E278")])]})]});
            var Q180;
            Q180=makeQuery(id+"F7.boolean.opBoolean","INTERSECT",EDGE,{"disambiguationData":[OD(0.0)],"derivedFrom":[makeQuery(id+"F1.opExtrude","SWEPT_FACE",FACE,{"disambiguationData":[OSD([sQuery(id+"F0.wireOp",EDGE,"E0")])]}),makeQuery(id+"F7.opExtrude","SWEPT_FACE",FACE,{"disambiguationData":[OSD([sQuery(id+"F6.wireOp",EDGE,"0a54e51b-04a4-4c72-8fdd-f2044cd41bb6")])]})]});
            var Q181;
            Q181=makeQuery(id+"F7.boolean.opBoolean","INTERSECT",EDGE,{"disambiguationData":[OD(0.0)],"derivedFrom":[makeQuery(id+"F1.opExtrude","SWEPT_FACE",FACE,{"disambiguationData":[OSD([sQuery(id+"F0.wireOp",EDGE,"E0")])]}),makeQuery(id+"F7.opExtrude","SWEPT_FACE",FACE,{"disambiguationData":[OSD([sQuery(id+"F6.wireOp",EDGE,"5279c50d-e3c7-40df-a6ae-2a829e30a2e4")])]})]});
            var Q182;
            Q182=makeQuery(id+"F7.boolean.opBoolean","INTERSECT",EDGE,{"disambiguationData":[OD(0.0)],"derivedFrom":[makeQuery(id+"F1.opExtrude","SWEPT_FACE",FACE,{"disambiguationData":[OSD([sQuery(id+"F0.wireOp",EDGE,"E0")])]}),makeQuery(id+"F7.opExtrude","SWEPT_FACE",FACE,{"disambiguationData":[OSD([sQuery(id+"F6.wireOp",EDGE,"c00e0242-21cc-46da-ab10-4ac23868c1ae")])]})]});
            var Q183;
            Q183=makeQuery(id+"F7.boolean.opBoolean","INTERSECT",EDGE,{"disambiguationData":[OD(0.0)],"derivedFrom":[makeQuery(id+"F1.opExtrude","SWEPT_FACE",FACE,{"disambiguationData":[OSD([sQuery(id+"F0.wireOp",EDGE,"E0")])]}),makeQuery(id+"F7.opExtrude","SWEPT_FACE",FACE,{"disambiguationData":[OSD([sQuery(id+"F6.wireOp",EDGE,"E276")])]})]});
            var Q184;
            Q184=makeQuery(id+"F7.boolean.opBoolean","INTERSECT",EDGE,{"disambiguationData":[OD(0.0)],"derivedFrom":[makeQuery(id+"F1.opExtrude","SWEPT_FACE",FACE,{"disambiguationData":[OSD([sQuery(id+"F0.wireOp",EDGE,"E0")])]}),makeQuery(id+"F7.opExtrude","SWEPT_FACE",FACE,{"disambiguationData":[OSD([sQuery(id+"F6.wireOp",EDGE,"E247")])]})]});
            var Q185;
            Q185=makeQuery(id+"F7.boolean.opBoolean","INTERSECT",EDGE,{"disambiguationData":[OD(0.0)],"derivedFrom":[makeQuery(id+"F1.opExtrude","SWEPT_FACE",FACE,{"disambiguationData":[OSD([sQuery(id+"F0.wireOp",EDGE,"E0")])]}),makeQuery(id+"F7.opExtrude","SWEPT_FACE",FACE,{"disambiguationData":[OSD([sQuery(id+"F6.wireOp",EDGE,"E248")])]})]});
            var Q186;
            Q186=makeQuery(id+"F7.boolean.opBoolean","INTERSECT",EDGE,{"disambiguationData":[OD(0.0)],"derivedFrom":[makeQuery(id+"F1.opExtrude","SWEPT_FACE",FACE,{"disambiguationData":[OSD([sQuery(id+"F0.wireOp",EDGE,"E0")])]}),makeQuery(id+"F7.opExtrude","SWEPT_FACE",FACE,{"disambiguationData":[OSD([sQuery(id+"F6.wireOp",EDGE,"E249")])]})]});
            var Q187;
            Q187=makeQuery(id+"F7.boolean.opBoolean","INTERSECT",EDGE,{"disambiguationData":[OD(0.0)],"derivedFrom":[makeQuery(id+"F1.opExtrude","SWEPT_FACE",FACE,{"disambiguationData":[OSD([sQuery(id+"F0.wireOp",EDGE,"E0")])]}),makeQuery(id+"F7.opExtrude","SWEPT_FACE",FACE,{"disambiguationData":[OSD([sQuery(id+"F6.wireOp",EDGE,"E250")])]})]});
            var Q188;
            Q188=makeQuery(id+"F7.boolean.opBoolean","INTERSECT",EDGE,{"disambiguationData":[OD(0.0)],"derivedFrom":[makeQuery(id+"F1.opExtrude","SWEPT_FACE",FACE,{"disambiguationData":[OSD([sQuery(id+"F0.wireOp",EDGE,"E0")])]}),makeQuery(id+"F7.opExtrude","SWEPT_FACE",FACE,{"disambiguationData":[OSD([sQuery(id+"F6.wireOp",EDGE,"E245")])]})]});
            var Q189;
            Q189=makeQuery(id+"F7.boolean.opBoolean","INTERSECT",EDGE,{"disambiguationData":[OD(0.0)],"derivedFrom":[makeQuery(id+"F1.opExtrude","SWEPT_FACE",FACE,{"disambiguationData":[OSD([sQuery(id+"F0.wireOp",EDGE,"E0")])]}),makeQuery(id+"F7.opExtrude","SWEPT_FACE",FACE,{"disambiguationData":[OSD([sQuery(id+"F6.wireOp",EDGE,"E246")])]})]});
            var Q190;
            Q190=makeQuery(id+"F10.boolean.opBoolean","INTERSECT",EDGE,{"disambiguationData":[OD(0.0)],"derivedFrom":[makeQuery(id+"F1.opExtrude","SWEPT_FACE",FACE,{"disambiguationData":[OSD([sQuery(id+"F0.wireOp",EDGE,"E0")])]}),makeQuery(id+"F10.opExtrude","SWEPT_FACE",FACE,{"disambiguationData":[OSD([sQuery(id+"F9.wireOp",EDGE,"E380")])]})]});
            var Q191;
            Q191=makeQuery(id+"F10.boolean.opBoolean","INTERSECT",EDGE,{"disambiguationData":[OD(0.0)],"derivedFrom":[makeQuery(id+"F1.opExtrude","SWEPT_FACE",FACE,{"disambiguationData":[OSD([sQuery(id+"F0.wireOp",EDGE,"E0")])]}),makeQuery(id+"F10.opExtrude","SWEPT_FACE",FACE,{"disambiguationData":[OSD([sQuery(id+"F9.wireOp",EDGE,"E379")])]})]});
            var Q192;
            Q192=makeQuery(id+"F10.boolean.opBoolean","INTERSECT",EDGE,{"disambiguationData":[OD(0.0)],"derivedFrom":[makeQuery(id+"F1.opExtrude","SWEPT_FACE",FACE,{"disambiguationData":[OSD([sQuery(id+"F0.wireOp",EDGE,"E0")])]}),makeQuery(id+"F10.opExtrude","SWEPT_FACE",FACE,{"disambiguationData":[OSD([sQuery(id+"F9.wireOp",EDGE,"E378")])]})]});
            var Q193;
            Q193=makeQuery(id+"F10.boolean.opBoolean","INTERSECT",EDGE,{"disambiguationData":[OD(0.0)],"derivedFrom":[makeQuery(id+"F1.opExtrude","SWEPT_FACE",FACE,{"disambiguationData":[OSD([sQuery(id+"F0.wireOp",EDGE,"E0")])]}),makeQuery(id+"F10.opExtrude","SWEPT_FACE",FACE,{"disambiguationData":[OSD([sQuery(id+"F9.wireOp",EDGE,"E377")])]})]});
            var Q194;
            Q194=makeQuery(id+"F10.boolean.opBoolean","INTERSECT",EDGE,{"disambiguationData":[OD(0.0)],"derivedFrom":[makeQuery(id+"F1.opExtrude","SWEPT_FACE",FACE,{"disambiguationData":[OSD([sQuery(id+"F0.wireOp",EDGE,"E0")])]}),makeQuery(id+"F10.opExtrude","SWEPT_FACE",FACE,{"disambiguationData":[OSD([sQuery(id+"F9.wireOp",EDGE,"E376")])]})]});
            var Q195;
            Q195=makeQuery(id+"F10.boolean.opBoolean","INTERSECT",EDGE,{"disambiguationData":[OD(0.0)],"derivedFrom":[makeQuery(id+"F1.opExtrude","SWEPT_FACE",FACE,{"disambiguationData":[OSD([sQuery(id+"F0.wireOp",EDGE,"E0")])]}),makeQuery(id+"F10.opExtrude","SWEPT_FACE",FACE,{"disambiguationData":[OSD([sQuery(id+"F9.wireOp",EDGE,"E375")])]})]});
            var Q196;
            Q196=makeQuery(id+"F7.boolean.opBoolean","INTERSECT",EDGE,{"disambiguationData":[OD(0.0)],"derivedFrom":[makeQuery(id+"F1.opExtrude","SWEPT_FACE",FACE,{"disambiguationData":[OSD([sQuery(id+"F0.wireOp",EDGE,"E0")])]}),makeQuery(id+"F7.opExtrude","SWEPT_FACE",FACE,{"disambiguationData":[OSD([sQuery(id+"F6.wireOp",EDGE,"E229")])]})]});
            var Q197;
            Q197=makeQuery(id+"F7.boolean.opBoolean","INTERSECT",EDGE,{"disambiguationData":[OD(0.0)],"derivedFrom":[makeQuery(id+"F1.opExtrude","SWEPT_FACE",FACE,{"disambiguationData":[OSD([sQuery(id+"F0.wireOp",EDGE,"E0")])]}),makeQuery(id+"F7.opExtrude","SWEPT_FACE",FACE,{"disambiguationData":[OSD([sQuery(id+"F6.wireOp",EDGE,"E230")])]})]});
            var Q198;
            Q198=makeQuery(id+"F7.boolean.opBoolean","INTERSECT",EDGE,{"disambiguationData":[OD(0.0)],"derivedFrom":[makeQuery(id+"F1.opExtrude","SWEPT_FACE",FACE,{"disambiguationData":[OSD([sQuery(id+"F0.wireOp",EDGE,"E0")])]}),makeQuery(id+"F7.opExtrude","SWEPT_FACE",FACE,{"disambiguationData":[OSD([sQuery(id+"F6.wireOp",EDGE,"E231")])]})]});
            var Q199;
            Q199=makeQuery(id+"F7.boolean.opBoolean","INTERSECT",EDGE,{"disambiguationData":[OD(0.0)],"derivedFrom":[makeQuery(id+"F1.opExtrude","SWEPT_FACE",FACE,{"disambiguationData":[OSD([sQuery(id+"F0.wireOp",EDGE,"E0")])]}),makeQuery(id+"F7.opExtrude","SWEPT_FACE",FACE,{"disambiguationData":[OSD([sQuery(id+"F6.wireOp",EDGE,"E232")])]})]});
            var Q200;
            Q200=makeQuery(id+"F7.boolean.opBoolean","INTERSECT",EDGE,{"disambiguationData":[OD(0.0)],"derivedFrom":[makeQuery(id+"F1.opExtrude","SWEPT_FACE",FACE,{"disambiguationData":[OSD([sQuery(id+"F0.wireOp",EDGE,"E0")])]}),makeQuery(id+"F7.opExtrude","SWEPT_FACE",FACE,{"disambiguationData":[OSD([sQuery(id+"F6.wireOp",EDGE,"E227")])]})]});
            var Q201;
            Q201=makeQuery(id+"F7.boolean.opBoolean","INTERSECT",EDGE,{"disambiguationData":[OD(0.0)],"derivedFrom":[makeQuery(id+"F1.opExtrude","SWEPT_FACE",FACE,{"disambiguationData":[OSD([sQuery(id+"F0.wireOp",EDGE,"E0")])]}),makeQuery(id+"F7.opExtrude","SWEPT_FACE",FACE,{"disambiguationData":[OSD([sQuery(id+"F6.wireOp",EDGE,"E228")])]})]});
            var Q202;
            Q202=makeQuery(id+"F10.boolean.opBoolean","INTERSECT",EDGE,{"disambiguationData":[OD(0.0)],"derivedFrom":[makeQuery(id+"F1.opExtrude","SWEPT_FACE",FACE,{"disambiguationData":[OSD([sQuery(id+"F0.wireOp",EDGE,"E0")])]}),makeQuery(id+"F10.opExtrude","SWEPT_FACE",FACE,{"disambiguationData":[OSD([sQuery(id+"F9.wireOp",EDGE,"E361")])]})]});
            var Q203;
            Q203=makeQuery(id+"F10.boolean.opBoolean","INTERSECT",EDGE,{"disambiguationData":[OD(0.0)],"derivedFrom":[makeQuery(id+"F1.opExtrude","SWEPT_FACE",FACE,{"disambiguationData":[OSD([sQuery(id+"F0.wireOp",EDGE,"E0")])]}),makeQuery(id+"F10.opExtrude","SWEPT_FACE",FACE,{"disambiguationData":[OSD([sQuery(id+"F9.wireOp",EDGE,"E360")])]})]});
            var Q204;
            Q204=makeQuery(id+"F10.boolean.opBoolean","INTERSECT",EDGE,{"disambiguationData":[OD(0.0)],"derivedFrom":[makeQuery(id+"F1.opExtrude","SWEPT_FACE",FACE,{"disambiguationData":[OSD([sQuery(id+"F0.wireOp",EDGE,"E0")])]}),makeQuery(id+"F10.opExtrude","SWEPT_FACE",FACE,{"disambiguationData":[OSD([sQuery(id+"F9.wireOp",EDGE,"E359")])]})]});
            var Q205;
            Q205=makeQuery(id+"F10.boolean.opBoolean","INTERSECT",EDGE,{"disambiguationData":[OD(0.0)],"derivedFrom":[makeQuery(id+"F1.opExtrude","SWEPT_FACE",FACE,{"disambiguationData":[OSD([sQuery(id+"F0.wireOp",EDGE,"E0")])]}),makeQuery(id+"F10.opExtrude","SWEPT_FACE",FACE,{"disambiguationData":[OSD([sQuery(id+"F9.wireOp",EDGE,"E358")])]})]});
            var Q206;
            Q206=makeQuery(id+"F10.boolean.opBoolean","INTERSECT",EDGE,{"disambiguationData":[OD(0.0)],"derivedFrom":[makeQuery(id+"F1.opExtrude","SWEPT_FACE",FACE,{"disambiguationData":[OSD([sQuery(id+"F0.wireOp",EDGE,"E0")])]}),makeQuery(id+"F10.opExtrude","SWEPT_FACE",FACE,{"disambiguationData":[OSD([sQuery(id+"F9.wireOp",EDGE,"E357")])]})]});
            var Q207;
            Q207=makeQuery(id+"F10.boolean.opBoolean","INTERSECT",EDGE,{"disambiguationData":[OD(0.0)],"derivedFrom":[makeQuery(id+"F1.opExtrude","SWEPT_FACE",FACE,{"disambiguationData":[OSD([sQuery(id+"F0.wireOp",EDGE,"E0")])]}),makeQuery(id+"F10.opExtrude","SWEPT_FACE",FACE,{"disambiguationData":[OSD([sQuery(id+"F9.wireOp",EDGE,"E362")])]})]});
            var Q208;
            Q208=makeQuery(id+"F10.boolean.opBoolean","INTERSECT",EDGE,{"disambiguationData":[OD(0.0)],"derivedFrom":[makeQuery(id+"F1.opExtrude","SWEPT_FACE",FACE,{"disambiguationData":[OSD([sQuery(id+"F0.wireOp",EDGE,"E0")])]}),makeQuery(id+"F10.opExtrude","SWEPT_FACE",FACE,{"disambiguationData":[OSD([sQuery(id+"F9.wireOp",EDGE,"E341")])]})]});
            var Q209;
            Q209=makeQuery(id+"F10.boolean.opBoolean","INTERSECT",EDGE,{"disambiguationData":[OD(0.0)],"derivedFrom":[makeQuery(id+"F1.opExtrude","SWEPT_FACE",FACE,{"disambiguationData":[OSD([sQuery(id+"F0.wireOp",EDGE,"E0")])]}),makeQuery(id+"F10.opExtrude","SWEPT_FACE",FACE,{"disambiguationData":[OSD([sQuery(id+"F9.wireOp",EDGE,"E342")])]})]});
            var Q210;
            Q210=makeQuery(id+"F10.boolean.opBoolean","INTERSECT",EDGE,{"disambiguationData":[OD(0.0)],"derivedFrom":[makeQuery(id+"F1.opExtrude","SWEPT_FACE",FACE,{"disambiguationData":[OSD([sQuery(id+"F0.wireOp",EDGE,"E0")])]}),makeQuery(id+"F10.opExtrude","SWEPT_FACE",FACE,{"disambiguationData":[OSD([sQuery(id+"F9.wireOp",EDGE,"E343")])]})]});
            var Q211;
            Q211=makeQuery(id+"F10.boolean.opBoolean","INTERSECT",EDGE,{"disambiguationData":[OD(0.0)],"derivedFrom":[makeQuery(id+"F1.opExtrude","SWEPT_FACE",FACE,{"disambiguationData":[OSD([sQuery(id+"F0.wireOp",EDGE,"E0")])]}),makeQuery(id+"F10.opExtrude","SWEPT_FACE",FACE,{"disambiguationData":[OSD([sQuery(id+"F9.wireOp",EDGE,"E344")])]})]});
            var Q212;
            Q212=makeQuery(id+"F10.boolean.opBoolean","INTERSECT",EDGE,{"disambiguationData":[OD(0.0)],"derivedFrom":[makeQuery(id+"F1.opExtrude","SWEPT_FACE",FACE,{"disambiguationData":[OSD([sQuery(id+"F0.wireOp",EDGE,"E0")])]}),makeQuery(id+"F10.opExtrude","SWEPT_FACE",FACE,{"disambiguationData":[OSD([sQuery(id+"F9.wireOp",EDGE,"E339")])]})]});
            var Q213;
            Q213=makeQuery(id+"F10.boolean.opBoolean","INTERSECT",EDGE,{"disambiguationData":[OD(0.0)],"derivedFrom":[makeQuery(id+"F1.opExtrude","SWEPT_FACE",FACE,{"disambiguationData":[OSD([sQuery(id+"F0.wireOp",EDGE,"E0")])]}),makeQuery(id+"F10.opExtrude","SWEPT_FACE",FACE,{"disambiguationData":[OSD([sQuery(id+"F9.wireOp",EDGE,"E340")])]})]});
            var Q214;
            Q214=makeQuery(id+"F7.boolean.opBoolean","INTERSECT",EDGE,{"disambiguationData":[OD(0.0)],"derivedFrom":[makeQuery(id+"F1.opExtrude","SWEPT_FACE",FACE,{"disambiguationData":[OSD([sQuery(id+"F0.wireOp",EDGE,"E0")])]}),makeQuery(id+"F7.opExtrude","SWEPT_FACE",FACE,{"disambiguationData":[OSD([sQuery(id+"F6.wireOp",EDGE,"E211")])]})]});
            var Q215;
            Q215=makeQuery(id+"F7.boolean.opBoolean","INTERSECT",EDGE,{"disambiguationData":[OD(0.0)],"derivedFrom":[makeQuery(id+"F1.opExtrude","SWEPT_FACE",FACE,{"disambiguationData":[OSD([sQuery(id+"F0.wireOp",EDGE,"E0")])]}),makeQuery(id+"F7.opExtrude","SWEPT_FACE",FACE,{"disambiguationData":[OSD([sQuery(id+"F6.wireOp",EDGE,"E212")])]})]});
            var Q216;
            Q216=makeQuery(id+"F7.boolean.opBoolean","INTERSECT",EDGE,{"disambiguationData":[OD(0.0)],"derivedFrom":[makeQuery(id+"F1.opExtrude","SWEPT_FACE",FACE,{"disambiguationData":[OSD([sQuery(id+"F0.wireOp",EDGE,"E0")])]}),makeQuery(id+"F7.opExtrude","SWEPT_FACE",FACE,{"disambiguationData":[OSD([sQuery(id+"F6.wireOp",EDGE,"E213")])]})]});
            var Q217;
            Q217=makeQuery(id+"F7.boolean.opBoolean","INTERSECT",EDGE,{"disambiguationData":[OD(0.0)],"derivedFrom":[makeQuery(id+"F1.opExtrude","SWEPT_FACE",FACE,{"disambiguationData":[OSD([sQuery(id+"F0.wireOp",EDGE,"E0")])]}),makeQuery(id+"F7.opExtrude","SWEPT_FACE",FACE,{"disambiguationData":[OSD([sQuery(id+"F6.wireOp",EDGE,"E214")])]})]});
            var Q218;
            Q218=makeQuery(id+"F7.boolean.opBoolean","INTERSECT",EDGE,{"disambiguationData":[OD(0.0)],"derivedFrom":[makeQuery(id+"F1.opExtrude","SWEPT_FACE",FACE,{"disambiguationData":[OSD([sQuery(id+"F0.wireOp",EDGE,"E0")])]}),makeQuery(id+"F7.opExtrude","SWEPT_FACE",FACE,{"disambiguationData":[OSD([sQuery(id+"F6.wireOp",EDGE,"E209")])]})]});
            var Q219;
            Q219=makeQuery(id+"F7.boolean.opBoolean","INTERSECT",EDGE,{"disambiguationData":[OD(0.0)],"derivedFrom":[makeQuery(id+"F1.opExtrude","SWEPT_FACE",FACE,{"disambiguationData":[OSD([sQuery(id+"F0.wireOp",EDGE,"E0")])]}),makeQuery(id+"F7.opExtrude","SWEPT_FACE",FACE,{"disambiguationData":[OSD([sQuery(id+"F6.wireOp",EDGE,"E210")])]})]});
            var Q220;
            Q220=makeQuery(id+"F10.boolean.opBoolean","INTERSECT",EDGE,{"disambiguationData":[OD(0.0)],"derivedFrom":[makeQuery(id+"F1.opExtrude","SWEPT_FACE",FACE,{"disambiguationData":[OSD([sQuery(id+"F0.wireOp",EDGE,"E0")])]}),makeQuery(id+"F10.opExtrude","SWEPT_FACE",FACE,{"disambiguationData":[OSD([sQuery(id+"F9.wireOp",EDGE,"E323")])]})]});
            var Q221;
            Q221=makeQuery(id+"F10.boolean.opBoolean","INTERSECT",EDGE,{"disambiguationData":[OD(0.0)],"derivedFrom":[makeQuery(id+"F1.opExtrude","SWEPT_FACE",FACE,{"disambiguationData":[OSD([sQuery(id+"F0.wireOp",EDGE,"E0")])]}),makeQuery(id+"F10.opExtrude","SWEPT_FACE",FACE,{"disambiguationData":[OSD([sQuery(id+"F9.wireOp",EDGE,"E324")])]})]});
            var Q222;
            Q222=makeQuery(id+"F10.boolean.opBoolean","INTERSECT",EDGE,{"disambiguationData":[OD(0.0)],"derivedFrom":[makeQuery(id+"F1.opExtrude","SWEPT_FACE",FACE,{"disambiguationData":[OSD([sQuery(id+"F0.wireOp",EDGE,"E0")])]}),makeQuery(id+"F10.opExtrude","SWEPT_FACE",FACE,{"disambiguationData":[OSD([sQuery(id+"F9.wireOp",EDGE,"E325")])]})]});
            var Q223;
            Q223=makeQuery(id+"F10.boolean.opBoolean","INTERSECT",EDGE,{"disambiguationData":[OD(0.0)],"derivedFrom":[makeQuery(id+"F1.opExtrude","SWEPT_FACE",FACE,{"disambiguationData":[OSD([sQuery(id+"F0.wireOp",EDGE,"E0")])]}),makeQuery(id+"F10.opExtrude","SWEPT_FACE",FACE,{"disambiguationData":[OSD([sQuery(id+"F9.wireOp",EDGE,"E326")])]})]});
            var Q224;
            Q224=makeQuery(id+"F10.boolean.opBoolean","INTERSECT",EDGE,{"disambiguationData":[OD(0.0)],"derivedFrom":[makeQuery(id+"F1.opExtrude","SWEPT_FACE",FACE,{"disambiguationData":[OSD([sQuery(id+"F0.wireOp",EDGE,"E0")])]}),makeQuery(id+"F10.opExtrude","SWEPT_FACE",FACE,{"disambiguationData":[OSD([sQuery(id+"F9.wireOp",EDGE,"E321")])]})]});
            var Q225;
            Q225=makeQuery(id+"F10.boolean.opBoolean","INTERSECT",EDGE,{"disambiguationData":[OD(0.0)],"derivedFrom":[makeQuery(id+"F1.opExtrude","SWEPT_FACE",FACE,{"disambiguationData":[OSD([sQuery(id+"F0.wireOp",EDGE,"E0")])]}),makeQuery(id+"F10.opExtrude","SWEPT_FACE",FACE,{"disambiguationData":[OSD([sQuery(id+"F9.wireOp",EDGE,"E322")])]})]});
            var Q226;
            Q226=makeQuery(id+"F7.boolean.opBoolean","INTERSECT",EDGE,{"disambiguationData":[OD(0.0)],"derivedFrom":[makeQuery(id+"F1.opExtrude","SWEPT_FACE",FACE,{"disambiguationData":[OSD([sQuery(id+"F0.wireOp",EDGE,"E0")])]}),makeQuery(id+"F7.opExtrude","SWEPT_FACE",FACE,{"disambiguationData":[OSD([sQuery(id+"F6.wireOp",EDGE,"E193")])]})]});
            var Q227;
            Q227=makeQuery(id+"F7.boolean.opBoolean","INTERSECT",EDGE,{"disambiguationData":[OD(0.0)],"derivedFrom":[makeQuery(id+"F1.opExtrude","SWEPT_FACE",FACE,{"disambiguationData":[OSD([sQuery(id+"F0.wireOp",EDGE,"E0")])]}),makeQuery(id+"F7.opExtrude","SWEPT_FACE",FACE,{"disambiguationData":[OSD([sQuery(id+"F6.wireOp",EDGE,"E194")])]})]});
            var Q228;
            Q228=makeQuery(id+"F7.boolean.opBoolean","INTERSECT",EDGE,{"disambiguationData":[OD(0.0)],"derivedFrom":[makeQuery(id+"F1.opExtrude","SWEPT_FACE",FACE,{"disambiguationData":[OSD([sQuery(id+"F0.wireOp",EDGE,"E0")])]}),makeQuery(id+"F7.opExtrude","SWEPT_FACE",FACE,{"disambiguationData":[OSD([sQuery(id+"F6.wireOp",EDGE,"E195")])]})]});
            var Q229;
            Q229=makeQuery(id+"F7.boolean.opBoolean","INTERSECT",EDGE,{"disambiguationData":[OD(0.0)],"derivedFrom":[makeQuery(id+"F1.opExtrude","SWEPT_FACE",FACE,{"disambiguationData":[OSD([sQuery(id+"F0.wireOp",EDGE,"E0")])]}),makeQuery(id+"F7.opExtrude","SWEPT_FACE",FACE,{"disambiguationData":[OSD([sQuery(id+"F6.wireOp",EDGE,"E196")])]})]});
            var Q230;
            Q230=makeQuery(id+"F7.boolean.opBoolean","INTERSECT",EDGE,{"disambiguationData":[OD(0.0)],"derivedFrom":[makeQuery(id+"F1.opExtrude","SWEPT_FACE",FACE,{"disambiguationData":[OSD([sQuery(id+"F0.wireOp",EDGE,"E0")])]}),makeQuery(id+"F7.opExtrude","SWEPT_FACE",FACE,{"disambiguationData":[OSD([sQuery(id+"F6.wireOp",EDGE,"E191")])]})]});
            var Q231;
            Q231=makeQuery(id+"F7.boolean.opBoolean","INTERSECT",EDGE,{"disambiguationData":[OD(0.0)],"derivedFrom":[makeQuery(id+"F1.opExtrude","SWEPT_FACE",FACE,{"disambiguationData":[OSD([sQuery(id+"F0.wireOp",EDGE,"E0")])]}),makeQuery(id+"F7.opExtrude","SWEPT_FACE",FACE,{"disambiguationData":[OSD([sQuery(id+"F6.wireOp",EDGE,"E192")])]})]});
            var Q232;
            Q232=makeQuery(id+"F10.boolean.opBoolean","INTERSECT",EDGE,{"disambiguationData":[OD(0.0)],"derivedFrom":[makeQuery(id+"F1.opExtrude","SWEPT_FACE",FACE,{"disambiguationData":[OSD([sQuery(id+"F0.wireOp",EDGE,"E0")])]}),makeQuery(id+"F10.opExtrude","SWEPT_FACE",FACE,{"disambiguationData":[OSD([sQuery(id+"F9.wireOp",EDGE,"E308")])]})]});
            var Q233;
            Q233=makeQuery(id+"F10.boolean.opBoolean","INTERSECT",EDGE,{"disambiguationData":[OD(0.0)],"derivedFrom":[makeQuery(id+"F1.opExtrude","SWEPT_FACE",FACE,{"disambiguationData":[OSD([sQuery(id+"F0.wireOp",EDGE,"E0")])]}),makeQuery(id+"F10.opExtrude","SWEPT_FACE",FACE,{"disambiguationData":[OSD([sQuery(id+"F9.wireOp",EDGE,"E307")])]})]});
            var Q234;
            Q234=makeQuery(id+"F10.boolean.opBoolean","INTERSECT",EDGE,{"disambiguationData":[OD(0.0)],"derivedFrom":[makeQuery(id+"F1.opExtrude","SWEPT_FACE",FACE,{"disambiguationData":[OSD([sQuery(id+"F0.wireOp",EDGE,"E0")])]}),makeQuery(id+"F10.opExtrude","SWEPT_FACE",FACE,{"disambiguationData":[OSD([sQuery(id+"F9.wireOp",EDGE,"E306")])]})]});
            var Q235;
            Q235=makeQuery(id+"F10.boolean.opBoolean","INTERSECT",EDGE,{"disambiguationData":[OD(0.0)],"derivedFrom":[makeQuery(id+"F1.opExtrude","SWEPT_FACE",FACE,{"disambiguationData":[OSD([sQuery(id+"F0.wireOp",EDGE,"E0")])]}),makeQuery(id+"F10.opExtrude","SWEPT_FACE",FACE,{"disambiguationData":[OSD([sQuery(id+"F9.wireOp",EDGE,"E305")])]})]});
            var Q236;
            Q236=makeQuery(id+"F10.boolean.opBoolean","INTERSECT",EDGE,{"disambiguationData":[OD(0.0)],"derivedFrom":[makeQuery(id+"F1.opExtrude","SWEPT_FACE",FACE,{"disambiguationData":[OSD([sQuery(id+"F0.wireOp",EDGE,"E0")])]}),makeQuery(id+"F10.opExtrude","SWEPT_FACE",FACE,{"disambiguationData":[OSD([sQuery(id+"F9.wireOp",EDGE,"E304")])]})]});
            var Q237;
            Q237=makeQuery(id+"F10.boolean.opBoolean","INTERSECT",EDGE,{"disambiguationData":[OD(0.0)],"derivedFrom":[makeQuery(id+"F1.opExtrude","SWEPT_FACE",FACE,{"disambiguationData":[OSD([sQuery(id+"F0.wireOp",EDGE,"E0")])]}),makeQuery(id+"F10.opExtrude","SWEPT_FACE",FACE,{"disambiguationData":[OSD([sQuery(id+"F9.wireOp",EDGE,"E303")])]})]});
            var Q238;
            Q238=makeQuery(id+"F7.boolean.opBoolean","INTERSECT",EDGE,{"disambiguationData":[OD(0.0)],"derivedFrom":[makeQuery(id+"F1.opExtrude","SWEPT_FACE",FACE,{"disambiguationData":[OSD([sQuery(id+"F0.wireOp",EDGE,"E0")])]}),makeQuery(id+"F7.opExtrude","SWEPT_FACE",FACE,{"disambiguationData":[OSD([sQuery(id+"F6.wireOp",EDGE,"E175")])]})]});
            var Q239;
            Q239=makeQuery(id+"F7.boolean.opBoolean","INTERSECT",EDGE,{"disambiguationData":[OD(0.0)],"derivedFrom":[makeQuery(id+"F1.opExtrude","SWEPT_FACE",FACE,{"disambiguationData":[OSD([sQuery(id+"F0.wireOp",EDGE,"E0")])]}),makeQuery(id+"F7.opExtrude","SWEPT_FACE",FACE,{"disambiguationData":[OSD([sQuery(id+"F6.wireOp",EDGE,"E176")])]})]});
            var Q240;
            Q240=makeQuery(id+"F7.boolean.opBoolean","INTERSECT",EDGE,{"disambiguationData":[OD(0.0)],"derivedFrom":[makeQuery(id+"F1.opExtrude","SWEPT_FACE",FACE,{"disambiguationData":[OSD([sQuery(id+"F0.wireOp",EDGE,"E0")])]}),makeQuery(id+"F7.opExtrude","SWEPT_FACE",FACE,{"disambiguationData":[OSD([sQuery(id+"F6.wireOp",EDGE,"E177")])]})]});
            var Q241;
            Q241=makeQuery(id+"F7.boolean.opBoolean","INTERSECT",EDGE,{"disambiguationData":[OD(0.0)],"derivedFrom":[makeQuery(id+"F1.opExtrude","SWEPT_FACE",FACE,{"disambiguationData":[OSD([sQuery(id+"F0.wireOp",EDGE,"E0")])]}),makeQuery(id+"F7.opExtrude","SWEPT_FACE",FACE,{"disambiguationData":[OSD([sQuery(id+"F6.wireOp",EDGE,"E178")])]})]});
            var Q242;
            Q242=makeQuery(id+"F7.boolean.opBoolean","INTERSECT",EDGE,{"disambiguationData":[OD(0.0)],"derivedFrom":[makeQuery(id+"F1.opExtrude","SWEPT_FACE",FACE,{"disambiguationData":[OSD([sQuery(id+"F0.wireOp",EDGE,"E0")])]}),makeQuery(id+"F7.opExtrude","SWEPT_FACE",FACE,{"disambiguationData":[OSD([sQuery(id+"F6.wireOp",EDGE,"E173")])]})]});
            var Q243;
            Q243=makeQuery(id+"F7.boolean.opBoolean","INTERSECT",EDGE,{"disambiguationData":[OD(0.0)],"derivedFrom":[makeQuery(id+"F1.opExtrude","SWEPT_FACE",FACE,{"disambiguationData":[OSD([sQuery(id+"F0.wireOp",EDGE,"E0")])]}),makeQuery(id+"F7.opExtrude","SWEPT_FACE",FACE,{"disambiguationData":[OSD([sQuery(id+"F6.wireOp",EDGE,"E174")])]})]});
            var Q244;
            Q244=makeQuery(id+"F7.boolean.opBoolean","INTERSECT",EDGE,{"disambiguationData":[OD(0.0)],"derivedFrom":[makeQuery(id+"F1.opExtrude","SWEPT_FACE",FACE,{"disambiguationData":[OSD([sQuery(id+"F0.wireOp",EDGE,"E0")])]}),makeQuery(id+"F7.opExtrude","SWEPT_FACE",FACE,{"disambiguationData":[OSD([sQuery(id+"F6.wireOp",EDGE,"E177")])]})]});
            var Q245;
            Q245=makeQuery(id+"F7.boolean.opBoolean","INTERSECT",EDGE,{"disambiguationData":[OD(0.0)],"derivedFrom":[makeQuery(id+"F1.opExtrude","SWEPT_FACE",FACE,{"disambiguationData":[OSD([sQuery(id+"F0.wireOp",EDGE,"E0")])]}),makeQuery(id+"F7.opExtrude","SWEPT_FACE",FACE,{"disambiguationData":[OSD([sQuery(id+"F6.wireOp",EDGE,"E159")])]})]});
            var Q246;
            Q246=makeQuery(id+"F7.boolean.opBoolean","INTERSECT",EDGE,{"disambiguationData":[OD(0.0)],"derivedFrom":[makeQuery(id+"F1.opExtrude","SWEPT_FACE",FACE,{"disambiguationData":[OSD([sQuery(id+"F0.wireOp",EDGE,"E0")])]}),makeQuery(id+"F7.opExtrude","SWEPT_FACE",FACE,{"disambiguationData":[OSD([sQuery(id+"F6.wireOp",EDGE,"E158")])]})]});
            var Q247;
            Q247=makeQuery(id+"F7.boolean.opBoolean","INTERSECT",EDGE,{"disambiguationData":[OD(0.0)],"derivedFrom":[makeQuery(id+"F1.opExtrude","SWEPT_FACE",FACE,{"disambiguationData":[OSD([sQuery(id+"F0.wireOp",EDGE,"E0")])]}),makeQuery(id+"F7.opExtrude","SWEPT_FACE",FACE,{"disambiguationData":[OSD([sQuery(id+"F6.wireOp",EDGE,"E157")])]})]});
            var Q248;
            Q248=makeQuery(id+"F7.boolean.opBoolean","INTERSECT",EDGE,{"disambiguationData":[OD(0.0)],"derivedFrom":[makeQuery(id+"F1.opExtrude","SWEPT_FACE",FACE,{"disambiguationData":[OSD([sQuery(id+"F0.wireOp",EDGE,"E0")])]}),makeQuery(id+"F7.opExtrude","SWEPT_FACE",FACE,{"disambiguationData":[OSD([sQuery(id+"F6.wireOp",EDGE,"E156")])]})]});
            var Q249;
            Q249=makeQuery(id+"F7.boolean.opBoolean","INTERSECT",EDGE,{"disambiguationData":[OD(0.0)],"derivedFrom":[makeQuery(id+"F1.opExtrude","SWEPT_FACE",FACE,{"disambiguationData":[OSD([sQuery(id+"F0.wireOp",EDGE,"E0")])]}),makeQuery(id+"F7.opExtrude","SWEPT_FACE",FACE,{"disambiguationData":[OSD([sQuery(id+"F6.wireOp",EDGE,"E155")])]})]});
            var Q250;
            Q250=makeQuery(id+"F7.boolean.opBoolean","INTERSECT",EDGE,{"disambiguationData":[OD(0.0)],"derivedFrom":[makeQuery(id+"F1.opExtrude","SWEPT_FACE",FACE,{"disambiguationData":[OSD([sQuery(id+"F0.wireOp",EDGE,"E0")])]}),makeQuery(id+"F7.opExtrude","SWEPT_FACE",FACE,{"disambiguationData":[OSD([sQuery(id+"F6.wireOp",EDGE,"E160")])]})]});
            var Q251;
            Q251=makeQuery(id+"F10.boolean.opBoolean","INTERSECT",EDGE,{"disambiguationData":[OD(0.0)],"derivedFrom":[makeQuery(id+"F1.opExtrude","SWEPT_FACE",FACE,{"disambiguationData":[OSD([sQuery(id+"F0.wireOp",EDGE,"E0")])]}),makeQuery(id+"F10.opExtrude","SWEPT_FACE",FACE,{"disambiguationData":[OSD([sQuery(id+"F9.wireOp",EDGE,"E290")])]})]});
            var Q252;
            Q252=makeQuery(id+"F10.boolean.opBoolean","INTERSECT",EDGE,{"disambiguationData":[OD(0.0)],"derivedFrom":[makeQuery(id+"F1.opExtrude","SWEPT_FACE",FACE,{"disambiguationData":[OSD([sQuery(id+"F0.wireOp",EDGE,"E0")])]}),makeQuery(id+"F10.opExtrude","SWEPT_FACE",FACE,{"disambiguationData":[OSD([sQuery(id+"F9.wireOp",EDGE,"E420")])]})]});
            var Q253;
            Q253=makeQuery(id+"F10.boolean.opBoolean","INTERSECT",EDGE,{"disambiguationData":[OD(0.0)],"derivedFrom":[makeQuery(id+"F1.opExtrude","SWEPT_FACE",FACE,{"disambiguationData":[OSD([sQuery(id+"F0.wireOp",EDGE,"E0")])]}),makeQuery(id+"F10.opExtrude","SWEPT_FACE",FACE,{"disambiguationData":[OSD([sQuery(id+"F9.wireOp",EDGE,"E418"),sQuery(id+"F9.wireOp",EDGE,"E419")])]})]});
            var Q254;
            Q254=makeQuery(id+"F10.boolean.opBoolean","INTERSECT",EDGE,{"disambiguationData":[OD(0.0)],"derivedFrom":[makeQuery(id+"F1.opExtrude","SWEPT_FACE",FACE,{"disambiguationData":[OSD([sQuery(id+"F0.wireOp",EDGE,"E0")])]}),makeQuery(id+"F10.opExtrude","SWEPT_FACE",FACE,{"disambiguationData":[OSD([sQuery(id+"F9.wireOp",EDGE,"E421")])]})]});
            var Q255;
            Q255=makeQuery(id+"F12.boolean.opBoolean","INTERSECT",EDGE,{"derivedFrom":[makeQuery(id+"F1.opExtrude","SWEPT_FACE",FACE,{"disambiguationData":[OSD([sQuery(id+"F0.wireOp",EDGE,"E0")])]}),makeQuery(id+"F12.opExtrude","SWEPT_FACE",FACE,{"disambiguationData":[OSD([sQuery(id+"F11.wireOp",EDGE,"E556"),sQuery(id+"F11.wireOp",EDGE,"E557")])]})]});
            var Q256;
            Q256=makeQuery(id+"F12.boolean.opBoolean","INTERSECT",EDGE,{"derivedFrom":[makeQuery(id+"F1.opExtrude","SWEPT_FACE",FACE,{"disambiguationData":[OSD([sQuery(id+"F0.wireOp",EDGE,"E0")])]}),makeQuery(id+"F12.opExtrude","SWEPT_FACE",FACE,{"disambiguationData":[OSD([sQuery(id+"F11.wireOp",EDGE,"E558")])]})]});
            var Q257;
            Q257=makeQuery(id+"F12.boolean.opBoolean","INTERSECT",EDGE,{"derivedFrom":[makeQuery(id+"F1.opExtrude","SWEPT_FACE",FACE,{"disambiguationData":[OSD([sQuery(id+"F0.wireOp",EDGE,"E0")])]}),makeQuery(id+"F12.opExtrude","SWEPT_FACE",FACE,{"disambiguationData":[OSD([sQuery(id+"F11.wireOp",EDGE,"E428")])]})]});
            var Q258;
            Q258=makeQuery(id+"F12.boolean.opBoolean","INTERSECT",EDGE,{"derivedFrom":[makeQuery(id+"F1.opExtrude","SWEPT_FACE",FACE,{"disambiguationData":[OSD([sQuery(id+"F0.wireOp",EDGE,"E0")])]}),makeQuery(id+"F12.opExtrude","SWEPT_FACE",FACE,{"disambiguationData":[OSD([sQuery(id+"F11.wireOp",EDGE,"E559")])]})]});
            var Q259;
            Q259=makeQuery(id+"F5.boolean.opBoolean","INTERSECT",EDGE,{"disambiguationData":[OD(1.0)],"derivedFrom":[makeQuery(id+"F1.opExtrude","SWEPT_FACE",FACE,{"disambiguationData":[OSD([sQuery(id+"F0.wireOp",EDGE,"E0")])]}),makeQuery(id+"F5.opExtrude","SWEPT_FACE",FACE,{"disambiguationData":[OSD([sQuery(id+"F4.wireOp",EDGE,"E15")])]})]});
            var Q260;
            Q260=makeQuery(id+"F5.boolean.opBoolean","INTERSECT",EDGE,{"disambiguationData":[OD(1.0)],"derivedFrom":[makeQuery(id+"F1.opExtrude","SWEPT_FACE",FACE,{"disambiguationData":[OSD([sQuery(id+"F0.wireOp",EDGE,"E0")])]}),makeQuery(id+"F5.opExtrude","SWEPT_FACE",FACE,{"disambiguationData":[OSD([sQuery(id+"F4.wireOp",EDGE,"E16")])]})]});
            var Q261;
            Q261=makeQuery(id+"F5.boolean.opBoolean","INTERSECT",EDGE,{"disambiguationData":[OD(1.0)],"derivedFrom":[makeQuery(id+"F1.opExtrude","SWEPT_FACE",FACE,{"disambiguationData":[OSD([sQuery(id+"F0.wireOp",EDGE,"E0")])]}),makeQuery(id+"F5.opExtrude","SWEPT_FACE",FACE,{"disambiguationData":[OSD([sQuery(id+"F4.wireOp",EDGE,"E17")])]})]});
            var Q262;
            Q262=makeQuery(id+"F5.boolean.opBoolean","INTERSECT",EDGE,{"disambiguationData":[OD(1.0)],"derivedFrom":[makeQuery(id+"F1.opExtrude","SWEPT_FACE",FACE,{"disambiguationData":[OSD([sQuery(id+"F0.wireOp",EDGE,"E0")])]}),makeQuery(id+"F5.opExtrude","SWEPT_FACE",FACE,{"disambiguationData":[OSD([sQuery(id+"F4.wireOp",EDGE,"E18")])]})]});
            var Q263;
            Q263=makeQuery(id+"F5.boolean.opBoolean","INTERSECT",EDGE,{"disambiguationData":[OD(1.0)],"derivedFrom":[makeQuery(id+"F1.opExtrude","SWEPT_FACE",FACE,{"disambiguationData":[OSD([sQuery(id+"F0.wireOp",EDGE,"E0")])]}),makeQuery(id+"F5.opExtrude","SWEPT_FACE",FACE,{"disambiguationData":[OSD([sQuery(id+"F4.wireOp",EDGE,"E19")])]})]});
            var Q264;
            Q264=makeQuery(id+"F5.boolean.opBoolean","INTERSECT",EDGE,{"disambiguationData":[OD(1.0)],"derivedFrom":[makeQuery(id+"F1.opExtrude","SWEPT_FACE",FACE,{"disambiguationData":[OSD([sQuery(id+"F0.wireOp",EDGE,"E0")])]}),makeQuery(id+"F5.opExtrude","SWEPT_FACE",FACE,{"disambiguationData":[OSD([sQuery(id+"F4.wireOp",EDGE,"E14")])]})]});
            var Q265;
            Q265=makeQuery(id+"F12.boolean.opBoolean","INTERSECT",EDGE,{"derivedFrom":[makeQuery(id+"F1.opExtrude","SWEPT_FACE",FACE,{"disambiguationData":[OSD([sQuery(id+"F0.wireOp",EDGE,"E0")])]}),makeQuery(id+"F12.opExtrude","SWEPT_FACE",FACE,{"disambiguationData":[OSD([sQuery(id+"F11.wireOp",EDGE,"E443")])]})]});
            var Q266;
            Q266=makeQuery(id+"F12.boolean.opBoolean","INTERSECT",EDGE,{"derivedFrom":[makeQuery(id+"F1.opExtrude","SWEPT_FACE",FACE,{"disambiguationData":[OSD([sQuery(id+"F0.wireOp",EDGE,"E0")])]}),makeQuery(id+"F12.opExtrude","SWEPT_FACE",FACE,{"disambiguationData":[OSD([sQuery(id+"F11.wireOp",EDGE,"E444")])]})]});
            var Q267;
            Q267=makeQuery(id+"F12.boolean.opBoolean","INTERSECT",EDGE,{"derivedFrom":[makeQuery(id+"F1.opExtrude","SWEPT_FACE",FACE,{"disambiguationData":[OSD([sQuery(id+"F0.wireOp",EDGE,"E0")])]}),makeQuery(id+"F12.opExtrude","SWEPT_FACE",FACE,{"disambiguationData":[OSD([sQuery(id+"F11.wireOp",EDGE,"E445")])]})]});
            var Q268;
            Q268=makeQuery(id+"F12.boolean.opBoolean","INTERSECT",EDGE,{"derivedFrom":[makeQuery(id+"F1.opExtrude","SWEPT_FACE",FACE,{"disambiguationData":[OSD([sQuery(id+"F0.wireOp",EDGE,"E0")])]}),makeQuery(id+"F12.opExtrude","SWEPT_FACE",FACE,{"disambiguationData":[OSD([sQuery(id+"F11.wireOp",EDGE,"E446")])]})]});
            var Q269;
            Q269=makeQuery(id+"F12.boolean.opBoolean","INTERSECT",EDGE,{"derivedFrom":[makeQuery(id+"F1.opExtrude","SWEPT_FACE",FACE,{"disambiguationData":[OSD([sQuery(id+"F0.wireOp",EDGE,"E0")])]}),makeQuery(id+"F12.opExtrude","SWEPT_FACE",FACE,{"disambiguationData":[OSD([sQuery(id+"F11.wireOp",EDGE,"E441")])]})]});
            var Q270;
            Q270=makeQuery(id+"F12.boolean.opBoolean","INTERSECT",EDGE,{"derivedFrom":[makeQuery(id+"F1.opExtrude","SWEPT_FACE",FACE,{"disambiguationData":[OSD([sQuery(id+"F0.wireOp",EDGE,"E0")])]}),makeQuery(id+"F12.opExtrude","SWEPT_FACE",FACE,{"disambiguationData":[OSD([sQuery(id+"F11.wireOp",EDGE,"E442")])]})]});
            var Q271;
            Q271=makeQuery(id+"F12.boolean.opBoolean","INTERSECT",EDGE,{"derivedFrom":[makeQuery(id+"F1.opExtrude","SWEPT_FACE",FACE,{"disambiguationData":[OSD([sQuery(id+"F0.wireOp",EDGE,"E0")])]}),makeQuery(id+"F12.opExtrude","SWEPT_FACE",FACE,{"disambiguationData":[OSD([sQuery(id+"F11.wireOp",EDGE,"E445")])]})]});
            var Q272;
            Q272=makeQuery(id+"F12.boolean.opBoolean","INTERSECT",EDGE,{"derivedFrom":[makeQuery(id+"F1.opExtrude","SWEPT_FACE",FACE,{"disambiguationData":[OSD([sQuery(id+"F0.wireOp",EDGE,"E0")])]}),makeQuery(id+"F12.opExtrude","SWEPT_FACE",FACE,{"disambiguationData":[OSD([sQuery(id+"F11.wireOp",EDGE,"E463")])]})]});
            var Q273;
            Q273=makeQuery(id+"F12.boolean.opBoolean","INTERSECT",EDGE,{"derivedFrom":[makeQuery(id+"F1.opExtrude","SWEPT_FACE",FACE,{"disambiguationData":[OSD([sQuery(id+"F0.wireOp",EDGE,"E0")])]}),makeQuery(id+"F12.opExtrude","SWEPT_FACE",FACE,{"disambiguationData":[OSD([sQuery(id+"F11.wireOp",EDGE,"E464")])]})]});
            var Q274;
            Q274=makeQuery(id+"F12.boolean.opBoolean","INTERSECT",EDGE,{"derivedFrom":[makeQuery(id+"F1.opExtrude","SWEPT_FACE",FACE,{"disambiguationData":[OSD([sQuery(id+"F0.wireOp",EDGE,"E0")])]}),makeQuery(id+"F12.opExtrude","SWEPT_FACE",FACE,{"disambiguationData":[OSD([sQuery(id+"F11.wireOp",EDGE,"E459")])]})]});
            var Q275;
            Q275=makeQuery(id+"F12.boolean.opBoolean","INTERSECT",EDGE,{"derivedFrom":[makeQuery(id+"F1.opExtrude","SWEPT_FACE",FACE,{"disambiguationData":[OSD([sQuery(id+"F0.wireOp",EDGE,"E0")])]}),makeQuery(id+"F12.opExtrude","SWEPT_FACE",FACE,{"disambiguationData":[OSD([sQuery(id+"F11.wireOp",EDGE,"E460")])]})]});
            var Q276;
            Q276=makeQuery(id+"F12.boolean.opBoolean","INTERSECT",EDGE,{"derivedFrom":[makeQuery(id+"F1.opExtrude","SWEPT_FACE",FACE,{"disambiguationData":[OSD([sQuery(id+"F0.wireOp",EDGE,"E0")])]}),makeQuery(id+"F12.opExtrude","SWEPT_FACE",FACE,{"disambiguationData":[OSD([sQuery(id+"F11.wireOp",EDGE,"E461")])]})]});
            var Q277;
            Q277=makeQuery(id+"F12.boolean.opBoolean","INTERSECT",EDGE,{"derivedFrom":[makeQuery(id+"F1.opExtrude","SWEPT_FACE",FACE,{"disambiguationData":[OSD([sQuery(id+"F0.wireOp",EDGE,"E0")])]}),makeQuery(id+"F12.opExtrude","SWEPT_FACE",FACE,{"disambiguationData":[OSD([sQuery(id+"F11.wireOp",EDGE,"E462")])]})]});
            var Q278;
            Q278=makeQuery(id+"F12.boolean.opBoolean","INTERSECT",EDGE,{"derivedFrom":[makeQuery(id+"F1.opExtrude","SWEPT_FACE",FACE,{"disambiguationData":[OSD([sQuery(id+"F0.wireOp",EDGE,"E0")])]}),makeQuery(id+"F12.opExtrude","SWEPT_FACE",FACE,{"disambiguationData":[OSD([sQuery(id+"F11.wireOp",EDGE,"E497")])]})]});
            var Q279;
            Q279=makeQuery(id+"F12.boolean.opBoolean","INTERSECT",EDGE,{"derivedFrom":[makeQuery(id+"F1.opExtrude","SWEPT_FACE",FACE,{"disambiguationData":[OSD([sQuery(id+"F0.wireOp",EDGE,"E0")])]}),makeQuery(id+"F12.opExtrude","SWEPT_FACE",FACE,{"disambiguationData":[OSD([sQuery(id+"F11.wireOp",EDGE,"E498")])]})]});
            var Q280;
            Q280=makeQuery(id+"F12.boolean.opBoolean","INTERSECT",EDGE,{"derivedFrom":[makeQuery(id+"F1.opExtrude","SWEPT_FACE",FACE,{"disambiguationData":[OSD([sQuery(id+"F0.wireOp",EDGE,"E0")])]}),makeQuery(id+"F12.opExtrude","SWEPT_FACE",FACE,{"disambiguationData":[OSD([sQuery(id+"F11.wireOp",EDGE,"E499")])]})]});
            var Q281;
            Q281=makeQuery(id+"F12.boolean.opBoolean","INTERSECT",EDGE,{"derivedFrom":[makeQuery(id+"F1.opExtrude","SWEPT_FACE",FACE,{"disambiguationData":[OSD([sQuery(id+"F0.wireOp",EDGE,"E0")])]}),makeQuery(id+"F12.opExtrude","SWEPT_FACE",FACE,{"disambiguationData":[OSD([sQuery(id+"F11.wireOp",EDGE,"E500")])]})]});
            var Q282;
            Q282=makeQuery(id+"F12.boolean.opBoolean","INTERSECT",EDGE,{"derivedFrom":[makeQuery(id+"F1.opExtrude","SWEPT_FACE",FACE,{"disambiguationData":[OSD([sQuery(id+"F0.wireOp",EDGE,"E0")])]}),makeQuery(id+"F12.opExtrude","SWEPT_FACE",FACE,{"disambiguationData":[OSD([sQuery(id+"F11.wireOp",EDGE,"E495")])]})]});
            var Q283;
            Q283=makeQuery(id+"F12.boolean.opBoolean","INTERSECT",EDGE,{"derivedFrom":[makeQuery(id+"F1.opExtrude","SWEPT_FACE",FACE,{"disambiguationData":[OSD([sQuery(id+"F0.wireOp",EDGE,"E0")])]}),makeQuery(id+"F12.opExtrude","SWEPT_FACE",FACE,{"disambiguationData":[OSD([sQuery(id+"F11.wireOp",EDGE,"E496")])]})]});
            var Q284;
            Q284=makeQuery(id+"F12.boolean.opBoolean","INTERSECT",EDGE,{"derivedFrom":[makeQuery(id+"F1.opExtrude","SWEPT_FACE",FACE,{"disambiguationData":[OSD([sQuery(id+"F0.wireOp",EDGE,"E0")])]}),makeQuery(id+"F12.opExtrude","SWEPT_FACE",FACE,{"disambiguationData":[OSD([sQuery(id+"F11.wireOp",EDGE,"E482")])]})]});
            var Q285;
            Q285=makeQuery(id+"F12.boolean.opBoolean","INTERSECT",EDGE,{"derivedFrom":[makeQuery(id+"F1.opExtrude","SWEPT_FACE",FACE,{"disambiguationData":[OSD([sQuery(id+"F0.wireOp",EDGE,"E0")])]}),makeQuery(id+"F12.opExtrude","SWEPT_FACE",FACE,{"disambiguationData":[OSD([sQuery(id+"F11.wireOp",EDGE,"E481")])]})]});
            var Q286;
            Q286=makeQuery(id+"F12.boolean.opBoolean","INTERSECT",EDGE,{"derivedFrom":[makeQuery(id+"F1.opExtrude","SWEPT_FACE",FACE,{"disambiguationData":[OSD([sQuery(id+"F0.wireOp",EDGE,"E0")])]}),makeQuery(id+"F12.opExtrude","SWEPT_FACE",FACE,{"disambiguationData":[OSD([sQuery(id+"F11.wireOp",EDGE,"E480")])]})]});
            var Q287;
            Q287=makeQuery(id+"F12.boolean.opBoolean","INTERSECT",EDGE,{"derivedFrom":[makeQuery(id+"F1.opExtrude","SWEPT_FACE",FACE,{"disambiguationData":[OSD([sQuery(id+"F0.wireOp",EDGE,"E0")])]}),makeQuery(id+"F12.opExtrude","SWEPT_FACE",FACE,{"disambiguationData":[OSD([sQuery(id+"F11.wireOp",EDGE,"E479")])]})]});
            var Q288;
            Q288=makeQuery(id+"F12.boolean.opBoolean","INTERSECT",EDGE,{"derivedFrom":[makeQuery(id+"F1.opExtrude","SWEPT_FACE",FACE,{"disambiguationData":[OSD([sQuery(id+"F0.wireOp",EDGE,"E0")])]}),makeQuery(id+"F12.opExtrude","SWEPT_FACE",FACE,{"disambiguationData":[OSD([sQuery(id+"F11.wireOp",EDGE,"E478")])]})]});
            var Q289;
            Q289=makeQuery(id+"F12.boolean.opBoolean","INTERSECT",EDGE,{"derivedFrom":[makeQuery(id+"F1.opExtrude","SWEPT_FACE",FACE,{"disambiguationData":[OSD([sQuery(id+"F0.wireOp",EDGE,"E0")])]}),makeQuery(id+"F12.opExtrude","SWEPT_FACE",FACE,{"disambiguationData":[OSD([sQuery(id+"F11.wireOp",EDGE,"E477")])]})]});
            var Q290;
            Q290=makeQuery(id+"F12.boolean.opBoolean","INTERSECT",EDGE,{"derivedFrom":[makeQuery(id+"F1.opExtrude","SWEPT_FACE",FACE,{"disambiguationData":[OSD([sQuery(id+"F0.wireOp",EDGE,"E0")])]}),makeQuery(id+"F12.opExtrude","SWEPT_FACE",FACE,{"disambiguationData":[OSD([sQuery(id+"F11.wireOp",EDGE,"E515")])]})]});
            var Q291;
            Q291=makeQuery(id+"F12.boolean.opBoolean","INTERSECT",EDGE,{"derivedFrom":[makeQuery(id+"F1.opExtrude","SWEPT_FACE",FACE,{"disambiguationData":[OSD([sQuery(id+"F0.wireOp",EDGE,"E0")])]}),makeQuery(id+"F12.opExtrude","SWEPT_FACE",FACE,{"disambiguationData":[OSD([sQuery(id+"F11.wireOp",EDGE,"E514")])]})]});
            var Q292;
            Q292=makeQuery(id+"F12.boolean.opBoolean","INTERSECT",EDGE,{"derivedFrom":[makeQuery(id+"F1.opExtrude","SWEPT_FACE",FACE,{"disambiguationData":[OSD([sQuery(id+"F0.wireOp",EDGE,"E0")])]}),makeQuery(id+"F12.opExtrude","SWEPT_FACE",FACE,{"disambiguationData":[OSD([sQuery(id+"F11.wireOp",EDGE,"E518")])]})]});
            var Q293;
            Q293=makeQuery(id+"F12.boolean.opBoolean","INTERSECT",EDGE,{"derivedFrom":[makeQuery(id+"F1.opExtrude","SWEPT_FACE",FACE,{"disambiguationData":[OSD([sQuery(id+"F0.wireOp",EDGE,"E0")])]}),makeQuery(id+"F12.opExtrude","SWEPT_FACE",FACE,{"disambiguationData":[OSD([sQuery(id+"F11.wireOp",EDGE,"E517")])]})]});
            var Q294;
            Q294=makeQuery(id+"F12.boolean.opBoolean","INTERSECT",EDGE,{"derivedFrom":[makeQuery(id+"F1.opExtrude","SWEPT_FACE",FACE,{"disambiguationData":[OSD([sQuery(id+"F0.wireOp",EDGE,"E0")])]}),makeQuery(id+"F12.opExtrude","SWEPT_FACE",FACE,{"disambiguationData":[OSD([sQuery(id+"F11.wireOp",EDGE,"E516")])]})]});
            var Q295;
            Q295=makeQuery(id+"F12.boolean.opBoolean","INTERSECT",EDGE,{"derivedFrom":[makeQuery(id+"F1.opExtrude","SWEPT_FACE",FACE,{"disambiguationData":[OSD([sQuery(id+"F0.wireOp",EDGE,"E0")])]}),makeQuery(id+"F12.opExtrude","SWEPT_FACE",FACE,{"disambiguationData":[OSD([sQuery(id+"F11.wireOp",EDGE,"E513")])]})]});
            var Q296;
            Q296=makeQuery(id+"F12.boolean.opBoolean","INTERSECT",EDGE,{"derivedFrom":[makeQuery(id+"F1.opExtrude","SWEPT_FACE",FACE,{"disambiguationData":[OSD([sQuery(id+"F0.wireOp",EDGE,"E0")])]}),makeQuery(id+"F12.opExtrude","SWEPT_FACE",FACE,{"disambiguationData":[OSD([sQuery(id+"F11.wireOp",EDGE,"E533")])]})]});
            var Q297;
            Q297=makeQuery(id+"F12.boolean.opBoolean","INTERSECT",EDGE,{"derivedFrom":[makeQuery(id+"F1.opExtrude","SWEPT_FACE",FACE,{"disambiguationData":[OSD([sQuery(id+"F0.wireOp",EDGE,"E0")])]}),makeQuery(id+"F12.opExtrude","SWEPT_FACE",FACE,{"disambiguationData":[OSD([sQuery(id+"F11.wireOp",EDGE,"E532")])]})]});
            var Q298;
            Q298=makeQuery(id+"F12.boolean.opBoolean","INTERSECT",EDGE,{"derivedFrom":[makeQuery(id+"F1.opExtrude","SWEPT_FACE",FACE,{"disambiguationData":[OSD([sQuery(id+"F0.wireOp",EDGE,"E0")])]}),makeQuery(id+"F12.opExtrude","SWEPT_FACE",FACE,{"disambiguationData":[OSD([sQuery(id+"F11.wireOp",EDGE,"E531")])]})]});
            var Q299;
            Q299=makeQuery(id+"F12.boolean.opBoolean","INTERSECT",EDGE,{"derivedFrom":[makeQuery(id+"F1.opExtrude","SWEPT_FACE",FACE,{"disambiguationData":[OSD([sQuery(id+"F0.wireOp",EDGE,"E0")])]}),makeQuery(id+"F12.opExtrude","SWEPT_FACE",FACE,{"disambiguationData":[OSD([sQuery(id+"F11.wireOp",EDGE,"E536")])]})]});
            var Q300;
            Q300=makeQuery(id+"F12.boolean.opBoolean","INTERSECT",EDGE,{"derivedFrom":[makeQuery(id+"F1.opExtrude","SWEPT_FACE",FACE,{"disambiguationData":[OSD([sQuery(id+"F0.wireOp",EDGE,"E0")])]}),makeQuery(id+"F12.opExtrude","SWEPT_FACE",FACE,{"disambiguationData":[OSD([sQuery(id+"F11.wireOp",EDGE,"E535")])]})]});
            var Q301;
            Q301=makeQuery(id+"F12.boolean.opBoolean","INTERSECT",EDGE,{"derivedFrom":[makeQuery(id+"F1.opExtrude","SWEPT_FACE",FACE,{"disambiguationData":[OSD([sQuery(id+"F0.wireOp",EDGE,"E0")])]}),makeQuery(id+"F12.opExtrude","SWEPT_FACE",FACE,{"disambiguationData":[OSD([sQuery(id+"F11.wireOp",EDGE,"E534")])]})]});
            var Q302;
            Q302=makeQuery(id+"F12.boolean.opBoolean","INTERSECT",EDGE,{"derivedFrom":[makeQuery(id+"F1.opExtrude","SWEPT_FACE",FACE,{"disambiguationData":[OSD([sQuery(id+"F0.wireOp",EDGE,"E0")])]}),makeQuery(id+"F12.opExtrude","SWEPT_FACE",FACE,{"disambiguationData":[OSD([sQuery(id+"F11.wireOp",EDGE,"E551")])]})]});
            var Q303;
            Q303=makeQuery(id+"F12.boolean.opBoolean","INTERSECT",EDGE,{"derivedFrom":[makeQuery(id+"F1.opExtrude","SWEPT_FACE",FACE,{"disambiguationData":[OSD([sQuery(id+"F0.wireOp",EDGE,"E0")])]}),makeQuery(id+"F12.opExtrude","SWEPT_FACE",FACE,{"disambiguationData":[OSD([sQuery(id+"F11.wireOp",EDGE,"E552")])]})]});
            var Q304;
            Q304=makeQuery(id+"F12.boolean.opBoolean","INTERSECT",EDGE,{"derivedFrom":[makeQuery(id+"F1.opExtrude","SWEPT_FACE",FACE,{"disambiguationData":[OSD([sQuery(id+"F0.wireOp",EDGE,"E0")])]}),makeQuery(id+"F12.opExtrude","SWEPT_FACE",FACE,{"disambiguationData":[OSD([sQuery(id+"F11.wireOp",EDGE,"E553")])]})]});
            var Q305;
            Q305=makeQuery(id+"F12.boolean.opBoolean","INTERSECT",EDGE,{"derivedFrom":[makeQuery(id+"F1.opExtrude","SWEPT_FACE",FACE,{"disambiguationData":[OSD([sQuery(id+"F0.wireOp",EDGE,"E0")])]}),makeQuery(id+"F12.opExtrude","SWEPT_FACE",FACE,{"disambiguationData":[OSD([sQuery(id+"F11.wireOp",EDGE,"E554")])]})]});
            var Q306;
            Q306=makeQuery(id+"F12.boolean.opBoolean","INTERSECT",EDGE,{"derivedFrom":[makeQuery(id+"F1.opExtrude","SWEPT_FACE",FACE,{"disambiguationData":[OSD([sQuery(id+"F0.wireOp",EDGE,"E0")])]}),makeQuery(id+"F12.opExtrude","SWEPT_FACE",FACE,{"disambiguationData":[OSD([sQuery(id+"F11.wireOp",EDGE,"E549")])]})]});
            var Q307;
            Q307=makeQuery(id+"F12.boolean.opBoolean","INTERSECT",EDGE,{"derivedFrom":[makeQuery(id+"F1.opExtrude","SWEPT_FACE",FACE,{"disambiguationData":[OSD([sQuery(id+"F0.wireOp",EDGE,"E0")])]}),makeQuery(id+"F12.opExtrude","SWEPT_FACE",FACE,{"disambiguationData":[OSD([sQuery(id+"F11.wireOp",EDGE,"E550")])]})]});
            var Q308;
            Q308=makeQuery(id+"F12.boolean.opBoolean","INTERSECT",EDGE,{"derivedFrom":[makeQuery(id+"F1.opExtrude","SWEPT_FACE",FACE,{"disambiguationData":[OSD([sQuery(id+"F0.wireOp",EDGE,"E0")])]}),makeQuery(id+"F12.opExtrude","SWEPT_FACE",FACE,{"disambiguationData":[OSD([sQuery(id+"F11.wireOp",EDGE,"6ca8cd86-5e60-4f71-aece-58a5cefb0301")])]})]});
            var Q309;
            Q309=makeQuery(id+"F12.boolean.opBoolean","INTERSECT",EDGE,{"derivedFrom":[makeQuery(id+"F1.opExtrude","SWEPT_FACE",FACE,{"disambiguationData":[OSD([sQuery(id+"F0.wireOp",EDGE,"E0")])]}),makeQuery(id+"F12.opExtrude","SWEPT_FACE",FACE,{"disambiguationData":[OSD([sQuery(id+"F11.wireOp",EDGE,"66b1be52-5d7b-488e-ab88-be7fc1489788")])]})]});
            var Q310;
            Q310=makeQuery(id+"F12.boolean.opBoolean","INTERSECT",EDGE,{"derivedFrom":[makeQuery(id+"F1.opExtrude","SWEPT_FACE",FACE,{"disambiguationData":[OSD([sQuery(id+"F0.wireOp",EDGE,"E0")])]}),makeQuery(id+"F12.opExtrude","SWEPT_FACE",FACE,{"disambiguationData":[OSD([sQuery(id+"F11.wireOp",EDGE,"a826e480-ba9d-454b-a154-b724fcca502a")])]})]});
            var Q311;
            Q311=makeQuery(id+"F12.boolean.opBoolean","INTERSECT",EDGE,{"derivedFrom":[makeQuery(id+"F1.opExtrude","SWEPT_FACE",FACE,{"disambiguationData":[OSD([sQuery(id+"F0.wireOp",EDGE,"E0")])]}),makeQuery(id+"F12.opExtrude","SWEPT_FACE",FACE,{"disambiguationData":[OSD([sQuery(id+"F11.wireOp",EDGE,"07a74ef0-9ede-4776-8ebf-e754756c114a")])]})]});
            var Q312;
            Q312=makeQuery(id+"F12.boolean.opBoolean","INTERSECT",EDGE,{"derivedFrom":[makeQuery(id+"F1.opExtrude","SWEPT_FACE",FACE,{"disambiguationData":[OSD([sQuery(id+"F0.wireOp",EDGE,"E0")])]}),makeQuery(id+"F12.opExtrude","SWEPT_FACE",FACE,{"disambiguationData":[OSD([sQuery(id+"F11.wireOp",EDGE,"092ed403-3d4f-4c15-960d-c10ef8789eb5")])]})]});
            var Q313;
            Q313=makeQuery(id+"F12.boolean.opBoolean","INTERSECT",EDGE,{"derivedFrom":[makeQuery(id+"F1.opExtrude","SWEPT_FACE",FACE,{"disambiguationData":[OSD([sQuery(id+"F0.wireOp",EDGE,"E0")])]}),makeQuery(id+"F12.opExtrude","SWEPT_FACE",FACE,{"disambiguationData":[OSD([sQuery(id+"F11.wireOp",EDGE,"acb8dcbc-daed-461c-af8b-853c71a07eac")])]})]});
            var Q314;
            Q314=makeQuery(id+"F12.boolean.opBoolean","INTERSECT",EDGE,{"derivedFrom":[makeQuery(id+"F1.opExtrude","SWEPT_FACE",FACE,{"disambiguationData":[OSD([sQuery(id+"F0.wireOp",EDGE,"E0")])]}),makeQuery(id+"F12.opExtrude","SWEPT_FACE",FACE,{"disambiguationData":[OSD([sQuery(id+"F11.wireOp",EDGE,"76158571-8428-4aec-bd47-33adf174f2a4")])]})]});
            var Q315;
            Q315=makeQuery(id+"F12.boolean.opBoolean","INTERSECT",EDGE,{"derivedFrom":[makeQuery(id+"F1.opExtrude","SWEPT_FACE",FACE,{"disambiguationData":[OSD([sQuery(id+"F0.wireOp",EDGE,"E0")])]}),makeQuery(id+"F12.opExtrude","SWEPT_FACE",FACE,{"disambiguationData":[OSD([sQuery(id+"F11.wireOp",EDGE,"2e92792f-4c7e-4468-9ae2-ab93ba844d4b")])]})]});
            var Q316;
            Q316=makeQuery(id+"F12.boolean.opBoolean","INTERSECT",EDGE,{"derivedFrom":[makeQuery(id+"F1.opExtrude","SWEPT_FACE",FACE,{"disambiguationData":[OSD([sQuery(id+"F0.wireOp",EDGE,"E0")])]}),makeQuery(id+"F12.opExtrude","SWEPT_FACE",FACE,{"disambiguationData":[OSD([sQuery(id+"F11.wireOp",EDGE,"b0197f1f-3212-4fe7-853f-974a1a9ee185")])]})]});
            var Q317;
            Q317=makeQuery(id+"F12.boolean.opBoolean","INTERSECT",EDGE,{"derivedFrom":[makeQuery(id+"F1.opExtrude","SWEPT_FACE",FACE,{"disambiguationData":[OSD([sQuery(id+"F0.wireOp",EDGE,"E0")])]}),makeQuery(id+"F12.opExtrude","SWEPT_FACE",FACE,{"disambiguationData":[OSD([sQuery(id+"F11.wireOp",EDGE,"faa93db1-9b94-4bc8-a4df-a69461af7118")])]})]});
            var Q318;
            Q318=makeQuery(id+"F12.boolean.opBoolean","INTERSECT",EDGE,{"derivedFrom":[makeQuery(id+"F1.opExtrude","SWEPT_FACE",FACE,{"disambiguationData":[OSD([sQuery(id+"F0.wireOp",EDGE,"E0")])]}),makeQuery(id+"F12.opExtrude","SWEPT_FACE",FACE,{"disambiguationData":[OSD([sQuery(id+"F11.wireOp",EDGE,"bf553eab-f362-4974-a638-a7733928a928")])]})]});
            var Q319;
            Q319=makeQuery(id+"F12.boolean.opBoolean","INTERSECT",EDGE,{"derivedFrom":[makeQuery(id+"F1.opExtrude","SWEPT_FACE",FACE,{"disambiguationData":[OSD([sQuery(id+"F0.wireOp",EDGE,"E0")])]}),makeQuery(id+"F12.opExtrude","SWEPT_FACE",FACE,{"disambiguationData":[OSD([sQuery(id+"F11.wireOp",EDGE,"80697549-b82d-4dee-9442-59f5951ca8b8")])]})]});
            var Q320;
            Q320=makeQuery(id+"F12.boolean.opBoolean","INTERSECT",EDGE,{"derivedFrom":[makeQuery(id+"F1.opExtrude","SWEPT_FACE",FACE,{"disambiguationData":[OSD([sQuery(id+"F0.wireOp",EDGE,"E0")])]}),makeQuery(id+"F12.opExtrude","SWEPT_FACE",FACE,{"disambiguationData":[OSD([sQuery(id+"F11.wireOp",EDGE,"0e8c3faf-8d29-4084-8698-73abd46cf39c")])]})]});
            var Q321;
            Q321=makeQuery(id+"F12.boolean.opBoolean","INTERSECT",EDGE,{"derivedFrom":[makeQuery(id+"F1.opExtrude","SWEPT_FACE",FACE,{"disambiguationData":[OSD([sQuery(id+"F0.wireOp",EDGE,"E0")])]}),makeQuery(id+"F12.opExtrude","SWEPT_FACE",FACE,{"disambiguationData":[OSD([sQuery(id+"F11.wireOp",EDGE,"2d858d98-3365-4601-99b5-01ed8230ce64")])]})]});
            var Q322;
            Q322=makeQuery(id+"F12.boolean.opBoolean","INTERSECT",EDGE,{"derivedFrom":[makeQuery(id+"F1.opExtrude","SWEPT_FACE",FACE,{"disambiguationData":[OSD([sQuery(id+"F0.wireOp",EDGE,"E0")])]}),makeQuery(id+"F12.opExtrude","SWEPT_FACE",FACE,{"disambiguationData":[OSD([sQuery(id+"F11.wireOp",EDGE,"6bbfbd9f-83cf-4e5a-8c48-5f02fa0a9c69")])]})]});
            var Q323;
            Q323=makeQuery(id+"F12.boolean.opBoolean","INTERSECT",EDGE,{"derivedFrom":[makeQuery(id+"F1.opExtrude","SWEPT_FACE",FACE,{"disambiguationData":[OSD([sQuery(id+"F0.wireOp",EDGE,"E0")])]}),makeQuery(id+"F12.opExtrude","SWEPT_FACE",FACE,{"disambiguationData":[OSD([sQuery(id+"F11.wireOp",EDGE,"8a950ba1-a090-4c8d-82b9-cd5225b2b9e3")])]})]});
            var Q324;
            Q324=makeQuery(id+"F12.boolean.opBoolean","INTERSECT",EDGE,{"derivedFrom":[makeQuery(id+"F1.opExtrude","SWEPT_FACE",FACE,{"disambiguationData":[OSD([sQuery(id+"F0.wireOp",EDGE,"E0")])]}),makeQuery(id+"F12.opExtrude","SWEPT_FACE",FACE,{"disambiguationData":[OSD([sQuery(id+"F11.wireOp",EDGE,"de11c3ef-7a1d-4805-b947-306e5608d462")])]})]});
            var Q325;
            Q325=makeQuery(id+"F12.boolean.opBoolean","INTERSECT",EDGE,{"derivedFrom":[makeQuery(id+"F1.opExtrude","SWEPT_FACE",FACE,{"disambiguationData":[OSD([sQuery(id+"F0.wireOp",EDGE,"E0")])]}),makeQuery(id+"F12.opExtrude","SWEPT_FACE",FACE,{"disambiguationData":[OSD([sQuery(id+"F11.wireOp",EDGE,"5fc31a4b-0bb3-428e-9063-e62cabce7d17")])]})]});
            var Q326;
            Q326=makeQuery(id+"F12.boolean.opBoolean","INTERSECT",EDGE,{"derivedFrom":[makeQuery(id+"F1.opExtrude","SWEPT_FACE",FACE,{"disambiguationData":[OSD([sQuery(id+"F0.wireOp",EDGE,"E0")])]}),makeQuery(id+"F12.opExtrude","SWEPT_FACE",FACE,{"disambiguationData":[OSD([sQuery(id+"F11.wireOp",EDGE,"2fde0330-21a3-47f8-95e4-c6b2125bc28d")])]})]});
            var Q327;
            Q327=makeQuery(id+"F12.boolean.opBoolean","INTERSECT",EDGE,{"derivedFrom":[makeQuery(id+"F1.opExtrude","SWEPT_FACE",FACE,{"disambiguationData":[OSD([sQuery(id+"F0.wireOp",EDGE,"E0")])]}),makeQuery(id+"F12.opExtrude","SWEPT_FACE",FACE,{"disambiguationData":[OSD([sQuery(id+"F11.wireOp",EDGE,"39ea25aa-dc9d-413d-aca9-5b751d16431b")])]})]});
            var Q328;
            Q328=makeQuery(id+"F12.boolean.opBoolean","INTERSECT",EDGE,{"derivedFrom":[makeQuery(id+"F1.opExtrude","SWEPT_FACE",FACE,{"disambiguationData":[OSD([sQuery(id+"F0.wireOp",EDGE,"E0")])]}),makeQuery(id+"F12.opExtrude","SWEPT_FACE",FACE,{"disambiguationData":[OSD([sQuery(id+"F11.wireOp",EDGE,"45a08d57-ac6c-4e91-8221-61a5d03ef4d8")])]})]});
            var Q329;
            Q329=makeQuery(id+"F12.boolean.opBoolean","INTERSECT",EDGE,{"derivedFrom":[makeQuery(id+"F1.opExtrude","SWEPT_FACE",FACE,{"disambiguationData":[OSD([sQuery(id+"F0.wireOp",EDGE,"E0")])]}),makeQuery(id+"F12.opExtrude","SWEPT_FACE",FACE,{"disambiguationData":[OSD([sQuery(id+"F11.wireOp",EDGE,"ae00799b-1def-4a87-a375-c2745601d105")])]})]});
            var Q330;
            Q330=makeQuery(id+"F12.boolean.opBoolean","INTERSECT",EDGE,{"derivedFrom":[makeQuery(id+"F1.opExtrude","SWEPT_FACE",FACE,{"disambiguationData":[OSD([sQuery(id+"F0.wireOp",EDGE,"E0")])]}),makeQuery(id+"F12.opExtrude","SWEPT_FACE",FACE,{"disambiguationData":[OSD([sQuery(id+"F11.wireOp",EDGE,"04f7a225-5764-4d5d-9f0d-af1fe46beb71")])]})]});
            var Q331;
            Q331=makeQuery(id+"F12.boolean.opBoolean","INTERSECT",EDGE,{"derivedFrom":[makeQuery(id+"F1.opExtrude","SWEPT_FACE",FACE,{"disambiguationData":[OSD([sQuery(id+"F0.wireOp",EDGE,"E0")])]}),makeQuery(id+"F12.opExtrude","SWEPT_FACE",FACE,{"disambiguationData":[OSD([sQuery(id+"F11.wireOp",EDGE,"874c3c57-a6bb-4400-9591-b6c49b54f0d5")])]})]});
            var Q332;
            Q332=makeQuery(id+"F12.boolean.opBoolean","INTERSECT",EDGE,{"derivedFrom":[makeQuery(id+"F1.opExtrude","SWEPT_FACE",FACE,{"disambiguationData":[OSD([sQuery(id+"F0.wireOp",EDGE,"E0")])]}),makeQuery(id+"F12.opExtrude","SWEPT_FACE",FACE,{"disambiguationData":[OSD([sQuery(id+"F11.wireOp",EDGE,"46c9ed28-b344-407f-a562-7c22284d55fe")])]})]});
            var Q333;
            Q333=makeQuery(id+"F12.boolean.opBoolean","INTERSECT",EDGE,{"derivedFrom":[makeQuery(id+"F1.opExtrude","SWEPT_FACE",FACE,{"disambiguationData":[OSD([sQuery(id+"F0.wireOp",EDGE,"E0")])]}),makeQuery(id+"F12.opExtrude","SWEPT_FACE",FACE,{"disambiguationData":[OSD([sQuery(id+"F11.wireOp",EDGE,"62da7513-9491-427f-938b-696b47152ffd")])]})]});
            var Q334;
            Q334=makeQuery(id+"F12.boolean.opBoolean","INTERSECT",EDGE,{"derivedFrom":[makeQuery(id+"F1.opExtrude","SWEPT_FACE",FACE,{"disambiguationData":[OSD([sQuery(id+"F0.wireOp",EDGE,"E0")])]}),makeQuery(id+"F12.opExtrude","SWEPT_FACE",FACE,{"disambiguationData":[OSD([sQuery(id+"F11.wireOp",EDGE,"aa06bcb9-a86b-4f86-a9b4-85c86a1af446")])]})]});
            var Q335;
            Q335=makeQuery(id+"F12.boolean.opBoolean","INTERSECT",EDGE,{"derivedFrom":[makeQuery(id+"F1.opExtrude","SWEPT_FACE",FACE,{"disambiguationData":[OSD([sQuery(id+"F0.wireOp",EDGE,"E0")])]}),makeQuery(id+"F12.opExtrude","SWEPT_FACE",FACE,{"disambiguationData":[OSD([sQuery(id+"F11.wireOp",EDGE,"39fdaf24-626d-4be9-ae9c-25e924fe0a02")])]})]});
            var Q336;
            Q336=makeQuery(id+"F12.boolean.opBoolean","INTERSECT",EDGE,{"derivedFrom":[makeQuery(id+"F1.opExtrude","SWEPT_FACE",FACE,{"disambiguationData":[OSD([sQuery(id+"F0.wireOp",EDGE,"E0")])]}),makeQuery(id+"F12.opExtrude","SWEPT_FACE",FACE,{"disambiguationData":[OSD([sQuery(id+"F11.wireOp",EDGE,"25193117-9b4b-42b4-a85a-958f9bb3fb66")])]})]});
            var Q337;
            Q337=makeQuery(id+"F12.boolean.opBoolean","INTERSECT",EDGE,{"derivedFrom":[makeQuery(id+"F1.opExtrude","SWEPT_FACE",FACE,{"disambiguationData":[OSD([sQuery(id+"F0.wireOp",EDGE,"E0")])]}),makeQuery(id+"F12.opExtrude","SWEPT_FACE",FACE,{"disambiguationData":[OSD([sQuery(id+"F11.wireOp",EDGE,"2c336ab2-bfc0-43d3-a329-a216c8d1b87b")])]})]});
            var Q338;
            Q338=makeQuery(id+"F12.boolean.opBoolean","INTERSECT",EDGE,{"derivedFrom":[makeQuery(id+"F1.opExtrude","SWEPT_FACE",FACE,{"disambiguationData":[OSD([sQuery(id+"F0.wireOp",EDGE,"E0")])]}),makeQuery(id+"F12.opExtrude","SWEPT_FACE",FACE,{"disambiguationData":[OSD([sQuery(id+"F11.wireOp",EDGE,"64d6da3b-8a0c-46ea-a12b-d14f425ae2f6")])]})]});
            var Q339;
            Q339=makeQuery(id+"F12.boolean.opBoolean","INTERSECT",EDGE,{"derivedFrom":[makeQuery(id+"F1.opExtrude","SWEPT_FACE",FACE,{"disambiguationData":[OSD([sQuery(id+"F0.wireOp",EDGE,"E0")])]}),makeQuery(id+"F12.opExtrude","SWEPT_FACE",FACE,{"disambiguationData":[OSD([sQuery(id+"F11.wireOp",EDGE,"d1064973-f400-4dc1-ab4f-e9b9d72f416c")])]})]});
            var Q340;
            Q340=makeQuery(id+"F12.boolean.opBoolean","INTERSECT",EDGE,{"derivedFrom":[makeQuery(id+"F1.opExtrude","SWEPT_FACE",FACE,{"disambiguationData":[OSD([sQuery(id+"F0.wireOp",EDGE,"E0")])]}),makeQuery(id+"F12.opExtrude","SWEPT_FACE",FACE,{"disambiguationData":[OSD([sQuery(id+"F11.wireOp",EDGE,"368e7495-1394-477b-bb01-d5cedc0a1b70")])]})]});
            var Q341;
            Q341=makeQuery(id+"F12.boolean.opBoolean","INTERSECT",EDGE,{"derivedFrom":[makeQuery(id+"F1.opExtrude","SWEPT_FACE",FACE,{"disambiguationData":[OSD([sQuery(id+"F0.wireOp",EDGE,"E0")])]}),makeQuery(id+"F12.opExtrude","SWEPT_FACE",FACE,{"disambiguationData":[OSD([sQuery(id+"F11.wireOp",EDGE,"50bbaaba-c4f5-4406-8380-98ff907eccc0")])]})]});
            var Q342;
            Q342=makeQuery(id+"F12.boolean.opBoolean","INTERSECT",EDGE,{"derivedFrom":[makeQuery(id+"F1.opExtrude","SWEPT_FACE",FACE,{"disambiguationData":[OSD([sQuery(id+"F0.wireOp",EDGE,"E0")])]}),makeQuery(id+"F12.opExtrude","SWEPT_FACE",FACE,{"disambiguationData":[OSD([sQuery(id+"F11.wireOp",EDGE,"252ab781-f89f-493a-a601-3851de4bca54")])]})]});
            var Q343;
            Q343=makeQuery(id+"F12.boolean.opBoolean","INTERSECT",EDGE,{"derivedFrom":[makeQuery(id+"F1.opExtrude","SWEPT_FACE",FACE,{"disambiguationData":[OSD([sQuery(id+"F0.wireOp",EDGE,"E0")])]}),makeQuery(id+"F12.opExtrude","SWEPT_FACE",FACE,{"disambiguationData":[OSD([sQuery(id+"F11.wireOp",EDGE,"077e507b-792a-4822-bd42-40c28a37b443")])]})]});
            var Q344;
            Q344=makeQuery(id+"F12.boolean.opBoolean","INTERSECT",EDGE,{"derivedFrom":[makeQuery(id+"F1.opExtrude","SWEPT_FACE",FACE,{"disambiguationData":[OSD([sQuery(id+"F0.wireOp",EDGE,"E0")])]}),makeQuery(id+"F12.opExtrude","SWEPT_FACE",FACE,{"disambiguationData":[OSD([sQuery(id+"F11.wireOp",EDGE,"041bb2eb-ae03-41b4-8679-2ee14c3b35eb")])]})]});
            var Q345;
            Q345=makeQuery(id+"F12.boolean.opBoolean","INTERSECT",EDGE,{"derivedFrom":[makeQuery(id+"F1.opExtrude","SWEPT_FACE",FACE,{"disambiguationData":[OSD([sQuery(id+"F0.wireOp",EDGE,"E0")])]}),makeQuery(id+"F12.opExtrude","SWEPT_FACE",FACE,{"disambiguationData":[OSD([sQuery(id+"F11.wireOp",EDGE,"e56254bb-4933-495c-a375-924da8ba2d97"),sQuery(id+"F11.wireOp",EDGE,"2da46073-95db-4ae7-83f6-e80e428f4fd1")])]})]});
            var Q346;
            Q346=makeQuery(id+"F12.boolean.opBoolean","INTERSECT",EDGE,{"derivedFrom":[makeQuery(id+"F1.opExtrude","SWEPT_FACE",FACE,{"disambiguationData":[OSD([sQuery(id+"F0.wireOp",EDGE,"E0")])]}),makeQuery(id+"F12.opExtrude","SWEPT_FACE",FACE,{"disambiguationData":[OSD([sQuery(id+"F11.wireOp",EDGE,"09fa856f-861a-4983-bd95-702295a2dd2e")])]})]});
            var Q347;
            Q347=makeQuery(id+"F10.boolean.opBoolean","INTERSECT",EDGE,{"disambiguationData":[OD(1.0)],"derivedFrom":[makeQuery(id+"F1.opExtrude","SWEPT_FACE",FACE,{"disambiguationData":[OSD([sQuery(id+"F0.wireOp",EDGE,"E0")])]}),makeQuery(id+"F10.opExtrude","SWEPT_FACE",FACE,{"disambiguationData":[OSD([sQuery(id+"F9.wireOp",EDGE,"E326")])]})]});
            var Q348;
            Q348=makeQuery(id+"F10.boolean.opBoolean","INTERSECT",EDGE,{"disambiguationData":[OD(1.0)],"derivedFrom":[makeQuery(id+"F1.opExtrude","SWEPT_FACE",FACE,{"disambiguationData":[OSD([sQuery(id+"F0.wireOp",EDGE,"E0")])]}),makeQuery(id+"F10.opExtrude","SWEPT_FACE",FACE,{"disambiguationData":[OSD([sQuery(id+"F9.wireOp",EDGE,"E321")])]})]});
            var Q349;
            Q349=makeQuery(id+"F10.boolean.opBoolean","INTERSECT",EDGE,{"disambiguationData":[OD(1.0)],"derivedFrom":[makeQuery(id+"F1.opExtrude","SWEPT_FACE",FACE,{"disambiguationData":[OSD([sQuery(id+"F0.wireOp",EDGE,"E0")])]}),makeQuery(id+"F10.opExtrude","SWEPT_FACE",FACE,{"disambiguationData":[OSD([sQuery(id+"F9.wireOp",EDGE,"E322")])]})]});
            fillet(context, id + "F14", {"entities" : qUnion([Q0, Q1, Q2, Q3, Q4, Q5, Q6, Q7, Q8, Q9, Q10, Q11, Q12, Q13, Q14, Q15, Q16, Q17, Q18, Q19, Q20, Q21, Q22, Q23, Q24, Q25, Q26, Q27, Q28, Q29, Q30, Q31, Q32, Q33, Q34, Q35, Q36, Q37, Q38, Q39, Q40, Q41, Q42, Q43, Q44, Q45, Q46, Q47, Q48, Q49, Q50, Q51, Q52, Q53, Q54, Q55, Q56, Q57, Q58, Q59, Q60, Q61, Q62, Q63, Q64, Q65, Q66, Q67, Q68, Q69, Q70, Q71, Q72, Q73, Q74, Q75, Q76, Q77, Q78, Q79, Q80, Q81, Q82, Q83, Q84, Q85, Q86, Q87, Q88, Q89, Q90, Q91, Q92, Q93, Q94, Q95, Q96, Q97, Q98, Q99, Q100, Q101, Q102, Q103, Q104, Q105, Q106, Q107, Q108, Q109, Q110, Q111, Q112, Q113, Q114, Q115, Q116, Q117, Q118, Q119, Q120, Q121, Q122, Q123, Q124, Q125, Q126, Q127, Q128, Q129, Q130, Q131, Q132, Q133, Q134, Q135, Q136, Q137, Q138, Q139, Q140, Q141, Q142, Q143, Q144, Q145, Q146, Q147, Q148, Q149, Q150, Q151, Q152, Q153, Q154, Q155, Q156, Q157, Q158, Q159, Q160, Q161, Q162, Q163, Q164, Q165, Q166, Q167, Q168, Q169, Q170, Q171, Q172, Q173, Q174, Q175, Q176, Q177, Q178, Q179, Q180, Q181, Q182, Q183, Q184, Q185, Q186, Q187, Q188, Q189, Q190, Q191, Q192, Q193, Q194, Q195, Q196, Q197, Q198, Q199, Q200, Q201, Q202, Q203, Q204, Q205, Q206, Q207, Q208, Q209, Q210, Q211, Q212, Q213, Q214, Q215, Q216, Q217, Q218, Q219, Q220, Q221, Q222, Q223, Q224, Q225, Q226, Q227, Q228, Q229, Q230, Q231, Q232, Q233, Q234, Q235, Q236, Q237, Q238, Q239, Q240, Q241, Q242, Q243, Q244, Q245, Q246, Q247, Q248, Q249, Q250, Q251, Q252, Q253, Q254, Q255, Q256, Q257, Q258, Q259, Q260, Q261, Q262, Q263, Q264, Q265, Q266, Q267, Q268, Q269, Q270, Q271, Q272, Q273, Q274, Q275, Q276, Q277, Q278, Q279, Q280, Q281, Q282, Q283, Q284, Q285, Q286, Q287, Q288, Q289, Q290, Q291, Q292, Q293, Q294, Q295, Q296, Q297, Q298, Q299, Q300, Q301, Q302, Q303, Q304, Q305, Q306, Q307, Q308, Q309, Q310, Q311, Q312, Q313, Q314, Q315, Q316, Q317, Q318, Q319, Q320, Q321, Q322, Q323, Q324, Q325, Q326, Q327, Q328, Q329, Q330, Q331, Q332, Q333, Q334, Q335, Q336, Q337, Q338, Q339, Q340, Q341, Q342, Q343, Q344, Q345, Q346, Q347, Q348, Q349]), "radius" : .4 * mm, "tangentPropagation" : true, "allowEdgeOverflow" : false});
        }
        {
            var Q0;
            Q0=makeQuery(id+"F10.boolean.opBoolean","INTERSECT",EDGE,{"disambiguationData":[OD(1.0)],"derivedFrom":[makeQuery(id+"F1.opExtrude","SWEPT_FACE",FACE,{"disambiguationData":[OSD([sQuery(id+"F0.wireOp",EDGE,"E0")])]}),makeQuery(id+"F10.opExtrude","SWEPT_FACE",FACE,{"disambiguationData":[OSD([sQuery(id+"F9.wireOp",EDGE,"E358")])]})]});
            var Q1;
            Q1=makeQuery(id+"F10.boolean.opBoolean","INTERSECT",EDGE,{"disambiguationData":[OD(1.0)],"derivedFrom":[makeQuery(id+"F1.opExtrude","SWEPT_FACE",FACE,{"disambiguationData":[OSD([sQuery(id+"F0.wireOp",EDGE,"E0")])]}),makeQuery(id+"F10.opExtrude","SWEPT_FACE",FACE,{"disambiguationData":[OSD([sQuery(id+"F9.wireOp",EDGE,"E360")])]})]});
            var Q2;
            Q2=makeQuery(id+"F10.boolean.opBoolean","INTERSECT",EDGE,{"disambiguationData":[OD(1.0)],"derivedFrom":[makeQuery(id+"F1.opExtrude","SWEPT_FACE",FACE,{"disambiguationData":[OSD([sQuery(id+"F0.wireOp",EDGE,"E0")])]}),makeQuery(id+"F10.opExtrude","SWEPT_FACE",FACE,{"disambiguationData":[OSD([sQuery(id+"F9.wireOp",EDGE,"E359")])]})]});
            var Q3;
            Q3=makeQuery(id+"F10.boolean.opBoolean","INTERSECT",EDGE,{"disambiguationData":[OD(1.0)],"derivedFrom":[makeQuery(id+"F1.opExtrude","SWEPT_FACE",FACE,{"disambiguationData":[OSD([sQuery(id+"F0.wireOp",EDGE,"E0")])]}),makeQuery(id+"F10.opExtrude","SWEPT_FACE",FACE,{"disambiguationData":[OSD([sQuery(id+"F9.wireOp",EDGE,"E343")])]})]});
            var Q4;
            Q4=makeQuery(id+"F10.boolean.opBoolean","INTERSECT",EDGE,{"disambiguationData":[OD(1.0)],"derivedFrom":[makeQuery(id+"F1.opExtrude","SWEPT_FACE",FACE,{"disambiguationData":[OSD([sQuery(id+"F0.wireOp",EDGE,"E0")])]}),makeQuery(id+"F10.opExtrude","SWEPT_FACE",FACE,{"disambiguationData":[OSD([sQuery(id+"F9.wireOp",EDGE,"E342")])]})]});
            var Q5;
            Q5=makeQuery(id+"F10.boolean.opBoolean","INTERSECT",EDGE,{"disambiguationData":[OD(1.0)],"derivedFrom":[makeQuery(id+"F1.opExtrude","SWEPT_FACE",FACE,{"disambiguationData":[OSD([sQuery(id+"F0.wireOp",EDGE,"E0")])]}),makeQuery(id+"F10.opExtrude","SWEPT_FACE",FACE,{"disambiguationData":[OSD([sQuery(id+"F9.wireOp",EDGE,"E341")])]})]});
            var Q6;
            Q6=makeQuery(id+"F10.boolean.opBoolean","INTERSECT",EDGE,{"disambiguationData":[OD(1.0)],"derivedFrom":[makeQuery(id+"F1.opExtrude","SWEPT_FACE",FACE,{"disambiguationData":[OSD([sQuery(id+"F0.wireOp",EDGE,"E0")])]}),makeQuery(id+"F10.opExtrude","SWEPT_FACE",FACE,{"disambiguationData":[OSD([sQuery(id+"F9.wireOp",EDGE,"E340")])]})]});
            var Q7;
            Q7=makeQuery(id+"F10.boolean.opBoolean","INTERSECT",EDGE,{"disambiguationData":[OD(1.0)],"derivedFrom":[makeQuery(id+"F1.opExtrude","SWEPT_FACE",FACE,{"disambiguationData":[OSD([sQuery(id+"F0.wireOp",EDGE,"E0")])]}),makeQuery(id+"F10.opExtrude","SWEPT_FACE",FACE,{"disambiguationData":[OSD([sQuery(id+"F9.wireOp",EDGE,"E339")])]})]});
            var Q8;
            Q8=makeQuery(id+"F10.boolean.opBoolean","INTERSECT",EDGE,{"disambiguationData":[OD(1.0)],"derivedFrom":[makeQuery(id+"F1.opExtrude","SWEPT_FACE",FACE,{"disambiguationData":[OSD([sQuery(id+"F0.wireOp",EDGE,"E0")])]}),makeQuery(id+"F10.opExtrude","SWEPT_FACE",FACE,{"disambiguationData":[OSD([sQuery(id+"F9.wireOp",EDGE,"E344")])]})]});
            var Q9;
            Q9=makeQuery(id+"F10.boolean.opBoolean","INTERSECT",EDGE,{"disambiguationData":[OD(1.0)],"derivedFrom":[makeQuery(id+"F1.opExtrude","SWEPT_FACE",FACE,{"disambiguationData":[OSD([sQuery(id+"F0.wireOp",EDGE,"E0")])]}),makeQuery(id+"F10.opExtrude","SWEPT_FACE",FACE,{"disambiguationData":[OSD([sQuery(id+"F9.wireOp",EDGE,"E357")])]})]});
            var Q10;
            Q10=makeQuery(id+"F10.boolean.opBoolean","INTERSECT",EDGE,{"disambiguationData":[OD(1.0)],"derivedFrom":[makeQuery(id+"F1.opExtrude","SWEPT_FACE",FACE,{"disambiguationData":[OSD([sQuery(id+"F0.wireOp",EDGE,"E0")])]}),makeQuery(id+"F10.opExtrude","SWEPT_FACE",FACE,{"disambiguationData":[OSD([sQuery(id+"F9.wireOp",EDGE,"E362")])]})]});
            var Q11;
            Q11=makeQuery(id+"F10.boolean.opBoolean","INTERSECT",EDGE,{"disambiguationData":[OD(1.0)],"derivedFrom":[makeQuery(id+"F1.opExtrude","SWEPT_FACE",FACE,{"disambiguationData":[OSD([sQuery(id+"F0.wireOp",EDGE,"E0")])]}),makeQuery(id+"F10.opExtrude","SWEPT_FACE",FACE,{"disambiguationData":[OSD([sQuery(id+"F9.wireOp",EDGE,"E361")])]})]});
            var Q12;
            Q12=makeQuery(id+"F10.boolean.opBoolean","INTERSECT",EDGE,{"disambiguationData":[OD(1.0)],"derivedFrom":[makeQuery(id+"F1.opExtrude","SWEPT_FACE",FACE,{"disambiguationData":[OSD([sQuery(id+"F0.wireOp",EDGE,"E0")])]}),makeQuery(id+"F10.opExtrude","SWEPT_FACE",FACE,{"disambiguationData":[OSD([sQuery(id+"F9.wireOp",EDGE,"E380")])]})]});
            var Q13;
            Q13=makeQuery(id+"F10.boolean.opBoolean","INTERSECT",EDGE,{"disambiguationData":[OD(1.0)],"derivedFrom":[makeQuery(id+"F1.opExtrude","SWEPT_FACE",FACE,{"disambiguationData":[OSD([sQuery(id+"F0.wireOp",EDGE,"E0")])]}),makeQuery(id+"F10.opExtrude","SWEPT_FACE",FACE,{"disambiguationData":[OSD([sQuery(id+"F9.wireOp",EDGE,"E379")])]})]});
            var Q14;
            Q14=makeQuery(id+"F10.boolean.opBoolean","INTERSECT",EDGE,{"disambiguationData":[OD(1.0)],"derivedFrom":[makeQuery(id+"F1.opExtrude","SWEPT_FACE",FACE,{"disambiguationData":[OSD([sQuery(id+"F0.wireOp",EDGE,"E0")])]}),makeQuery(id+"F10.opExtrude","SWEPT_FACE",FACE,{"disambiguationData":[OSD([sQuery(id+"F9.wireOp",EDGE,"E378")])]})]});
            var Q15;
            Q15=makeQuery(id+"F10.boolean.opBoolean","INTERSECT",EDGE,{"disambiguationData":[OD(1.0)],"derivedFrom":[makeQuery(id+"F1.opExtrude","SWEPT_FACE",FACE,{"disambiguationData":[OSD([sQuery(id+"F0.wireOp",EDGE,"E0")])]}),makeQuery(id+"F10.opExtrude","SWEPT_FACE",FACE,{"disambiguationData":[OSD([sQuery(id+"F9.wireOp",EDGE,"E377")])]})]});
            var Q16;
            Q16=makeQuery(id+"F10.boolean.opBoolean","INTERSECT",EDGE,{"disambiguationData":[OD(1.0)],"derivedFrom":[makeQuery(id+"F1.opExtrude","SWEPT_FACE",FACE,{"disambiguationData":[OSD([sQuery(id+"F0.wireOp",EDGE,"E0")])]}),makeQuery(id+"F10.opExtrude","SWEPT_FACE",FACE,{"disambiguationData":[OSD([sQuery(id+"F9.wireOp",EDGE,"E376")])]})]});
            var Q17;
            Q17=makeQuery(id+"F10.boolean.opBoolean","INTERSECT",EDGE,{"disambiguationData":[OD(1.0)],"derivedFrom":[makeQuery(id+"F1.opExtrude","SWEPT_FACE",FACE,{"disambiguationData":[OSD([sQuery(id+"F0.wireOp",EDGE,"E0")])]}),makeQuery(id+"F10.opExtrude","SWEPT_FACE",FACE,{"disambiguationData":[OSD([sQuery(id+"F9.wireOp",EDGE,"E375")])]})]});
            var Q18;
            Q18=makeQuery(id+"F10.boolean.opBoolean","INTERSECT",EDGE,{"disambiguationData":[OD(1.0)],"derivedFrom":[makeQuery(id+"F1.opExtrude","SWEPT_FACE",FACE,{"disambiguationData":[OSD([sQuery(id+"F0.wireOp",EDGE,"E0")])]}),makeQuery(id+"F10.opExtrude","SWEPT_FACE",FACE,{"disambiguationData":[OSD([sQuery(id+"F9.wireOp",EDGE,"E398")])]})]});
            var Q19;
            Q19=makeQuery(id+"F10.boolean.opBoolean","INTERSECT",EDGE,{"disambiguationData":[OD(1.0)],"derivedFrom":[makeQuery(id+"F1.opExtrude","SWEPT_FACE",FACE,{"disambiguationData":[OSD([sQuery(id+"F0.wireOp",EDGE,"E0")])]}),makeQuery(id+"F10.opExtrude","SWEPT_FACE",FACE,{"disambiguationData":[OSD([sQuery(id+"F9.wireOp",EDGE,"E397")])]})]});
            var Q20;
            Q20=makeQuery(id+"F10.boolean.opBoolean","INTERSECT",EDGE,{"disambiguationData":[OD(1.0)],"derivedFrom":[makeQuery(id+"F1.opExtrude","SWEPT_FACE",FACE,{"disambiguationData":[OSD([sQuery(id+"F0.wireOp",EDGE,"E0")])]}),makeQuery(id+"F10.opExtrude","SWEPT_FACE",FACE,{"disambiguationData":[OSD([sQuery(id+"F9.wireOp",EDGE,"E396")])]})]});
            var Q21;
            Q21=makeQuery(id+"F10.boolean.opBoolean","INTERSECT",EDGE,{"disambiguationData":[OD(1.0)],"derivedFrom":[makeQuery(id+"F1.opExtrude","SWEPT_FACE",FACE,{"disambiguationData":[OSD([sQuery(id+"F0.wireOp",EDGE,"E0")])]}),makeQuery(id+"F10.opExtrude","SWEPT_FACE",FACE,{"disambiguationData":[OSD([sQuery(id+"F9.wireOp",EDGE,"E395")])]})]});
            var Q22;
            Q22=makeQuery(id+"F10.boolean.opBoolean","INTERSECT",EDGE,{"disambiguationData":[OD(1.0)],"derivedFrom":[makeQuery(id+"F1.opExtrude","SWEPT_FACE",FACE,{"disambiguationData":[OSD([sQuery(id+"F0.wireOp",EDGE,"E0")])]}),makeQuery(id+"F10.opExtrude","SWEPT_FACE",FACE,{"disambiguationData":[OSD([sQuery(id+"F9.wireOp",EDGE,"E394")])]})]});
            var Q23;
            Q23=makeQuery(id+"F10.boolean.opBoolean","INTERSECT",EDGE,{"disambiguationData":[OD(1.0)],"derivedFrom":[makeQuery(id+"F1.opExtrude","SWEPT_FACE",FACE,{"disambiguationData":[OSD([sQuery(id+"F0.wireOp",EDGE,"E0")])]}),makeQuery(id+"F10.opExtrude","SWEPT_FACE",FACE,{"disambiguationData":[OSD([sQuery(id+"F9.wireOp",EDGE,"E393")])]})]});
            var Q24;
            Q24=makeQuery(id+"F10.boolean.opBoolean","INTERSECT",EDGE,{"disambiguationData":[OD(1.0)],"derivedFrom":[makeQuery(id+"F1.opExtrude","SWEPT_FACE",FACE,{"disambiguationData":[OSD([sQuery(id+"F0.wireOp",EDGE,"E0")])]}),makeQuery(id+"F10.opExtrude","SWEPT_FACE",FACE,{"disambiguationData":[OSD([sQuery(id+"F9.wireOp",EDGE,"E413")])]})]});
            var Q25;
            Q25=makeQuery(id+"F10.boolean.opBoolean","INTERSECT",EDGE,{"disambiguationData":[OD(1.0)],"derivedFrom":[makeQuery(id+"F1.opExtrude","SWEPT_FACE",FACE,{"disambiguationData":[OSD([sQuery(id+"F0.wireOp",EDGE,"E0")])]}),makeQuery(id+"F10.opExtrude","SWEPT_FACE",FACE,{"disambiguationData":[OSD([sQuery(id+"F9.wireOp",EDGE,"E412")])]})]});
            var Q26;
            Q26=makeQuery(id+"F10.boolean.opBoolean","INTERSECT",EDGE,{"disambiguationData":[OD(1.0)],"derivedFrom":[makeQuery(id+"F1.opExtrude","SWEPT_FACE",FACE,{"disambiguationData":[OSD([sQuery(id+"F0.wireOp",EDGE,"E0")])]}),makeQuery(id+"F10.opExtrude","SWEPT_FACE",FACE,{"disambiguationData":[OSD([sQuery(id+"F9.wireOp",EDGE,"E411")])]})]});
            var Q27;
            Q27=makeQuery(id+"F10.boolean.opBoolean","INTERSECT",EDGE,{"disambiguationData":[OD(1.0)],"derivedFrom":[makeQuery(id+"F1.opExtrude","SWEPT_FACE",FACE,{"disambiguationData":[OSD([sQuery(id+"F0.wireOp",EDGE,"E0")])]}),makeQuery(id+"F10.opExtrude","SWEPT_FACE",FACE,{"disambiguationData":[OSD([sQuery(id+"F9.wireOp",EDGE,"E416")])]})]});
            var Q28;
            Q28=makeQuery(id+"F10.boolean.opBoolean","INTERSECT",EDGE,{"disambiguationData":[OD(1.0)],"derivedFrom":[makeQuery(id+"F1.opExtrude","SWEPT_FACE",FACE,{"disambiguationData":[OSD([sQuery(id+"F0.wireOp",EDGE,"E0")])]}),makeQuery(id+"F10.opExtrude","SWEPT_FACE",FACE,{"disambiguationData":[OSD([sQuery(id+"F9.wireOp",EDGE,"E415")])]})]});
            var Q29;
            Q29=makeQuery(id+"F10.boolean.opBoolean","INTERSECT",EDGE,{"disambiguationData":[OD(1.0)],"derivedFrom":[makeQuery(id+"F1.opExtrude","SWEPT_FACE",FACE,{"disambiguationData":[OSD([sQuery(id+"F0.wireOp",EDGE,"E0")])]}),makeQuery(id+"F10.opExtrude","SWEPT_FACE",FACE,{"disambiguationData":[OSD([sQuery(id+"F9.wireOp",EDGE,"E414")])]})]});
            var Q30;
            Q30=makeQuery(id+"F10.boolean.opBoolean","INTERSECT",EDGE,{"disambiguationData":[OD(1.0)],"derivedFrom":[makeQuery(id+"F1.opExtrude","SWEPT_FACE",FACE,{"disambiguationData":[OSD([sQuery(id+"F0.wireOp",EDGE,"E0")])]}),makeQuery(id+"F10.opExtrude","SWEPT_FACE",FACE,{"disambiguationData":[OSD([sQuery(id+"F9.wireOp",EDGE,"8715a638-6380-49e4-8166-a35da90eea4d")])]})]});
            var Q31;
            Q31=makeQuery(id+"F10.boolean.opBoolean","INTERSECT",EDGE,{"disambiguationData":[OD(1.0)],"derivedFrom":[makeQuery(id+"F1.opExtrude","SWEPT_FACE",FACE,{"disambiguationData":[OSD([sQuery(id+"F0.wireOp",EDGE,"E0")])]}),makeQuery(id+"F10.opExtrude","SWEPT_FACE",FACE,{"disambiguationData":[OSD([sQuery(id+"F9.wireOp",EDGE,"b2bf0872-2c35-4f65-a834-23150e7e820b")])]})]});
            var Q32;
            Q32=makeQuery(id+"F10.boolean.opBoolean","INTERSECT",EDGE,{"disambiguationData":[OD(1.0)],"derivedFrom":[makeQuery(id+"F1.opExtrude","SWEPT_FACE",FACE,{"disambiguationData":[OSD([sQuery(id+"F0.wireOp",EDGE,"E0")])]}),makeQuery(id+"F10.opExtrude","SWEPT_FACE",FACE,{"disambiguationData":[OSD([sQuery(id+"F9.wireOp",EDGE,"68b86c13-7ece-4168-b183-e17e549264ea")])]})]});
            var Q33;
            Q33=makeQuery(id+"F10.boolean.opBoolean","INTERSECT",EDGE,{"disambiguationData":[OD(1.0)],"derivedFrom":[makeQuery(id+"F1.opExtrude","SWEPT_FACE",FACE,{"disambiguationData":[OSD([sQuery(id+"F0.wireOp",EDGE,"E0")])]}),makeQuery(id+"F10.opExtrude","SWEPT_FACE",FACE,{"disambiguationData":[OSD([sQuery(id+"F9.wireOp",EDGE,"ad162529-5cfe-4944-83b4-e317f5486a3e")])]})]});
            var Q34;
            Q34=makeQuery(id+"F10.boolean.opBoolean","INTERSECT",EDGE,{"disambiguationData":[OD(1.0)],"derivedFrom":[makeQuery(id+"F1.opExtrude","SWEPT_FACE",FACE,{"disambiguationData":[OSD([sQuery(id+"F0.wireOp",EDGE,"E0")])]}),makeQuery(id+"F10.opExtrude","SWEPT_FACE",FACE,{"disambiguationData":[OSD([sQuery(id+"F9.wireOp",EDGE,"9310307e-7862-42e2-8ad8-274fad6d12ca")])]})]});
            var Q35;
            Q35=makeQuery(id+"F10.boolean.opBoolean","INTERSECT",EDGE,{"disambiguationData":[OD(1.0)],"derivedFrom":[makeQuery(id+"F1.opExtrude","SWEPT_FACE",FACE,{"disambiguationData":[OSD([sQuery(id+"F0.wireOp",EDGE,"E0")])]}),makeQuery(id+"F10.opExtrude","SWEPT_FACE",FACE,{"disambiguationData":[OSD([sQuery(id+"F9.wireOp",EDGE,"1193cbdb-8a08-404e-b46e-3bccfaa25342")])]})]});
            var Q36;
            Q36=makeQuery(id+"F10.boolean.opBoolean","INTERSECT",EDGE,{"disambiguationData":[OD(1.0)],"derivedFrom":[makeQuery(id+"F1.opExtrude","SWEPT_FACE",FACE,{"disambiguationData":[OSD([sQuery(id+"F0.wireOp",EDGE,"E0")])]}),makeQuery(id+"F10.opExtrude","SWEPT_FACE",FACE,{"disambiguationData":[OSD([sQuery(id+"F9.wireOp",EDGE,"bc574ee6-e8d7-4402-b7bf-a31d76de5201")])]})]});
            var Q37;
            Q37=makeQuery(id+"F10.boolean.opBoolean","INTERSECT",EDGE,{"disambiguationData":[OD(1.0)],"derivedFrom":[makeQuery(id+"F1.opExtrude","SWEPT_FACE",FACE,{"disambiguationData":[OSD([sQuery(id+"F0.wireOp",EDGE,"E0")])]}),makeQuery(id+"F10.opExtrude","SWEPT_FACE",FACE,{"disambiguationData":[OSD([sQuery(id+"F9.wireOp",EDGE,"7bb27c30-01e1-4c30-9b62-d81abe0e1569")])]})]});
            var Q38;
            Q38=makeQuery(id+"F10.boolean.opBoolean","INTERSECT",EDGE,{"disambiguationData":[OD(1.0)],"derivedFrom":[makeQuery(id+"F1.opExtrude","SWEPT_FACE",FACE,{"disambiguationData":[OSD([sQuery(id+"F0.wireOp",EDGE,"E0")])]}),makeQuery(id+"F10.opExtrude","SWEPT_FACE",FACE,{"disambiguationData":[OSD([sQuery(id+"F9.wireOp",EDGE,"7b437f7c-4576-4f11-8c60-76c3eb11ba37")])]})]});
            var Q39;
            Q39=makeQuery(id+"F10.boolean.opBoolean","INTERSECT",EDGE,{"disambiguationData":[OD(1.0)],"derivedFrom":[makeQuery(id+"F1.opExtrude","SWEPT_FACE",FACE,{"disambiguationData":[OSD([sQuery(id+"F0.wireOp",EDGE,"E0")])]}),makeQuery(id+"F10.opExtrude","SWEPT_FACE",FACE,{"disambiguationData":[OSD([sQuery(id+"F9.wireOp",EDGE,"2db869a3-9406-4888-bcbb-00bb43a69eba")])]})]});
            var Q40;
            Q40=makeQuery(id+"F10.boolean.opBoolean","INTERSECT",EDGE,{"disambiguationData":[OD(1.0)],"derivedFrom":[makeQuery(id+"F1.opExtrude","SWEPT_FACE",FACE,{"disambiguationData":[OSD([sQuery(id+"F0.wireOp",EDGE,"E0")])]}),makeQuery(id+"F10.opExtrude","SWEPT_FACE",FACE,{"disambiguationData":[OSD([sQuery(id+"F9.wireOp",EDGE,"6dc2a6c8-a69d-41e3-9ee2-05e60369f11b")])]})]});
            var Q41;
            Q41=makeQuery(id+"F10.boolean.opBoolean","INTERSECT",EDGE,{"disambiguationData":[OD(1.0)],"derivedFrom":[makeQuery(id+"F1.opExtrude","SWEPT_FACE",FACE,{"disambiguationData":[OSD([sQuery(id+"F0.wireOp",EDGE,"E0")])]}),makeQuery(id+"F10.opExtrude","SWEPT_FACE",FACE,{"disambiguationData":[OSD([sQuery(id+"F9.wireOp",EDGE,"34f3141e-2481-4cad-a724-18fe9355e9ac")])]})]});
            var Q42;
            Q42=makeQuery(id+"F10.boolean.opBoolean","INTERSECT",EDGE,{"disambiguationData":[OD(1.0)],"derivedFrom":[makeQuery(id+"F1.opExtrude","SWEPT_FACE",FACE,{"disambiguationData":[OSD([sQuery(id+"F0.wireOp",EDGE,"E0")])]}),makeQuery(id+"F10.opExtrude","SWEPT_FACE",FACE,{"disambiguationData":[OSD([sQuery(id+"F9.wireOp",EDGE,"0749a5eb-1656-439a-a869-05d76e53423e")])]})]});
            var Q43;
            Q43=makeQuery(id+"F10.boolean.opBoolean","INTERSECT",EDGE,{"disambiguationData":[OD(1.0)],"derivedFrom":[makeQuery(id+"F1.opExtrude","SWEPT_FACE",FACE,{"disambiguationData":[OSD([sQuery(id+"F0.wireOp",EDGE,"E0")])]}),makeQuery(id+"F10.opExtrude","SWEPT_FACE",FACE,{"disambiguationData":[OSD([sQuery(id+"F9.wireOp",EDGE,"b6c25ba9-2617-4775-a0b3-41ef528efab6")])]})]});
            var Q44;
            Q44=makeQuery(id+"F10.boolean.opBoolean","INTERSECT",EDGE,{"disambiguationData":[OD(1.0)],"derivedFrom":[makeQuery(id+"F1.opExtrude","SWEPT_FACE",FACE,{"disambiguationData":[OSD([sQuery(id+"F0.wireOp",EDGE,"E0")])]}),makeQuery(id+"F10.opExtrude","SWEPT_FACE",FACE,{"disambiguationData":[OSD([sQuery(id+"F9.wireOp",EDGE,"d7004727-f34f-4852-a492-ed529d9aa36c")])]})]});
            var Q45;
            Q45=makeQuery(id+"F10.boolean.opBoolean","INTERSECT",EDGE,{"disambiguationData":[OD(1.0)],"derivedFrom":[makeQuery(id+"F1.opExtrude","SWEPT_FACE",FACE,{"disambiguationData":[OSD([sQuery(id+"F0.wireOp",EDGE,"E0")])]}),makeQuery(id+"F10.opExtrude","SWEPT_FACE",FACE,{"disambiguationData":[OSD([sQuery(id+"F9.wireOp",EDGE,"589360f9-4b1b-47cd-a11b-2a67260c207c")])]})]});
            var Q46;
            Q46=makeQuery(id+"F10.boolean.opBoolean","INTERSECT",EDGE,{"disambiguationData":[OD(1.0)],"derivedFrom":[makeQuery(id+"F1.opExtrude","SWEPT_FACE",FACE,{"disambiguationData":[OSD([sQuery(id+"F0.wireOp",EDGE,"E0")])]}),makeQuery(id+"F10.opExtrude","SWEPT_FACE",FACE,{"disambiguationData":[OSD([sQuery(id+"F9.wireOp",EDGE,"c678ade0-3d66-4aad-85d1-643d7c5f28b6")])]})]});
            var Q47;
            Q47=makeQuery(id+"F10.boolean.opBoolean","INTERSECT",EDGE,{"disambiguationData":[OD(1.0)],"derivedFrom":[makeQuery(id+"F1.opExtrude","SWEPT_FACE",FACE,{"disambiguationData":[OSD([sQuery(id+"F0.wireOp",EDGE,"E0")])]}),makeQuery(id+"F10.opExtrude","SWEPT_FACE",FACE,{"disambiguationData":[OSD([sQuery(id+"F9.wireOp",EDGE,"8357bcdf-6207-4d5b-93da-fad6725d465d")])]})]});
            var Q48;
            Q48=makeQuery(id+"F10.boolean.opBoolean","INTERSECT",EDGE,{"disambiguationData":[OD(1.0)],"derivedFrom":[makeQuery(id+"F1.opExtrude","SWEPT_FACE",FACE,{"disambiguationData":[OSD([sQuery(id+"F0.wireOp",EDGE,"E0")])]}),makeQuery(id+"F10.opExtrude","SWEPT_FACE",FACE,{"disambiguationData":[OSD([sQuery(id+"F9.wireOp",EDGE,"917abea8-5958-4d13-b49a-d9c63b39efb4")])]})]});
            var Q49;
            Q49=makeQuery(id+"F10.boolean.opBoolean","INTERSECT",EDGE,{"disambiguationData":[OD(1.0)],"derivedFrom":[makeQuery(id+"F1.opExtrude","SWEPT_FACE",FACE,{"disambiguationData":[OSD([sQuery(id+"F0.wireOp",EDGE,"E0")])]}),makeQuery(id+"F10.opExtrude","SWEPT_FACE",FACE,{"disambiguationData":[OSD([sQuery(id+"F9.wireOp",EDGE,"5ad42132-cac8-4035-b0a1-ce6f07b595eb")])]})]});
            var Q50;
            Q50=makeQuery(id+"F10.boolean.opBoolean","INTERSECT",EDGE,{"disambiguationData":[OD(1.0)],"derivedFrom":[makeQuery(id+"F1.opExtrude","SWEPT_FACE",FACE,{"disambiguationData":[OSD([sQuery(id+"F0.wireOp",EDGE,"E0")])]}),makeQuery(id+"F10.opExtrude","SWEPT_FACE",FACE,{"disambiguationData":[OSD([sQuery(id+"F9.wireOp",EDGE,"423f58d8-1f19-46c3-b5b6-1235c5f2b6ac")])]})]});
            var Q51;
            Q51=makeQuery(id+"F10.boolean.opBoolean","INTERSECT",EDGE,{"disambiguationData":[OD(1.0)],"derivedFrom":[makeQuery(id+"F1.opExtrude","SWEPT_FACE",FACE,{"disambiguationData":[OSD([sQuery(id+"F0.wireOp",EDGE,"E0")])]}),makeQuery(id+"F10.opExtrude","SWEPT_FACE",FACE,{"disambiguationData":[OSD([sQuery(id+"F9.wireOp",EDGE,"a8de5c63-b59d-4111-aaf0-c59ceeb84539")])]})]});
            var Q52;
            Q52=makeQuery(id+"F10.boolean.opBoolean","INTERSECT",EDGE,{"disambiguationData":[OD(1.0)],"derivedFrom":[makeQuery(id+"F1.opExtrude","SWEPT_FACE",FACE,{"disambiguationData":[OSD([sQuery(id+"F0.wireOp",EDGE,"E0")])]}),makeQuery(id+"F10.opExtrude","SWEPT_FACE",FACE,{"disambiguationData":[OSD([sQuery(id+"F9.wireOp",EDGE,"43266347-99e5-4a65-87d8-d68d1b57105e")])]})]});
            var Q53;
            Q53=makeQuery(id+"F10.boolean.opBoolean","INTERSECT",EDGE,{"disambiguationData":[OD(1.0)],"derivedFrom":[makeQuery(id+"F1.opExtrude","SWEPT_FACE",FACE,{"disambiguationData":[OSD([sQuery(id+"F0.wireOp",EDGE,"E0")])]}),makeQuery(id+"F10.opExtrude","SWEPT_FACE",FACE,{"disambiguationData":[OSD([sQuery(id+"F9.wireOp",EDGE,"2193aa8a-cfb0-48d0-87fc-1cfe83a7fd52")])]})]});
            var Q54;
            Q54=makeQuery(id+"F10.boolean.opBoolean","INTERSECT",EDGE,{"disambiguationData":[OD(1.0)],"derivedFrom":[makeQuery(id+"F1.opExtrude","SWEPT_FACE",FACE,{"disambiguationData":[OSD([sQuery(id+"F0.wireOp",EDGE,"E0")])]}),makeQuery(id+"F10.opExtrude","SWEPT_FACE",FACE,{"disambiguationData":[OSD([sQuery(id+"F9.wireOp",EDGE,"17f8cebd-a2bc-4d80-8a13-7e07ce9ceaf0")])]})]});
            var Q55;
            Q55=makeQuery(id+"F10.boolean.opBoolean","INTERSECT",EDGE,{"disambiguationData":[OD(1.0)],"derivedFrom":[makeQuery(id+"F1.opExtrude","SWEPT_FACE",FACE,{"disambiguationData":[OSD([sQuery(id+"F0.wireOp",EDGE,"E0")])]}),makeQuery(id+"F10.opExtrude","SWEPT_FACE",FACE,{"disambiguationData":[OSD([sQuery(id+"F9.wireOp",EDGE,"4653122c-81e7-43b8-a175-0e9b4399c1dd")])]})]});
            var Q56;
            Q56=makeQuery(id+"F10.boolean.opBoolean","INTERSECT",EDGE,{"disambiguationData":[OD(1.0)],"derivedFrom":[makeQuery(id+"F1.opExtrude","SWEPT_FACE",FACE,{"disambiguationData":[OSD([sQuery(id+"F0.wireOp",EDGE,"E0")])]}),makeQuery(id+"F10.opExtrude","SWEPT_FACE",FACE,{"disambiguationData":[OSD([sQuery(id+"F9.wireOp",EDGE,"f7332d99-994a-4820-91d6-0eb80c66d826")])]})]});
            var Q57;
            Q57=makeQuery(id+"F10.boolean.opBoolean","INTERSECT",EDGE,{"disambiguationData":[OD(1.0)],"derivedFrom":[makeQuery(id+"F1.opExtrude","SWEPT_FACE",FACE,{"disambiguationData":[OSD([sQuery(id+"F0.wireOp",EDGE,"E0")])]}),makeQuery(id+"F10.opExtrude","SWEPT_FACE",FACE,{"disambiguationData":[OSD([sQuery(id+"F9.wireOp",EDGE,"4fa15834-391d-4db3-8b3b-82f9d2034739")])]})]});
            var Q58;
            Q58=makeQuery(id+"F10.boolean.opBoolean","INTERSECT",EDGE,{"disambiguationData":[OD(1.0)],"derivedFrom":[makeQuery(id+"F1.opExtrude","SWEPT_FACE",FACE,{"disambiguationData":[OSD([sQuery(id+"F0.wireOp",EDGE,"E0")])]}),makeQuery(id+"F10.opExtrude","SWEPT_FACE",FACE,{"disambiguationData":[OSD([sQuery(id+"F9.wireOp",EDGE,"cf1de00f-3169-4f70-98fb-b7290205bd4b")])]})]});
            var Q59;
            Q59=makeQuery(id+"F10.boolean.opBoolean","INTERSECT",EDGE,{"disambiguationData":[OD(1.0)],"derivedFrom":[makeQuery(id+"F1.opExtrude","SWEPT_FACE",FACE,{"disambiguationData":[OSD([sQuery(id+"F0.wireOp",EDGE,"E0")])]}),makeQuery(id+"F10.opExtrude","SWEPT_FACE",FACE,{"disambiguationData":[OSD([sQuery(id+"F9.wireOp",EDGE,"e82f161c-c8f9-431a-b111-592f8292c69f")])]})]});
            var Q60;
            Q60=makeQuery(id+"F10.boolean.opBoolean","INTERSECT",EDGE,{"disambiguationData":[OD(1.0)],"derivedFrom":[makeQuery(id+"F1.opExtrude","SWEPT_FACE",FACE,{"disambiguationData":[OSD([sQuery(id+"F0.wireOp",EDGE,"E0")])]}),makeQuery(id+"F10.opExtrude","SWEPT_FACE",FACE,{"disambiguationData":[OSD([sQuery(id+"F9.wireOp",EDGE,"7meaahbg-dbg3-uSPd-PEJJ-e7DtyzYx0gQt"),sQuery(id+"F9.wireOp",EDGE,"vEAYXyeL-ay2Z-WL7a-7Ha5-VfRoazVvpcCo")])]})]});
            var Q61;
            Q61=makeQuery(id+"F10.boolean.opBoolean","INTERSECT",EDGE,{"disambiguationData":[OD(1.0)],"derivedFrom":[makeQuery(id+"F1.opExtrude","SWEPT_FACE",FACE,{"disambiguationData":[OSD([sQuery(id+"F0.wireOp",EDGE,"E0")])]}),makeQuery(id+"F10.opExtrude","SWEPT_FACE",FACE,{"disambiguationData":[OSD([sQuery(id+"F9.wireOp",EDGE,"1QEsIIjE-87yi-7XXF-o0p4-XyzEA0SBXInf")])]})]});
            var Q62;
            Q62=makeQuery(id+"F10.boolean.opBoolean","INTERSECT",EDGE,{"disambiguationData":[OD(1.0)],"derivedFrom":[makeQuery(id+"F1.opExtrude","SWEPT_FACE",FACE,{"disambiguationData":[OSD([sQuery(id+"F0.wireOp",EDGE,"E0")])]}),makeQuery(id+"F10.opExtrude","SWEPT_FACE",FACE,{"disambiguationData":[OSD([sQuery(id+"F9.wireOp",EDGE,"e0e213fe-66f1-429b-aeb4-bda37cd8a542")])]})]});
            var Q63;
            Q63=makeQuery(id+"F10.boolean.opBoolean","INTERSECT",EDGE,{"disambiguationData":[OD(1.0)],"derivedFrom":[makeQuery(id+"F1.opExtrude","SWEPT_FACE",FACE,{"disambiguationData":[OSD([sQuery(id+"F0.wireOp",EDGE,"E0")])]}),makeQuery(id+"F10.opExtrude","SWEPT_FACE",FACE,{"disambiguationData":[OSD([sQuery(id+"F9.wireOp",EDGE,"OpU4Ypz6-Hcb8-YkKV-7chd-lZCeiZS7tYYF")])]})]});
            var Q64;
            Q64=makeQuery(id+"F10.boolean.opBoolean","INTERSECT",EDGE,{"disambiguationData":[OD(1.0)],"derivedFrom":[makeQuery(id+"F1.opExtrude","SWEPT_FACE",FACE,{"disambiguationData":[OSD([sQuery(id+"F0.wireOp",EDGE,"E0")])]}),makeQuery(id+"F10.opExtrude","SWEPT_FACE",FACE,{"disambiguationData":[OSD([sQuery(id+"F9.wireOp",EDGE,"c61f0de6-50a4-4502-a890-74c6c6ac1cd3")])]})]});
            var Q65;
            Q65=makeQuery(id+"F10.boolean.opBoolean","INTERSECT",EDGE,{"disambiguationData":[OD(1.0)],"derivedFrom":[makeQuery(id+"F1.opExtrude","SWEPT_FACE",FACE,{"disambiguationData":[OSD([sQuery(id+"F0.wireOp",EDGE,"E0")])]}),makeQuery(id+"F10.opExtrude","SWEPT_FACE",FACE,{"disambiguationData":[OSD([sQuery(id+"F9.wireOp",EDGE,"88dc3317-14d6-4f39-a813-642e505b3db3")])]})]});
            var Q66;
            Q66=makeQuery(id+"F10.boolean.opBoolean","INTERSECT",EDGE,{"disambiguationData":[OD(1.0)],"derivedFrom":[makeQuery(id+"F1.opExtrude","SWEPT_FACE",FACE,{"disambiguationData":[OSD([sQuery(id+"F0.wireOp",EDGE,"E0")])]}),makeQuery(id+"F10.opExtrude","SWEPT_FACE",FACE,{"disambiguationData":[OSD([sQuery(id+"F9.wireOp",EDGE,"429d95a1-3c8a-48cf-b1fd-65ae80db6ffc")])]})]});
            var Q67;
            Q67=makeQuery(id+"F10.boolean.opBoolean","INTERSECT",EDGE,{"disambiguationData":[OD(1.0)],"derivedFrom":[makeQuery(id+"F1.opExtrude","SWEPT_FACE",FACE,{"disambiguationData":[OSD([sQuery(id+"F0.wireOp",EDGE,"E0")])]}),makeQuery(id+"F10.opExtrude","SWEPT_FACE",FACE,{"disambiguationData":[OSD([sQuery(id+"F9.wireOp",EDGE,"0975aea8-55f6-417d-8d6b-6ad5a96ef988")])]})]});
            var Q68;
            Q68=makeQuery(id+"F10.boolean.opBoolean","INTERSECT",EDGE,{"disambiguationData":[OD(1.0)],"derivedFrom":[makeQuery(id+"F1.opExtrude","SWEPT_FACE",FACE,{"disambiguationData":[OSD([sQuery(id+"F0.wireOp",EDGE,"E0")])]}),makeQuery(id+"F10.opExtrude","SWEPT_FACE",FACE,{"disambiguationData":[OSD([sQuery(id+"F9.wireOp",EDGE,"fce1ec24-8c70-45cc-92f2-20edd6db3c88")])]})]});
            var Q69;
            Q69=makeQuery(id+"F5.boolean.opBoolean","INTERSECT",EDGE,{"disambiguationData":[OD(1.0)],"derivedFrom":[makeQuery(id+"F1.opExtrude","SWEPT_FACE",FACE,{"disambiguationData":[OSD([sQuery(id+"F0.wireOp",EDGE,"E0")])]}),makeQuery(id+"F5.opExtrude","SWEPT_FACE",FACE,{"disambiguationData":[OSD([sQuery(id+"F4.wireOp",EDGE,"03b36015-34d2-4950-84e9-b550512b4ec9")])]})]});
            var Q70;
            Q70=makeQuery(id+"F5.boolean.opBoolean","INTERSECT",EDGE,{"disambiguationData":[OD(1.0)],"derivedFrom":[makeQuery(id+"F1.opExtrude","SWEPT_FACE",FACE,{"disambiguationData":[OSD([sQuery(id+"F0.wireOp",EDGE,"E0")])]}),makeQuery(id+"F5.opExtrude","SWEPT_FACE",FACE,{"disambiguationData":[OSD([sQuery(id+"F4.wireOp",EDGE,"19f739e4-1ef2-45c8-9f20-bd755fe40443")])]})]});
            var Q71;
            Q71=makeQuery(id+"F5.boolean.opBoolean","INTERSECT",EDGE,{"disambiguationData":[OD(1.0)],"derivedFrom":[makeQuery(id+"F1.opExtrude","SWEPT_FACE",FACE,{"disambiguationData":[OSD([sQuery(id+"F0.wireOp",EDGE,"E0")])]}),makeQuery(id+"F5.opExtrude","SWEPT_FACE",FACE,{"disambiguationData":[OSD([sQuery(id+"F4.wireOp",EDGE,"bd2a5c31-cc9d-444b-baf1-6f7b9b2beccf")])]})]});
            var Q72;
            Q72=makeQuery(id+"F5.boolean.opBoolean","INTERSECT",EDGE,{"disambiguationData":[OD(1.0)],"derivedFrom":[makeQuery(id+"F1.opExtrude","SWEPT_FACE",FACE,{"disambiguationData":[OSD([sQuery(id+"F0.wireOp",EDGE,"E0")])]}),makeQuery(id+"F5.opExtrude","SWEPT_FACE",FACE,{"disambiguationData":[OSD([sQuery(id+"F4.wireOp",EDGE,"d264c38f-4b04-4a21-be61-ebc556e8b4dc")])]})]});
            var Q73;
            Q73=makeQuery(id+"F5.boolean.opBoolean","INTERSECT",EDGE,{"disambiguationData":[OD(1.0)],"derivedFrom":[makeQuery(id+"F1.opExtrude","SWEPT_FACE",FACE,{"disambiguationData":[OSD([sQuery(id+"F0.wireOp",EDGE,"E0")])]}),makeQuery(id+"F5.opExtrude","SWEPT_FACE",FACE,{"disambiguationData":[OSD([sQuery(id+"F4.wireOp",EDGE,"f02fcaa4-8809-4191-8bb9-9daee93d77e2")])]})]});
            var Q74;
            Q74=makeQuery(id+"F5.boolean.opBoolean","INTERSECT",EDGE,{"disambiguationData":[OD(1.0)],"derivedFrom":[makeQuery(id+"F1.opExtrude","SWEPT_FACE",FACE,{"disambiguationData":[OSD([sQuery(id+"F0.wireOp",EDGE,"E0")])]}),makeQuery(id+"F5.opExtrude","SWEPT_FACE",FACE,{"disambiguationData":[OSD([sQuery(id+"F4.wireOp",EDGE,"10851094-9e06-4481-a16a-60cc523c1961")])]})]});
            var Q75;
            Q75=makeQuery(id+"F5.boolean.opBoolean","INTERSECT",EDGE,{"disambiguationData":[OD(1.0)],"derivedFrom":[makeQuery(id+"F1.opExtrude","SWEPT_FACE",FACE,{"disambiguationData":[OSD([sQuery(id+"F0.wireOp",EDGE,"E0")])]}),makeQuery(id+"F5.opExtrude","SWEPT_FACE",FACE,{"disambiguationData":[OSD([sQuery(id+"F4.wireOp",EDGE,"67b481ec-10fe-46d3-8faa-ebe6010fe4f1")])]})]});
            var Q76;
            Q76=makeQuery(id+"F5.boolean.opBoolean","INTERSECT",EDGE,{"disambiguationData":[OD(1.0)],"derivedFrom":[makeQuery(id+"F1.opExtrude","SWEPT_FACE",FACE,{"disambiguationData":[OSD([sQuery(id+"F0.wireOp",EDGE,"E0")])]}),makeQuery(id+"F5.opExtrude","SWEPT_FACE",FACE,{"disambiguationData":[OSD([sQuery(id+"F4.wireOp",EDGE,"92af876a-0958-4a7c-97b2-f4e8acbef095")])]})]});
            var Q77;
            Q77=makeQuery(id+"F5.boolean.opBoolean","INTERSECT",EDGE,{"disambiguationData":[OD(1.0)],"derivedFrom":[makeQuery(id+"F1.opExtrude","SWEPT_FACE",FACE,{"disambiguationData":[OSD([sQuery(id+"F0.wireOp",EDGE,"E0")])]}),makeQuery(id+"F5.opExtrude","SWEPT_FACE",FACE,{"disambiguationData":[OSD([sQuery(id+"F4.wireOp",EDGE,"09477fc4-9d29-4f20-8901-aec53dcd1546")])]})]});
            var Q78;
            Q78=makeQuery(id+"F5.boolean.opBoolean","INTERSECT",EDGE,{"disambiguationData":[OD(1.0)],"derivedFrom":[makeQuery(id+"F1.opExtrude","SWEPT_FACE",FACE,{"disambiguationData":[OSD([sQuery(id+"F0.wireOp",EDGE,"E0")])]}),makeQuery(id+"F5.opExtrude","SWEPT_FACE",FACE,{"disambiguationData":[OSD([sQuery(id+"F4.wireOp",EDGE,"bcb0f5b9-98e4-4035-bb5b-1a8c92403a19")])]})]});
            var Q79;
            Q79=makeQuery(id+"F5.boolean.opBoolean","INTERSECT",EDGE,{"disambiguationData":[OD(1.0)],"derivedFrom":[makeQuery(id+"F1.opExtrude","SWEPT_FACE",FACE,{"disambiguationData":[OSD([sQuery(id+"F0.wireOp",EDGE,"E0")])]}),makeQuery(id+"F5.opExtrude","SWEPT_FACE",FACE,{"disambiguationData":[OSD([sQuery(id+"F4.wireOp",EDGE,"aca02d5f-46a9-486e-88e3-eb9aae4273e8")])]})]});
            var Q80;
            Q80=makeQuery(id+"F5.boolean.opBoolean","INTERSECT",EDGE,{"disambiguationData":[OD(1.0)],"derivedFrom":[makeQuery(id+"F1.opExtrude","SWEPT_FACE",FACE,{"disambiguationData":[OSD([sQuery(id+"F0.wireOp",EDGE,"E0")])]}),makeQuery(id+"F5.opExtrude","SWEPT_FACE",FACE,{"disambiguationData":[OSD([sQuery(id+"F4.wireOp",EDGE,"30311b2f-ed17-4601-a199-a8278ef993fb")])]})]});
            var Q81;
            Q81=makeQuery(id+"F5.boolean.opBoolean","INTERSECT",EDGE,{"disambiguationData":[OD(1.0)],"derivedFrom":[makeQuery(id+"F1.opExtrude","SWEPT_FACE",FACE,{"disambiguationData":[OSD([sQuery(id+"F0.wireOp",EDGE,"E0")])]}),makeQuery(id+"F5.opExtrude","SWEPT_FACE",FACE,{"disambiguationData":[OSD([sQuery(id+"F4.wireOp",EDGE,"ed008b68-955d-4315-9cc0-8abb2c6860b0")])]})]});
            var Q82;
            Q82=makeQuery(id+"F5.boolean.opBoolean","INTERSECT",EDGE,{"disambiguationData":[OD(1.0)],"derivedFrom":[makeQuery(id+"F1.opExtrude","SWEPT_FACE",FACE,{"disambiguationData":[OSD([sQuery(id+"F0.wireOp",EDGE,"E0")])]}),makeQuery(id+"F5.opExtrude","SWEPT_FACE",FACE,{"disambiguationData":[OSD([sQuery(id+"F4.wireOp",EDGE,"efc5e5b1-0746-45f0-90e3-bd883f3492f4")])]})]});
            var Q83;
            Q83=makeQuery(id+"F5.boolean.opBoolean","INTERSECT",EDGE,{"disambiguationData":[OD(1.0)],"derivedFrom":[makeQuery(id+"F1.opExtrude","SWEPT_FACE",FACE,{"disambiguationData":[OSD([sQuery(id+"F0.wireOp",EDGE,"E0")])]}),makeQuery(id+"F5.opExtrude","SWEPT_FACE",FACE,{"disambiguationData":[OSD([sQuery(id+"F4.wireOp",EDGE,"562b9cc4-530f-4157-bc84-2c37910fa221")])]})]});
            var Q84;
            Q84=makeQuery(id+"F5.boolean.opBoolean","INTERSECT",EDGE,{"disambiguationData":[OD(1.0)],"derivedFrom":[makeQuery(id+"F1.opExtrude","SWEPT_FACE",FACE,{"disambiguationData":[OSD([sQuery(id+"F0.wireOp",EDGE,"E0")])]}),makeQuery(id+"F5.opExtrude","SWEPT_FACE",FACE,{"disambiguationData":[OSD([sQuery(id+"F4.wireOp",EDGE,"ab9f0dd0-8a88-45b5-9e6c-47f07906d12f")])]})]});
            var Q85;
            Q85=makeQuery(id+"F5.boolean.opBoolean","INTERSECT",EDGE,{"disambiguationData":[OD(1.0)],"derivedFrom":[makeQuery(id+"F1.opExtrude","SWEPT_FACE",FACE,{"disambiguationData":[OSD([sQuery(id+"F0.wireOp",EDGE,"E0")])]}),makeQuery(id+"F5.opExtrude","SWEPT_FACE",FACE,{"disambiguationData":[OSD([sQuery(id+"F4.wireOp",EDGE,"76385219-3691-4f38-9da5-edf1140a4629")])]})]});
            var Q86;
            Q86=makeQuery(id+"F5.boolean.opBoolean","INTERSECT",EDGE,{"disambiguationData":[OD(1.0)],"derivedFrom":[makeQuery(id+"F1.opExtrude","SWEPT_FACE",FACE,{"disambiguationData":[OSD([sQuery(id+"F0.wireOp",EDGE,"E0")])]}),makeQuery(id+"F5.opExtrude","SWEPT_FACE",FACE,{"disambiguationData":[OSD([sQuery(id+"F4.wireOp",EDGE,"1da9000e-137c-457e-9dd6-58b65176467c")])]})]});
            var Q87;
            Q87=makeQuery(id+"F5.boolean.opBoolean","INTERSECT",EDGE,{"disambiguationData":[OD(1.0)],"derivedFrom":[makeQuery(id+"F1.opExtrude","SWEPT_FACE",FACE,{"disambiguationData":[OSD([sQuery(id+"F0.wireOp",EDGE,"E0")])]}),makeQuery(id+"F5.opExtrude","SWEPT_FACE",FACE,{"disambiguationData":[OSD([sQuery(id+"F4.wireOp",EDGE,"15ec9440-3994-4756-befc-73e6937f9073")])]})]});
            var Q88;
            Q88=makeQuery(id+"F5.boolean.opBoolean","INTERSECT",EDGE,{"disambiguationData":[OD(1.0)],"derivedFrom":[makeQuery(id+"F1.opExtrude","SWEPT_FACE",FACE,{"disambiguationData":[OSD([sQuery(id+"F0.wireOp",EDGE,"E0")])]}),makeQuery(id+"F5.opExtrude","SWEPT_FACE",FACE,{"disambiguationData":[OSD([sQuery(id+"F4.wireOp",EDGE,"70ca714e-c3bb-4dc2-844f-e69955e1961d")])]})]});
            var Q89;
            Q89=makeQuery(id+"F5.boolean.opBoolean","INTERSECT",EDGE,{"disambiguationData":[OD(1.0)],"derivedFrom":[makeQuery(id+"F1.opExtrude","SWEPT_FACE",FACE,{"disambiguationData":[OSD([sQuery(id+"F0.wireOp",EDGE,"E0")])]}),makeQuery(id+"F5.opExtrude","SWEPT_FACE",FACE,{"disambiguationData":[OSD([sQuery(id+"F4.wireOp",EDGE,"b9a5c8a8-e1c1-4ccb-a6a4-30bc00998619")])]})]});
            var Q90;
            Q90=makeQuery(id+"F5.boolean.opBoolean","INTERSECT",EDGE,{"disambiguationData":[OD(1.0)],"derivedFrom":[makeQuery(id+"F1.opExtrude","SWEPT_FACE",FACE,{"disambiguationData":[OSD([sQuery(id+"F0.wireOp",EDGE,"E0")])]}),makeQuery(id+"F5.opExtrude","SWEPT_FACE",FACE,{"disambiguationData":[OSD([sQuery(id+"F4.wireOp",EDGE,"66c2d1b9-9082-457f-8158-46fefb0d0b5d")])]})]});
            var Q91;
            Q91=makeQuery(id+"F5.boolean.opBoolean","INTERSECT",EDGE,{"disambiguationData":[OD(1.0)],"derivedFrom":[makeQuery(id+"F1.opExtrude","SWEPT_FACE",FACE,{"disambiguationData":[OSD([sQuery(id+"F0.wireOp",EDGE,"E0")])]}),makeQuery(id+"F5.opExtrude","SWEPT_FACE",FACE,{"disambiguationData":[OSD([sQuery(id+"F4.wireOp",EDGE,"5e54ec67-0438-4ccb-ab1e-fb0c5627ff7a")])]})]});
            var Q92;
            Q92=makeQuery(id+"F5.boolean.opBoolean","INTERSECT",EDGE,{"disambiguationData":[OD(1.0)],"derivedFrom":[makeQuery(id+"F1.opExtrude","SWEPT_FACE",FACE,{"disambiguationData":[OSD([sQuery(id+"F0.wireOp",EDGE,"E0")])]}),makeQuery(id+"F5.opExtrude","SWEPT_FACE",FACE,{"disambiguationData":[OSD([sQuery(id+"F4.wireOp",EDGE,"fd9b85d0-086e-4753-9286-7d80f3d11dd9")])]})]});
            var Q93;
            Q93=makeQuery(id+"F5.boolean.opBoolean","INTERSECT",EDGE,{"disambiguationData":[OD(1.0)],"derivedFrom":[makeQuery(id+"F1.opExtrude","SWEPT_FACE",FACE,{"disambiguationData":[OSD([sQuery(id+"F0.wireOp",EDGE,"E0")])]}),makeQuery(id+"F5.opExtrude","SWEPT_FACE",FACE,{"disambiguationData":[OSD([sQuery(id+"F4.wireOp",EDGE,"9e1b2bd2-a8a3-4caa-b598-0f2db5d1325d")])]})]});
            var Q94;
            Q94=makeQuery(id+"F5.boolean.opBoolean","INTERSECT",EDGE,{"disambiguationData":[OD(1.0)],"derivedFrom":[makeQuery(id+"F1.opExtrude","SWEPT_FACE",FACE,{"disambiguationData":[OSD([sQuery(id+"F0.wireOp",EDGE,"E0")])]}),makeQuery(id+"F5.opExtrude","SWEPT_FACE",FACE,{"disambiguationData":[OSD([sQuery(id+"F4.wireOp",EDGE,"b8538754-f3f1-4cf7-bfe9-078eb6985bef")])]})]});
            var Q95;
            Q95=makeQuery(id+"F5.boolean.opBoolean","INTERSECT",EDGE,{"disambiguationData":[OD(1.0)],"derivedFrom":[makeQuery(id+"F1.opExtrude","SWEPT_FACE",FACE,{"disambiguationData":[OSD([sQuery(id+"F0.wireOp",EDGE,"E0")])]}),makeQuery(id+"F5.opExtrude","SWEPT_FACE",FACE,{"disambiguationData":[OSD([sQuery(id+"F4.wireOp",EDGE,"c5cda94b-8dbb-4131-8629-d94229ce36f8")])]})]});
            var Q96;
            Q96=makeQuery(id+"F5.boolean.opBoolean","INTERSECT",EDGE,{"disambiguationData":[OD(1.0)],"derivedFrom":[makeQuery(id+"F1.opExtrude","SWEPT_FACE",FACE,{"disambiguationData":[OSD([sQuery(id+"F0.wireOp",EDGE,"E0")])]}),makeQuery(id+"F5.opExtrude","SWEPT_FACE",FACE,{"disambiguationData":[OSD([sQuery(id+"F4.wireOp",EDGE,"536ab4de-4fb2-4d7d-9807-1d714ccadb66")])]})]});
            var Q97;
            Q97=makeQuery(id+"F5.boolean.opBoolean","INTERSECT",EDGE,{"disambiguationData":[OD(1.0)],"derivedFrom":[makeQuery(id+"F1.opExtrude","SWEPT_FACE",FACE,{"disambiguationData":[OSD([sQuery(id+"F0.wireOp",EDGE,"E0")])]}),makeQuery(id+"F5.opExtrude","SWEPT_FACE",FACE,{"disambiguationData":[OSD([sQuery(id+"F4.wireOp",EDGE,"82180203-eaff-47f3-b606-d8d7c32d142f")])]})]});
            var Q98;
            Q98=makeQuery(id+"F5.boolean.opBoolean","INTERSECT",EDGE,{"disambiguationData":[OD(1.0)],"derivedFrom":[makeQuery(id+"F1.opExtrude","SWEPT_FACE",FACE,{"disambiguationData":[OSD([sQuery(id+"F0.wireOp",EDGE,"E0")])]}),makeQuery(id+"F5.opExtrude","SWEPT_FACE",FACE,{"disambiguationData":[OSD([sQuery(id+"F4.wireOp",EDGE,"14d064f9-5360-4d18-9d9e-82328bf9daba")])]})]});
            var Q99;
            Q99=makeQuery(id+"F5.boolean.opBoolean","INTERSECT",EDGE,{"disambiguationData":[OD(1.0)],"derivedFrom":[makeQuery(id+"F1.opExtrude","SWEPT_FACE",FACE,{"disambiguationData":[OSD([sQuery(id+"F0.wireOp",EDGE,"E0")])]}),makeQuery(id+"F5.opExtrude","SWEPT_FACE",FACE,{"disambiguationData":[OSD([sQuery(id+"F4.wireOp",EDGE,"c0d87fc6-e010-4d73-961e-dfed47c8a1b3")])]})]});
            var Q100;
            Q100=makeQuery(id+"F5.boolean.opBoolean","INTERSECT",EDGE,{"disambiguationData":[OD(1.0)],"derivedFrom":[makeQuery(id+"F1.opExtrude","SWEPT_FACE",FACE,{"disambiguationData":[OSD([sQuery(id+"F0.wireOp",EDGE,"E0")])]}),makeQuery(id+"F5.opExtrude","SWEPT_FACE",FACE,{"disambiguationData":[OSD([sQuery(id+"F4.wireOp",EDGE,"f55199c0-7004-4acb-b4c7-226994b61401")])]})]});
            var Q101;
            Q101=makeQuery(id+"F5.boolean.opBoolean","INTERSECT",EDGE,{"disambiguationData":[OD(1.0)],"derivedFrom":[makeQuery(id+"F1.opExtrude","SWEPT_FACE",FACE,{"disambiguationData":[OSD([sQuery(id+"F0.wireOp",EDGE,"E0")])]}),makeQuery(id+"F5.opExtrude","SWEPT_FACE",FACE,{"disambiguationData":[OSD([sQuery(id+"F4.wireOp",EDGE,"d0a2849f-a89e-4989-ab6e-8e188e140a90")])]})]});
            var Q102;
            Q102=makeQuery(id+"F5.boolean.opBoolean","INTERSECT",EDGE,{"disambiguationData":[OD(1.0)],"derivedFrom":[makeQuery(id+"F1.opExtrude","SWEPT_FACE",FACE,{"disambiguationData":[OSD([sQuery(id+"F0.wireOp",EDGE,"E0")])]}),makeQuery(id+"F5.opExtrude","SWEPT_FACE",FACE,{"disambiguationData":[OSD([sQuery(id+"F4.wireOp",EDGE,"978e1622-7887-4f07-a91b-81f9d5efcfbf")])]})]});
            var Q103;
            Q103=makeQuery(id+"F5.boolean.opBoolean","INTERSECT",EDGE,{"disambiguationData":[OD(1.0)],"derivedFrom":[makeQuery(id+"F1.opExtrude","SWEPT_FACE",FACE,{"disambiguationData":[OSD([sQuery(id+"F0.wireOp",EDGE,"E0")])]}),makeQuery(id+"F5.opExtrude","SWEPT_FACE",FACE,{"disambiguationData":[OSD([sQuery(id+"F4.wireOp",EDGE,"b60fa973-c727-4668-bfa0-a1e16f7a99aa")])]})]});
            var Q104;
            Q104=makeQuery(id+"F5.boolean.opBoolean","INTERSECT",EDGE,{"disambiguationData":[OD(1.0)],"derivedFrom":[makeQuery(id+"F1.opExtrude","SWEPT_FACE",FACE,{"disambiguationData":[OSD([sQuery(id+"F0.wireOp",EDGE,"E0")])]}),makeQuery(id+"F5.opExtrude","SWEPT_FACE",FACE,{"disambiguationData":[OSD([sQuery(id+"F4.wireOp",EDGE,"8a1b3b7c-f627-453a-8324-eadb2e6b2aa6")])]})]});
            var Q105;
            Q105=makeQuery(id+"F5.boolean.opBoolean","INTERSECT",EDGE,{"disambiguationData":[OD(1.0)],"derivedFrom":[makeQuery(id+"F1.opExtrude","SWEPT_FACE",FACE,{"disambiguationData":[OSD([sQuery(id+"F0.wireOp",EDGE,"E0")])]}),makeQuery(id+"F5.opExtrude","SWEPT_FACE",FACE,{"disambiguationData":[OSD([sQuery(id+"F4.wireOp",EDGE,"c79ec3c5-8163-43ca-85dc-8d9b1c829184")])]})]});
            var Q106;
            Q106=makeQuery(id+"F5.boolean.opBoolean","INTERSECT",EDGE,{"disambiguationData":[OD(1.0)],"derivedFrom":[makeQuery(id+"F1.opExtrude","SWEPT_FACE",FACE,{"disambiguationData":[OSD([sQuery(id+"F0.wireOp",EDGE,"E0")])]}),makeQuery(id+"F5.opExtrude","SWEPT_FACE",FACE,{"disambiguationData":[OSD([sQuery(id+"F4.wireOp",EDGE,"E135")])]})]});
            var Q107;
            Q107=makeQuery(id+"F5.boolean.opBoolean","INTERSECT",EDGE,{"disambiguationData":[OD(1.0)],"derivedFrom":[makeQuery(id+"F1.opExtrude","SWEPT_FACE",FACE,{"disambiguationData":[OSD([sQuery(id+"F0.wireOp",EDGE,"E0")])]}),makeQuery(id+"F5.opExtrude","SWEPT_FACE",FACE,{"disambiguationData":[OSD([sQuery(id+"F4.wireOp",EDGE,"E136")])]})]});
            var Q108;
            Q108=makeQuery(id+"F5.boolean.opBoolean","INTERSECT",EDGE,{"disambiguationData":[OD(1.0)],"derivedFrom":[makeQuery(id+"F1.opExtrude","SWEPT_FACE",FACE,{"disambiguationData":[OSD([sQuery(id+"F0.wireOp",EDGE,"E0")])]}),makeQuery(id+"F5.opExtrude","SWEPT_FACE",FACE,{"disambiguationData":[OSD([sQuery(id+"F4.wireOp",EDGE,"E137")])]})]});
            var Q109;
            Q109=makeQuery(id+"F5.boolean.opBoolean","INTERSECT",EDGE,{"disambiguationData":[OD(1.0)],"derivedFrom":[makeQuery(id+"F1.opExtrude","SWEPT_FACE",FACE,{"disambiguationData":[OSD([sQuery(id+"F0.wireOp",EDGE,"E0")])]}),makeQuery(id+"F5.opExtrude","SWEPT_FACE",FACE,{"disambiguationData":[OSD([sQuery(id+"F4.wireOp",EDGE,"d52b0a11-5b01-40f3-ab4f-3d3d9242be96")])]})]});
            var Q110;
            Q110=makeQuery(id+"F5.boolean.opBoolean","INTERSECT",EDGE,{"disambiguationData":[OD(1.0)],"derivedFrom":[makeQuery(id+"F1.opExtrude","SWEPT_FACE",FACE,{"disambiguationData":[OSD([sQuery(id+"F0.wireOp",EDGE,"E0")])]}),makeQuery(id+"F5.opExtrude","SWEPT_FACE",FACE,{"disambiguationData":[OSD([sQuery(id+"F4.wireOp",EDGE,"E127")])]})]});
            var Q111;
            Q111=makeQuery(id+"F5.boolean.opBoolean","INTERSECT",EDGE,{"disambiguationData":[OD(1.0)],"derivedFrom":[makeQuery(id+"F1.opExtrude","SWEPT_FACE",FACE,{"disambiguationData":[OSD([sQuery(id+"F0.wireOp",EDGE,"E0")])]}),makeQuery(id+"F5.opExtrude","SWEPT_FACE",FACE,{"disambiguationData":[OSD([sQuery(id+"F4.wireOp",EDGE,"E126")])]})]});
            var Q112;
            Q112=makeQuery(id+"F5.boolean.opBoolean","INTERSECT",EDGE,{"disambiguationData":[OD(1.0)],"derivedFrom":[makeQuery(id+"F1.opExtrude","SWEPT_FACE",FACE,{"disambiguationData":[OSD([sQuery(id+"F0.wireOp",EDGE,"E0")])]}),makeQuery(id+"F5.opExtrude","SWEPT_FACE",FACE,{"disambiguationData":[OSD([sQuery(id+"F4.wireOp",EDGE,"E125")])]})]});
            var Q113;
            Q113=makeQuery(id+"F5.boolean.opBoolean","INTERSECT",EDGE,{"disambiguationData":[OD(1.0)],"derivedFrom":[makeQuery(id+"F1.opExtrude","SWEPT_FACE",FACE,{"disambiguationData":[OSD([sQuery(id+"F0.wireOp",EDGE,"E0")])]}),makeQuery(id+"F5.opExtrude","SWEPT_FACE",FACE,{"disambiguationData":[OSD([sQuery(id+"F4.wireOp",EDGE,"E124")])]})]});
            var Q114;
            Q114=makeQuery(id+"F5.boolean.opBoolean","INTERSECT",EDGE,{"disambiguationData":[OD(1.0)],"derivedFrom":[makeQuery(id+"F1.opExtrude","SWEPT_FACE",FACE,{"disambiguationData":[OSD([sQuery(id+"F0.wireOp",EDGE,"E0")])]}),makeQuery(id+"F5.opExtrude","SWEPT_FACE",FACE,{"disambiguationData":[OSD([sQuery(id+"F4.wireOp",EDGE,"E123")])]})]});
            var Q115;
            Q115=makeQuery(id+"F5.boolean.opBoolean","INTERSECT",EDGE,{"disambiguationData":[OD(1.0)],"derivedFrom":[makeQuery(id+"F1.opExtrude","SWEPT_FACE",FACE,{"disambiguationData":[OSD([sQuery(id+"F0.wireOp",EDGE,"E0")])]}),makeQuery(id+"F5.opExtrude","SWEPT_FACE",FACE,{"disambiguationData":[OSD([sQuery(id+"F4.wireOp",EDGE,"E122")])]})]});
            var Q116;
            Q116=makeQuery(id+"F5.boolean.opBoolean","INTERSECT",EDGE,{"disambiguationData":[OD(1.0)],"derivedFrom":[makeQuery(id+"F1.opExtrude","SWEPT_FACE",FACE,{"disambiguationData":[OSD([sQuery(id+"F0.wireOp",EDGE,"E0")])]}),makeQuery(id+"F5.opExtrude","SWEPT_FACE",FACE,{"disambiguationData":[OSD([sQuery(id+"F4.wireOp",EDGE,"E109")])]})]});
            var Q117;
            Q117=makeQuery(id+"F5.boolean.opBoolean","INTERSECT",EDGE,{"disambiguationData":[OD(1.0)],"derivedFrom":[makeQuery(id+"F1.opExtrude","SWEPT_FACE",FACE,{"disambiguationData":[OSD([sQuery(id+"F0.wireOp",EDGE,"E0")])]}),makeQuery(id+"F5.opExtrude","SWEPT_FACE",FACE,{"disambiguationData":[OSD([sQuery(id+"F4.wireOp",EDGE,"E104")])]})]});
            var Q118;
            Q118=makeQuery(id+"F5.boolean.opBoolean","INTERSECT",EDGE,{"disambiguationData":[OD(1.0)],"derivedFrom":[makeQuery(id+"F1.opExtrude","SWEPT_FACE",FACE,{"disambiguationData":[OSD([sQuery(id+"F0.wireOp",EDGE,"E0")])]}),makeQuery(id+"F5.opExtrude","SWEPT_FACE",FACE,{"disambiguationData":[OSD([sQuery(id+"F4.wireOp",EDGE,"E105")])]})]});
            var Q119;
            Q119=makeQuery(id+"F5.boolean.opBoolean","INTERSECT",EDGE,{"disambiguationData":[OD(1.0)],"derivedFrom":[makeQuery(id+"F1.opExtrude","SWEPT_FACE",FACE,{"disambiguationData":[OSD([sQuery(id+"F0.wireOp",EDGE,"E0")])]}),makeQuery(id+"F5.opExtrude","SWEPT_FACE",FACE,{"disambiguationData":[OSD([sQuery(id+"F4.wireOp",EDGE,"E106")])]})]});
            var Q120;
            Q120=makeQuery(id+"F5.boolean.opBoolean","INTERSECT",EDGE,{"disambiguationData":[OD(1.0)],"derivedFrom":[makeQuery(id+"F1.opExtrude","SWEPT_FACE",FACE,{"disambiguationData":[OSD([sQuery(id+"F0.wireOp",EDGE,"E0")])]}),makeQuery(id+"F5.opExtrude","SWEPT_FACE",FACE,{"disambiguationData":[OSD([sQuery(id+"F4.wireOp",EDGE,"E107")])]})]});
            var Q121;
            Q121=makeQuery(id+"F5.boolean.opBoolean","INTERSECT",EDGE,{"disambiguationData":[OD(1.0)],"derivedFrom":[makeQuery(id+"F1.opExtrude","SWEPT_FACE",FACE,{"disambiguationData":[OSD([sQuery(id+"F0.wireOp",EDGE,"E0")])]}),makeQuery(id+"F5.opExtrude","SWEPT_FACE",FACE,{"disambiguationData":[OSD([sQuery(id+"F4.wireOp",EDGE,"E108")])]})]});
            var Q122;
            Q122=makeQuery(id+"F5.boolean.opBoolean","INTERSECT",EDGE,{"disambiguationData":[OD(1.0)],"derivedFrom":[makeQuery(id+"F1.opExtrude","SWEPT_FACE",FACE,{"disambiguationData":[OSD([sQuery(id+"F0.wireOp",EDGE,"E0")])]}),makeQuery(id+"F5.opExtrude","SWEPT_FACE",FACE,{"disambiguationData":[OSD([sQuery(id+"F4.wireOp",EDGE,"E91")])]})]});
            var Q123;
            Q123=makeQuery(id+"F5.boolean.opBoolean","INTERSECT",EDGE,{"disambiguationData":[OD(1.0)],"derivedFrom":[makeQuery(id+"F1.opExtrude","SWEPT_FACE",FACE,{"disambiguationData":[OSD([sQuery(id+"F0.wireOp",EDGE,"E0")])]}),makeQuery(id+"F5.opExtrude","SWEPT_FACE",FACE,{"disambiguationData":[OSD([sQuery(id+"F4.wireOp",EDGE,"E90")])]})]});
            var Q124;
            Q124=makeQuery(id+"F5.boolean.opBoolean","INTERSECT",EDGE,{"disambiguationData":[OD(1.0)],"derivedFrom":[makeQuery(id+"F1.opExtrude","SWEPT_FACE",FACE,{"disambiguationData":[OSD([sQuery(id+"F0.wireOp",EDGE,"E0")])]}),makeQuery(id+"F5.opExtrude","SWEPT_FACE",FACE,{"disambiguationData":[OSD([sQuery(id+"F4.wireOp",EDGE,"E89")])]})]});
            var Q125;
            Q125=makeQuery(id+"F5.boolean.opBoolean","INTERSECT",EDGE,{"disambiguationData":[OD(1.0)],"derivedFrom":[makeQuery(id+"F1.opExtrude","SWEPT_FACE",FACE,{"disambiguationData":[OSD([sQuery(id+"F0.wireOp",EDGE,"E0")])]}),makeQuery(id+"F5.opExtrude","SWEPT_FACE",FACE,{"disambiguationData":[OSD([sQuery(id+"F4.wireOp",EDGE,"E88")])]})]});
            var Q126;
            Q126=makeQuery(id+"F5.boolean.opBoolean","INTERSECT",EDGE,{"disambiguationData":[OD(1.0)],"derivedFrom":[makeQuery(id+"F1.opExtrude","SWEPT_FACE",FACE,{"disambiguationData":[OSD([sQuery(id+"F0.wireOp",EDGE,"E0")])]}),makeQuery(id+"F5.opExtrude","SWEPT_FACE",FACE,{"disambiguationData":[OSD([sQuery(id+"F4.wireOp",EDGE,"E87")])]})]});
            var Q127;
            Q127=makeQuery(id+"F5.boolean.opBoolean","INTERSECT",EDGE,{"disambiguationData":[OD(1.0)],"derivedFrom":[makeQuery(id+"F1.opExtrude","SWEPT_FACE",FACE,{"disambiguationData":[OSD([sQuery(id+"F0.wireOp",EDGE,"E0")])]}),makeQuery(id+"F5.opExtrude","SWEPT_FACE",FACE,{"disambiguationData":[OSD([sQuery(id+"F4.wireOp",EDGE,"E86")])]})]});
            var Q128;
            Q128=makeQuery(id+"F5.boolean.opBoolean","INTERSECT",EDGE,{"disambiguationData":[OD(1.0)],"derivedFrom":[makeQuery(id+"F1.opExtrude","SWEPT_FACE",FACE,{"disambiguationData":[OSD([sQuery(id+"F0.wireOp",EDGE,"E0")])]}),makeQuery(id+"F5.opExtrude","SWEPT_FACE",FACE,{"disambiguationData":[OSD([sQuery(id+"F4.wireOp",EDGE,"E73")])]})]});
            var Q129;
            Q129=makeQuery(id+"F5.boolean.opBoolean","INTERSECT",EDGE,{"disambiguationData":[OD(1.0)],"derivedFrom":[makeQuery(id+"F1.opExtrude","SWEPT_FACE",FACE,{"disambiguationData":[OSD([sQuery(id+"F0.wireOp",EDGE,"E0")])]}),makeQuery(id+"F5.opExtrude","SWEPT_FACE",FACE,{"disambiguationData":[OSD([sQuery(id+"F4.wireOp",EDGE,"E68")])]})]});
            var Q130;
            Q130=makeQuery(id+"F5.boolean.opBoolean","INTERSECT",EDGE,{"disambiguationData":[OD(1.0)],"derivedFrom":[makeQuery(id+"F1.opExtrude","SWEPT_FACE",FACE,{"disambiguationData":[OSD([sQuery(id+"F0.wireOp",EDGE,"E0")])]}),makeQuery(id+"F5.opExtrude","SWEPT_FACE",FACE,{"disambiguationData":[OSD([sQuery(id+"F4.wireOp",EDGE,"E72")])]})]});
            var Q131;
            Q131=makeQuery(id+"F5.boolean.opBoolean","INTERSECT",EDGE,{"disambiguationData":[OD(1.0)],"derivedFrom":[makeQuery(id+"F1.opExtrude","SWEPT_FACE",FACE,{"disambiguationData":[OSD([sQuery(id+"F0.wireOp",EDGE,"E0")])]}),makeQuery(id+"F5.opExtrude","SWEPT_FACE",FACE,{"disambiguationData":[OSD([sQuery(id+"F4.wireOp",EDGE,"E68")])]})]});
            var Q132;
            Q132=makeQuery(id+"F5.boolean.opBoolean","INTERSECT",EDGE,{"disambiguationData":[OD(1.0)],"derivedFrom":[makeQuery(id+"F1.opExtrude","SWEPT_FACE",FACE,{"disambiguationData":[OSD([sQuery(id+"F0.wireOp",EDGE,"E0")])]}),makeQuery(id+"F5.opExtrude","SWEPT_FACE",FACE,{"disambiguationData":[OSD([sQuery(id+"F4.wireOp",EDGE,"E69")])]})]});
            var Q133;
            Q133=makeQuery(id+"F5.boolean.opBoolean","INTERSECT",EDGE,{"disambiguationData":[OD(1.0)],"derivedFrom":[makeQuery(id+"F1.opExtrude","SWEPT_FACE",FACE,{"disambiguationData":[OSD([sQuery(id+"F0.wireOp",EDGE,"E0")])]}),makeQuery(id+"F5.opExtrude","SWEPT_FACE",FACE,{"disambiguationData":[OSD([sQuery(id+"F4.wireOp",EDGE,"E70")])]})]});
            var Q134;
            Q134=makeQuery(id+"F5.boolean.opBoolean","INTERSECT",EDGE,{"disambiguationData":[OD(1.0)],"derivedFrom":[makeQuery(id+"F1.opExtrude","SWEPT_FACE",FACE,{"disambiguationData":[OSD([sQuery(id+"F0.wireOp",EDGE,"E0")])]}),makeQuery(id+"F5.opExtrude","SWEPT_FACE",FACE,{"disambiguationData":[OSD([sQuery(id+"F4.wireOp",EDGE,"E71")])]})]});
            var Q135;
            Q135=makeQuery(id+"F5.boolean.opBoolean","INTERSECT",EDGE,{"disambiguationData":[OD(1.0)],"derivedFrom":[makeQuery(id+"F1.opExtrude","SWEPT_FACE",FACE,{"disambiguationData":[OSD([sQuery(id+"F0.wireOp",EDGE,"E0")])]}),makeQuery(id+"F5.opExtrude","SWEPT_FACE",FACE,{"disambiguationData":[OSD([sQuery(id+"F4.wireOp",EDGE,"E55")])]})]});
            var Q136;
            Q136=makeQuery(id+"F5.boolean.opBoolean","INTERSECT",EDGE,{"disambiguationData":[OD(1.0)],"derivedFrom":[makeQuery(id+"F1.opExtrude","SWEPT_FACE",FACE,{"disambiguationData":[OSD([sQuery(id+"F0.wireOp",EDGE,"E0")])]}),makeQuery(id+"F5.opExtrude","SWEPT_FACE",FACE,{"disambiguationData":[OSD([sQuery(id+"F4.wireOp",EDGE,"E54")])]})]});
            var Q137;
            Q137=makeQuery(id+"F5.boolean.opBoolean","INTERSECT",EDGE,{"disambiguationData":[OD(1.0)],"derivedFrom":[makeQuery(id+"F1.opExtrude","SWEPT_FACE",FACE,{"disambiguationData":[OSD([sQuery(id+"F0.wireOp",EDGE,"E0")])]}),makeQuery(id+"F5.opExtrude","SWEPT_FACE",FACE,{"disambiguationData":[OSD([sQuery(id+"F4.wireOp",EDGE,"E53")])]})]});
            var Q138;
            Q138=makeQuery(id+"F5.boolean.opBoolean","INTERSECT",EDGE,{"disambiguationData":[OD(1.0)],"derivedFrom":[makeQuery(id+"F1.opExtrude","SWEPT_FACE",FACE,{"disambiguationData":[OSD([sQuery(id+"F0.wireOp",EDGE,"E0")])]}),makeQuery(id+"F5.opExtrude","SWEPT_FACE",FACE,{"disambiguationData":[OSD([sQuery(id+"F4.wireOp",EDGE,"E52")])]})]});
            var Q139;
            Q139=makeQuery(id+"F5.boolean.opBoolean","INTERSECT",EDGE,{"disambiguationData":[OD(1.0)],"derivedFrom":[makeQuery(id+"F1.opExtrude","SWEPT_FACE",FACE,{"disambiguationData":[OSD([sQuery(id+"F0.wireOp",EDGE,"E0")])]}),makeQuery(id+"F5.opExtrude","SWEPT_FACE",FACE,{"disambiguationData":[OSD([sQuery(id+"F4.wireOp",EDGE,"E51")])]})]});
            var Q140;
            Q140=makeQuery(id+"F5.boolean.opBoolean","INTERSECT",EDGE,{"disambiguationData":[OD(1.0)],"derivedFrom":[makeQuery(id+"F1.opExtrude","SWEPT_FACE",FACE,{"disambiguationData":[OSD([sQuery(id+"F0.wireOp",EDGE,"E0")])]}),makeQuery(id+"F5.opExtrude","SWEPT_FACE",FACE,{"disambiguationData":[OSD([sQuery(id+"F4.wireOp",EDGE,"E50")])]})]});
            var Q141;
            Q141=makeQuery(id+"F5.boolean.opBoolean","INTERSECT",EDGE,{"disambiguationData":[OD(1.0)],"derivedFrom":[makeQuery(id+"F1.opExtrude","SWEPT_FACE",FACE,{"disambiguationData":[OSD([sQuery(id+"F0.wireOp",EDGE,"E0")])]}),makeQuery(id+"F5.opExtrude","SWEPT_FACE",FACE,{"disambiguationData":[OSD([sQuery(id+"F4.wireOp",EDGE,"E32")])]})]});
            var Q142;
            Q142=makeQuery(id+"F5.boolean.opBoolean","INTERSECT",EDGE,{"disambiguationData":[OD(1.0)],"derivedFrom":[makeQuery(id+"F1.opExtrude","SWEPT_FACE",FACE,{"disambiguationData":[OSD([sQuery(id+"F0.wireOp",EDGE,"E0")])]}),makeQuery(id+"F5.opExtrude","SWEPT_FACE",FACE,{"disambiguationData":[OSD([sQuery(id+"F4.wireOp",EDGE,"E37")])]})]});
            var Q143;
            Q143=makeQuery(id+"F5.boolean.opBoolean","INTERSECT",EDGE,{"disambiguationData":[OD(1.0)],"derivedFrom":[makeQuery(id+"F1.opExtrude","SWEPT_FACE",FACE,{"disambiguationData":[OSD([sQuery(id+"F0.wireOp",EDGE,"E0")])]}),makeQuery(id+"F5.opExtrude","SWEPT_FACE",FACE,{"disambiguationData":[OSD([sQuery(id+"F4.wireOp",EDGE,"E36")])]})]});
            var Q144;
            Q144=makeQuery(id+"F5.boolean.opBoolean","INTERSECT",EDGE,{"disambiguationData":[OD(1.0)],"derivedFrom":[makeQuery(id+"F1.opExtrude","SWEPT_FACE",FACE,{"disambiguationData":[OSD([sQuery(id+"F0.wireOp",EDGE,"E0")])]}),makeQuery(id+"F5.opExtrude","SWEPT_FACE",FACE,{"disambiguationData":[OSD([sQuery(id+"F4.wireOp",EDGE,"E35")])]})]});
            var Q145;
            Q145=makeQuery(id+"F5.boolean.opBoolean","INTERSECT",EDGE,{"disambiguationData":[OD(1.0)],"derivedFrom":[makeQuery(id+"F1.opExtrude","SWEPT_FACE",FACE,{"disambiguationData":[OSD([sQuery(id+"F0.wireOp",EDGE,"E0")])]}),makeQuery(id+"F5.opExtrude","SWEPT_FACE",FACE,{"disambiguationData":[OSD([sQuery(id+"F4.wireOp",EDGE,"E34")])]})]});
            var Q146;
            Q146=makeQuery(id+"F5.boolean.opBoolean","INTERSECT",EDGE,{"disambiguationData":[OD(1.0)],"derivedFrom":[makeQuery(id+"F1.opExtrude","SWEPT_FACE",FACE,{"disambiguationData":[OSD([sQuery(id+"F0.wireOp",EDGE,"E0")])]}),makeQuery(id+"F5.opExtrude","SWEPT_FACE",FACE,{"disambiguationData":[OSD([sQuery(id+"F4.wireOp",EDGE,"E33")])]})]});
            var Q147;
            Q147=makeQuery(id+"F5.boolean.opBoolean","INTERSECT",EDGE,{"disambiguationData":[OD(1.0)],"derivedFrom":[makeQuery(id+"F1.opExtrude","SWEPT_FACE",FACE,{"disambiguationData":[OSD([sQuery(id+"F0.wireOp",EDGE,"E0")])]}),makeQuery(id+"F5.opExtrude","SWEPT_FACE",FACE,{"disambiguationData":[OSD([sQuery(id+"F4.wireOp",EDGE,"b579cf08-57c8-4be4-a64a-6a7c8f7f1ba5")])]})]});
            fillet(context, id + "F15", {"entities" : qUnion([Q0, Q1, Q2, Q3, Q4, Q5, Q6, Q7, Q8, Q9, Q10, Q11, Q12, Q13, Q14, Q15, Q16, Q17, Q18, Q19, Q20, Q21, Q22, Q23, Q24, Q25, Q26, Q27, Q28, Q29, Q30, Q31, Q32, Q33, Q34, Q35, Q36, Q37, Q38, Q39, Q40, Q41, Q42, Q43, Q44, Q45, Q46, Q47, Q48, Q49, Q50, Q51, Q52, Q53, Q54, Q55, Q56, Q57, Q58, Q59, Q60, Q61, Q62, Q63, Q64, Q65, Q66, Q67, Q68, Q69, Q70, Q71, Q72, Q73, Q74, Q75, Q76, Q77, Q78, Q79, Q80, Q81, Q82, Q83, Q84, Q85, Q86, Q87, Q88, Q89, Q90, Q91, Q92, Q93, Q94, Q95, Q96, Q97, Q98, Q99, Q100, Q101, Q102, Q103, Q104, Q105, Q106, Q107, Q108, Q109, Q110, Q111, Q112, Q113, Q114, Q115, Q116, Q117, Q118, Q119, Q120, Q121, Q122, Q123, Q124, Q125, Q126, Q127, Q128, Q129, Q130, Q131, Q132, Q133, Q134, Q135, Q136, Q137, Q138, Q139, Q140, Q141, Q142, Q143, Q144, Q145, Q146, Q147]), "radius" : 0.4 * mm, "tangentPropagation" : true, "allowEdgeOverflow" : false});
        }
        {
            var Q0;
            Q0=makeQuery(id+"F10.boolean.opBoolean","INTERSECT",EDGE,{"disambiguationData":[OD(1.0)],"derivedFrom":[makeQuery(id+"F1.opExtrude","SWEPT_FACE",FACE,{"disambiguationData":[OSD([sQuery(id+"F0.wireOp",EDGE,"E0")])]}),makeQuery(id+"F10.opExtrude","SWEPT_FACE",FACE,{"disambiguationData":[OSD([sQuery(id+"F9.wireOp",EDGE,"E325")])]})]});
            var Q1;
            Q1=makeQuery(id+"F10.boolean.opBoolean","INTERSECT",EDGE,{"disambiguationData":[OD(1.0)],"derivedFrom":[makeQuery(id+"F1.opExtrude","SWEPT_FACE",FACE,{"disambiguationData":[OSD([sQuery(id+"F0.wireOp",EDGE,"E0")])]}),makeQuery(id+"F10.opExtrude","SWEPT_FACE",FACE,{"disambiguationData":[OSD([sQuery(id+"F9.wireOp",EDGE,"E324")])]})]});
            var Q2;
            Q2=makeQuery(id+"F10.boolean.opBoolean","INTERSECT",EDGE,{"disambiguationData":[OD(1.0)],"derivedFrom":[makeQuery(id+"F1.opExtrude","SWEPT_FACE",FACE,{"disambiguationData":[OSD([sQuery(id+"F0.wireOp",EDGE,"E0")])]}),makeQuery(id+"F10.opExtrude","SWEPT_FACE",FACE,{"disambiguationData":[OSD([sQuery(id+"F9.wireOp",EDGE,"E323")])]})]});
            var Q3;
            Q3=makeQuery(id+"F10.boolean.opBoolean","INTERSECT",EDGE,{"disambiguationData":[OD(1.0)],"derivedFrom":[makeQuery(id+"F1.opExtrude","SWEPT_FACE",FACE,{"disambiguationData":[OSD([sQuery(id+"F0.wireOp",EDGE,"E0")])]}),makeQuery(id+"F10.opExtrude","SWEPT_FACE",FACE,{"disambiguationData":[OSD([sQuery(id+"F9.wireOp",EDGE,"E308")])]})]});
            var Q4;
            Q4=makeQuery(id+"F10.boolean.opBoolean","INTERSECT",EDGE,{"disambiguationData":[OD(1.0)],"derivedFrom":[makeQuery(id+"F1.opExtrude","SWEPT_FACE",FACE,{"disambiguationData":[OSD([sQuery(id+"F0.wireOp",EDGE,"E0")])]}),makeQuery(id+"F10.opExtrude","SWEPT_FACE",FACE,{"disambiguationData":[OSD([sQuery(id+"F9.wireOp",EDGE,"E303")])]})]});
            var Q5;
            Q5=makeQuery(id+"F10.boolean.opBoolean","INTERSECT",EDGE,{"disambiguationData":[OD(1.0)],"derivedFrom":[makeQuery(id+"F1.opExtrude","SWEPT_FACE",FACE,{"disambiguationData":[OSD([sQuery(id+"F0.wireOp",EDGE,"E0")])]}),makeQuery(id+"F10.opExtrude","SWEPT_FACE",FACE,{"disambiguationData":[OSD([sQuery(id+"F9.wireOp",EDGE,"E307")])]})]});
            var Q6;
            Q6=makeQuery(id+"F10.boolean.opBoolean","INTERSECT",EDGE,{"disambiguationData":[OD(1.0)],"derivedFrom":[makeQuery(id+"F1.opExtrude","SWEPT_FACE",FACE,{"disambiguationData":[OSD([sQuery(id+"F0.wireOp",EDGE,"E0")])]}),makeQuery(id+"F10.opExtrude","SWEPT_FACE",FACE,{"disambiguationData":[OSD([sQuery(id+"F9.wireOp",EDGE,"E306")])]})]});
            var Q7;
            Q7=makeQuery(id+"F10.boolean.opBoolean","INTERSECT",EDGE,{"disambiguationData":[OD(1.0)],"derivedFrom":[makeQuery(id+"F1.opExtrude","SWEPT_FACE",FACE,{"disambiguationData":[OSD([sQuery(id+"F0.wireOp",EDGE,"E0")])]}),makeQuery(id+"F10.opExtrude","SWEPT_FACE",FACE,{"disambiguationData":[OSD([sQuery(id+"F9.wireOp",EDGE,"E304")])]})]});
            var Q8;
            Q8=makeQuery(id+"F10.boolean.opBoolean","INTERSECT",EDGE,{"disambiguationData":[OD(1.0)],"derivedFrom":[makeQuery(id+"F1.opExtrude","SWEPT_FACE",FACE,{"disambiguationData":[OSD([sQuery(id+"F0.wireOp",EDGE,"E0")])]}),makeQuery(id+"F10.opExtrude","SWEPT_FACE",FACE,{"disambiguationData":[OSD([sQuery(id+"F9.wireOp",EDGE,"E305")])]})]});
            var Q9;
            Q9=makeQuery(id+"F10.boolean.opBoolean","INTERSECT",EDGE,{"disambiguationData":[OD(1.0)],"derivedFrom":[makeQuery(id+"F1.opExtrude","SWEPT_FACE",FACE,{"disambiguationData":[OSD([sQuery(id+"F0.wireOp",EDGE,"E0")])]}),makeQuery(id+"F10.opExtrude","SWEPT_FACE",FACE,{"disambiguationData":[OSD([sQuery(id+"F9.wireOp",EDGE,"E290")])]})]});
            var Q10;
            Q10=makeQuery(id+"F10.boolean.opBoolean","INTERSECT",EDGE,{"disambiguationData":[OD(1.0)],"derivedFrom":[makeQuery(id+"F1.opExtrude","SWEPT_FACE",FACE,{"disambiguationData":[OSD([sQuery(id+"F0.wireOp",EDGE,"E0")])]}),makeQuery(id+"F10.opExtrude","SWEPT_FACE",FACE,{"disambiguationData":[OSD([sQuery(id+"F9.wireOp",EDGE,"E420")])]})]});
            var Q11;
            Q11=makeQuery(id+"F10.boolean.opBoolean","INTERSECT",EDGE,{"disambiguationData":[OD(1.0)],"derivedFrom":[makeQuery(id+"F1.opExtrude","SWEPT_FACE",FACE,{"disambiguationData":[OSD([sQuery(id+"F0.wireOp",EDGE,"E0")])]}),makeQuery(id+"F10.opExtrude","SWEPT_FACE",FACE,{"disambiguationData":[OSD([sQuery(id+"F9.wireOp",EDGE,"E418"),sQuery(id+"F9.wireOp",EDGE,"E419")])]})]});
            var Q12;
            Q12=makeQuery(id+"F10.boolean.opBoolean","INTERSECT",EDGE,{"disambiguationData":[OD(1.0)],"derivedFrom":[makeQuery(id+"F1.opExtrude","SWEPT_FACE",FACE,{"disambiguationData":[OSD([sQuery(id+"F0.wireOp",EDGE,"E0")])]}),makeQuery(id+"F10.opExtrude","SWEPT_FACE",FACE,{"disambiguationData":[OSD([sQuery(id+"F9.wireOp",EDGE,"E421")])]})]});
            var Q13;
            Q13=makeQuery(id+"F7.boolean.opBoolean","INTERSECT",EDGE,{"disambiguationData":[OD(1.0)],"derivedFrom":[makeQuery(id+"F1.opExtrude","SWEPT_FACE",FACE,{"disambiguationData":[OSD([sQuery(id+"F0.wireOp",EDGE,"E0")])]}),makeQuery(id+"F7.opExtrude","SWEPT_FACE",FACE,{"disambiguationData":[OSD([sQuery(id+"F6.wireOp",EDGE,"E157")])]})]});
            var Q14;
            Q14=makeQuery(id+"F7.boolean.opBoolean","INTERSECT",EDGE,{"disambiguationData":[OD(1.0)],"derivedFrom":[makeQuery(id+"F1.opExtrude","SWEPT_FACE",FACE,{"disambiguationData":[OSD([sQuery(id+"F0.wireOp",EDGE,"E0")])]}),makeQuery(id+"F7.opExtrude","SWEPT_FACE",FACE,{"disambiguationData":[OSD([sQuery(id+"F6.wireOp",EDGE,"E156")])]})]});
            var Q15;
            Q15=makeQuery(id+"F7.boolean.opBoolean","INTERSECT",EDGE,{"disambiguationData":[OD(1.0)],"derivedFrom":[makeQuery(id+"F1.opExtrude","SWEPT_FACE",FACE,{"disambiguationData":[OSD([sQuery(id+"F0.wireOp",EDGE,"E0")])]}),makeQuery(id+"F7.opExtrude","SWEPT_FACE",FACE,{"disambiguationData":[OSD([sQuery(id+"F6.wireOp",EDGE,"E155")])]})]});
            var Q16;
            Q16=makeQuery(id+"F7.boolean.opBoolean","INTERSECT",EDGE,{"disambiguationData":[OD(1.0)],"derivedFrom":[makeQuery(id+"F1.opExtrude","SWEPT_FACE",FACE,{"disambiguationData":[OSD([sQuery(id+"F0.wireOp",EDGE,"E0")])]}),makeQuery(id+"F7.opExtrude","SWEPT_FACE",FACE,{"disambiguationData":[OSD([sQuery(id+"F6.wireOp",EDGE,"E160")])]})]});
            var Q17;
            Q17=makeQuery(id+"F7.boolean.opBoolean","INTERSECT",EDGE,{"disambiguationData":[OD(1.0)],"derivedFrom":[makeQuery(id+"F1.opExtrude","SWEPT_FACE",FACE,{"disambiguationData":[OSD([sQuery(id+"F0.wireOp",EDGE,"E0")])]}),makeQuery(id+"F7.opExtrude","SWEPT_FACE",FACE,{"disambiguationData":[OSD([sQuery(id+"F6.wireOp",EDGE,"E159")])]})]});
            var Q18;
            Q18=makeQuery(id+"F7.boolean.opBoolean","INTERSECT",EDGE,{"disambiguationData":[OD(1.0)],"derivedFrom":[makeQuery(id+"F1.opExtrude","SWEPT_FACE",FACE,{"disambiguationData":[OSD([sQuery(id+"F0.wireOp",EDGE,"E0")])]}),makeQuery(id+"F7.opExtrude","SWEPT_FACE",FACE,{"disambiguationData":[OSD([sQuery(id+"F6.wireOp",EDGE,"E175")])]})]});
            var Q19;
            Q19=makeQuery(id+"F7.boolean.opBoolean","INTERSECT",EDGE,{"disambiguationData":[OD(1.0)],"derivedFrom":[makeQuery(id+"F1.opExtrude","SWEPT_FACE",FACE,{"disambiguationData":[OSD([sQuery(id+"F0.wireOp",EDGE,"E0")])]}),makeQuery(id+"F7.opExtrude","SWEPT_FACE",FACE,{"disambiguationData":[OSD([sQuery(id+"F6.wireOp",EDGE,"E176")])]})]});
            var Q20;
            Q20=makeQuery(id+"F7.boolean.opBoolean","INTERSECT",EDGE,{"disambiguationData":[OD(1.0)],"derivedFrom":[makeQuery(id+"F1.opExtrude","SWEPT_FACE",FACE,{"disambiguationData":[OSD([sQuery(id+"F0.wireOp",EDGE,"E0")])]}),makeQuery(id+"F7.opExtrude","SWEPT_FACE",FACE,{"disambiguationData":[OSD([sQuery(id+"F6.wireOp",EDGE,"E174")])]})]});
            var Q21;
            Q21=makeQuery(id+"F7.boolean.opBoolean","INTERSECT",EDGE,{"disambiguationData":[OD(1.0)],"derivedFrom":[makeQuery(id+"F1.opExtrude","SWEPT_FACE",FACE,{"disambiguationData":[OSD([sQuery(id+"F0.wireOp",EDGE,"E0")])]}),makeQuery(id+"F7.opExtrude","SWEPT_FACE",FACE,{"disambiguationData":[OSD([sQuery(id+"F6.wireOp",EDGE,"E173")])]})]});
            var Q22;
            Q22=makeQuery(id+"F7.boolean.opBoolean","INTERSECT",EDGE,{"disambiguationData":[OD(1.0)],"derivedFrom":[makeQuery(id+"F1.opExtrude","SWEPT_FACE",FACE,{"disambiguationData":[OSD([sQuery(id+"F0.wireOp",EDGE,"E0")])]}),makeQuery(id+"F7.opExtrude","SWEPT_FACE",FACE,{"disambiguationData":[OSD([sQuery(id+"F6.wireOp",EDGE,"E177")])]})]});
            var Q23;
            Q23=makeQuery(id+"F7.boolean.opBoolean","INTERSECT",EDGE,{"disambiguationData":[OD(1.0)],"derivedFrom":[makeQuery(id+"F1.opExtrude","SWEPT_FACE",FACE,{"disambiguationData":[OSD([sQuery(id+"F0.wireOp",EDGE,"E0")])]}),makeQuery(id+"F7.opExtrude","SWEPT_FACE",FACE,{"disambiguationData":[OSD([sQuery(id+"F6.wireOp",EDGE,"E178")])]})]});
            var Q24;
            Q24=makeQuery(id+"F7.boolean.opBoolean","INTERSECT",EDGE,{"disambiguationData":[OD(1.0)],"derivedFrom":[makeQuery(id+"F1.opExtrude","SWEPT_FACE",FACE,{"disambiguationData":[OSD([sQuery(id+"F0.wireOp",EDGE,"E0")])]}),makeQuery(id+"F7.opExtrude","SWEPT_FACE",FACE,{"disambiguationData":[OSD([sQuery(id+"F6.wireOp",EDGE,"E196")])]})]});
            var Q25;
            Q25=makeQuery(id+"F7.boolean.opBoolean","INTERSECT",EDGE,{"disambiguationData":[OD(1.0)],"derivedFrom":[makeQuery(id+"F1.opExtrude","SWEPT_FACE",FACE,{"disambiguationData":[OSD([sQuery(id+"F0.wireOp",EDGE,"E0")])]}),makeQuery(id+"F7.opExtrude","SWEPT_FACE",FACE,{"disambiguationData":[OSD([sQuery(id+"F6.wireOp",EDGE,"E191")])]})]});
            var Q26;
            Q26=makeQuery(id+"F7.boolean.opBoolean","INTERSECT",EDGE,{"disambiguationData":[OD(1.0)],"derivedFrom":[makeQuery(id+"F1.opExtrude","SWEPT_FACE",FACE,{"disambiguationData":[OSD([sQuery(id+"F0.wireOp",EDGE,"E0")])]}),makeQuery(id+"F7.opExtrude","SWEPT_FACE",FACE,{"disambiguationData":[OSD([sQuery(id+"F6.wireOp",EDGE,"E192")])]})]});
            var Q27;
            Q27=makeQuery(id+"F7.boolean.opBoolean","INTERSECT",EDGE,{"disambiguationData":[OD(1.0)],"derivedFrom":[makeQuery(id+"F1.opExtrude","SWEPT_FACE",FACE,{"disambiguationData":[OSD([sQuery(id+"F0.wireOp",EDGE,"E0")])]}),makeQuery(id+"F7.opExtrude","SWEPT_FACE",FACE,{"disambiguationData":[OSD([sQuery(id+"F6.wireOp",EDGE,"E193")])]})]});
            var Q28;
            Q28=makeQuery(id+"F7.boolean.opBoolean","INTERSECT",EDGE,{"disambiguationData":[OD(1.0)],"derivedFrom":[makeQuery(id+"F1.opExtrude","SWEPT_FACE",FACE,{"disambiguationData":[OSD([sQuery(id+"F0.wireOp",EDGE,"E0")])]}),makeQuery(id+"F7.opExtrude","SWEPT_FACE",FACE,{"disambiguationData":[OSD([sQuery(id+"F6.wireOp",EDGE,"E194")])]})]});
            var Q29;
            Q29=makeQuery(id+"F7.boolean.opBoolean","INTERSECT",EDGE,{"disambiguationData":[OD(1.0)],"derivedFrom":[makeQuery(id+"F1.opExtrude","SWEPT_FACE",FACE,{"disambiguationData":[OSD([sQuery(id+"F0.wireOp",EDGE,"E0")])]}),makeQuery(id+"F7.opExtrude","SWEPT_FACE",FACE,{"disambiguationData":[OSD([sQuery(id+"F6.wireOp",EDGE,"E195")])]})]});
            var Q30;
            Q30=makeQuery(id+"F7.boolean.opBoolean","INTERSECT",EDGE,{"disambiguationData":[OD(1.0)],"derivedFrom":[makeQuery(id+"F1.opExtrude","SWEPT_FACE",FACE,{"disambiguationData":[OSD([sQuery(id+"F0.wireOp",EDGE,"E0")])]}),makeQuery(id+"F7.opExtrude","SWEPT_FACE",FACE,{"disambiguationData":[OSD([sQuery(id+"F6.wireOp",EDGE,"E212")])]})]});
            var Q31;
            Q31=makeQuery(id+"F7.boolean.opBoolean","INTERSECT",EDGE,{"disambiguationData":[OD(1.0)],"derivedFrom":[makeQuery(id+"F1.opExtrude","SWEPT_FACE",FACE,{"disambiguationData":[OSD([sQuery(id+"F0.wireOp",EDGE,"E0")])]}),makeQuery(id+"F7.opExtrude","SWEPT_FACE",FACE,{"disambiguationData":[OSD([sQuery(id+"F6.wireOp",EDGE,"E213")])]})]});
            var Q32;
            Q32=makeQuery(id+"F7.boolean.opBoolean","INTERSECT",EDGE,{"disambiguationData":[OD(1.0)],"derivedFrom":[makeQuery(id+"F1.opExtrude","SWEPT_FACE",FACE,{"disambiguationData":[OSD([sQuery(id+"F0.wireOp",EDGE,"E0")])]}),makeQuery(id+"F7.opExtrude","SWEPT_FACE",FACE,{"disambiguationData":[OSD([sQuery(id+"F6.wireOp",EDGE,"E214")])]})]});
            var Q33;
            Q33=makeQuery(id+"F7.boolean.opBoolean","INTERSECT",EDGE,{"disambiguationData":[OD(1.0)],"derivedFrom":[makeQuery(id+"F1.opExtrude","SWEPT_FACE",FACE,{"disambiguationData":[OSD([sQuery(id+"F0.wireOp",EDGE,"E0")])]}),makeQuery(id+"F7.opExtrude","SWEPT_FACE",FACE,{"disambiguationData":[OSD([sQuery(id+"F6.wireOp",EDGE,"E209")])]})]});
            var Q34;
            Q34=makeQuery(id+"F7.boolean.opBoolean","INTERSECT",EDGE,{"disambiguationData":[OD(1.0)],"derivedFrom":[makeQuery(id+"F1.opExtrude","SWEPT_FACE",FACE,{"disambiguationData":[OSD([sQuery(id+"F0.wireOp",EDGE,"E0")])]}),makeQuery(id+"F7.opExtrude","SWEPT_FACE",FACE,{"disambiguationData":[OSD([sQuery(id+"F6.wireOp",EDGE,"E210")])]})]});
            var Q35;
            Q35=makeQuery(id+"F7.boolean.opBoolean","INTERSECT",EDGE,{"disambiguationData":[OD(1.0)],"derivedFrom":[makeQuery(id+"F1.opExtrude","SWEPT_FACE",FACE,{"disambiguationData":[OSD([sQuery(id+"F0.wireOp",EDGE,"E0")])]}),makeQuery(id+"F7.opExtrude","SWEPT_FACE",FACE,{"disambiguationData":[OSD([sQuery(id+"F6.wireOp",EDGE,"E211")])]})]});
            var Q36;
            Q36=makeQuery(id+"F7.boolean.opBoolean","INTERSECT",EDGE,{"disambiguationData":[OD(1.0)],"derivedFrom":[makeQuery(id+"F1.opExtrude","SWEPT_FACE",FACE,{"disambiguationData":[OSD([sQuery(id+"F0.wireOp",EDGE,"E0")])]}),makeQuery(id+"F7.opExtrude","SWEPT_FACE",FACE,{"disambiguationData":[OSD([sQuery(id+"F6.wireOp",EDGE,"E232")])]})]});
            var Q37;
            Q37=makeQuery(id+"F7.boolean.opBoolean","INTERSECT",EDGE,{"disambiguationData":[OD(1.0)],"derivedFrom":[makeQuery(id+"F1.opExtrude","SWEPT_FACE",FACE,{"disambiguationData":[OSD([sQuery(id+"F0.wireOp",EDGE,"E0")])]}),makeQuery(id+"F7.opExtrude","SWEPT_FACE",FACE,{"disambiguationData":[OSD([sQuery(id+"F6.wireOp",EDGE,"E231")])]})]});
            var Q38;
            Q38=makeQuery(id+"F7.boolean.opBoolean","INTERSECT",EDGE,{"disambiguationData":[OD(1.0)],"derivedFrom":[makeQuery(id+"F1.opExtrude","SWEPT_FACE",FACE,{"disambiguationData":[OSD([sQuery(id+"F0.wireOp",EDGE,"E0")])]}),makeQuery(id+"F7.opExtrude","SWEPT_FACE",FACE,{"disambiguationData":[OSD([sQuery(id+"F6.wireOp",EDGE,"E230")])]})]});
            var Q39;
            Q39=makeQuery(id+"F7.boolean.opBoolean","INTERSECT",EDGE,{"disambiguationData":[OD(1.0)],"derivedFrom":[makeQuery(id+"F1.opExtrude","SWEPT_FACE",FACE,{"disambiguationData":[OSD([sQuery(id+"F0.wireOp",EDGE,"E0")])]}),makeQuery(id+"F7.opExtrude","SWEPT_FACE",FACE,{"disambiguationData":[OSD([sQuery(id+"F6.wireOp",EDGE,"E229")])]})]});
            var Q40;
            Q40=makeQuery(id+"F7.boolean.opBoolean","INTERSECT",EDGE,{"disambiguationData":[OD(1.0)],"derivedFrom":[makeQuery(id+"F1.opExtrude","SWEPT_FACE",FACE,{"disambiguationData":[OSD([sQuery(id+"F0.wireOp",EDGE,"E0")])]}),makeQuery(id+"F7.opExtrude","SWEPT_FACE",FACE,{"disambiguationData":[OSD([sQuery(id+"F6.wireOp",EDGE,"E228")])]})]});
            var Q41;
            Q41=makeQuery(id+"F7.boolean.opBoolean","INTERSECT",EDGE,{"disambiguationData":[OD(1.0)],"derivedFrom":[makeQuery(id+"F1.opExtrude","SWEPT_FACE",FACE,{"disambiguationData":[OSD([sQuery(id+"F0.wireOp",EDGE,"E0")])]}),makeQuery(id+"F7.opExtrude","SWEPT_FACE",FACE,{"disambiguationData":[OSD([sQuery(id+"F6.wireOp",EDGE,"E227")])]})]});
            var Q42;
            Q42=makeQuery(id+"F7.boolean.opBoolean","INTERSECT",EDGE,{"disambiguationData":[OD(1.0)],"derivedFrom":[makeQuery(id+"F1.opExtrude","SWEPT_FACE",FACE,{"disambiguationData":[OSD([sQuery(id+"F0.wireOp",EDGE,"E0")])]}),makeQuery(id+"F7.opExtrude","SWEPT_FACE",FACE,{"disambiguationData":[OSD([sQuery(id+"F6.wireOp",EDGE,"E250")])]})]});
            var Q43;
            Q43=makeQuery(id+"F7.boolean.opBoolean","INTERSECT",EDGE,{"disambiguationData":[OD(1.0)],"derivedFrom":[makeQuery(id+"F1.opExtrude","SWEPT_FACE",FACE,{"disambiguationData":[OSD([sQuery(id+"F0.wireOp",EDGE,"E0")])]}),makeQuery(id+"F7.opExtrude","SWEPT_FACE",FACE,{"disambiguationData":[OSD([sQuery(id+"F6.wireOp",EDGE,"E245")])]})]});
            var Q44;
            Q44=makeQuery(id+"F7.boolean.opBoolean","INTERSECT",EDGE,{"disambiguationData":[OD(1.0)],"derivedFrom":[makeQuery(id+"F1.opExtrude","SWEPT_FACE",FACE,{"disambiguationData":[OSD([sQuery(id+"F0.wireOp",EDGE,"E0")])]}),makeQuery(id+"F7.opExtrude","SWEPT_FACE",FACE,{"disambiguationData":[OSD([sQuery(id+"F6.wireOp",EDGE,"E246")])]})]});
            var Q45;
            Q45=makeQuery(id+"F7.boolean.opBoolean","INTERSECT",EDGE,{"disambiguationData":[OD(1.0)],"derivedFrom":[makeQuery(id+"F1.opExtrude","SWEPT_FACE",FACE,{"disambiguationData":[OSD([sQuery(id+"F0.wireOp",EDGE,"E0")])]}),makeQuery(id+"F7.opExtrude","SWEPT_FACE",FACE,{"disambiguationData":[OSD([sQuery(id+"F6.wireOp",EDGE,"E247")])]})]});
            var Q46;
            Q46=makeQuery(id+"F7.boolean.opBoolean","INTERSECT",EDGE,{"disambiguationData":[OD(1.0)],"derivedFrom":[makeQuery(id+"F1.opExtrude","SWEPT_FACE",FACE,{"disambiguationData":[OSD([sQuery(id+"F0.wireOp",EDGE,"E0")])]}),makeQuery(id+"F7.opExtrude","SWEPT_FACE",FACE,{"disambiguationData":[OSD([sQuery(id+"F6.wireOp",EDGE,"E248")])]})]});
            var Q47;
            Q47=makeQuery(id+"F7.boolean.opBoolean","INTERSECT",EDGE,{"disambiguationData":[OD(1.0)],"derivedFrom":[makeQuery(id+"F1.opExtrude","SWEPT_FACE",FACE,{"disambiguationData":[OSD([sQuery(id+"F0.wireOp",EDGE,"E0")])]}),makeQuery(id+"F7.opExtrude","SWEPT_FACE",FACE,{"disambiguationData":[OSD([sQuery(id+"F6.wireOp",EDGE,"E249")])]})]});
            var Q48;
            Q48=makeQuery(id+"F7.boolean.opBoolean","INTERSECT",EDGE,{"disambiguationData":[OD(1.0)],"derivedFrom":[makeQuery(id+"F1.opExtrude","SWEPT_FACE",FACE,{"disambiguationData":[OSD([sQuery(id+"F0.wireOp",EDGE,"E0")])]}),makeQuery(id+"F7.opExtrude","SWEPT_FACE",FACE,{"disambiguationData":[OSD([sQuery(id+"F6.wireOp",EDGE,"E266")])]})]});
            var Q49;
            Q49=makeQuery(id+"F7.boolean.opBoolean","INTERSECT",EDGE,{"disambiguationData":[OD(1.0)],"derivedFrom":[makeQuery(id+"F1.opExtrude","SWEPT_FACE",FACE,{"disambiguationData":[OSD([sQuery(id+"F0.wireOp",EDGE,"E0")])]}),makeQuery(id+"F7.opExtrude","SWEPT_FACE",FACE,{"disambiguationData":[OSD([sQuery(id+"F6.wireOp",EDGE,"E267")])]})]});
            var Q50;
            Q50=makeQuery(id+"F7.boolean.opBoolean","INTERSECT",EDGE,{"disambiguationData":[OD(1.0)],"derivedFrom":[makeQuery(id+"F1.opExtrude","SWEPT_FACE",FACE,{"disambiguationData":[OSD([sQuery(id+"F0.wireOp",EDGE,"E0")])]}),makeQuery(id+"F7.opExtrude","SWEPT_FACE",FACE,{"disambiguationData":[OSD([sQuery(id+"F6.wireOp",EDGE,"E268")])]})]});
            var Q51;
            Q51=makeQuery(id+"F7.boolean.opBoolean","INTERSECT",EDGE,{"disambiguationData":[OD(1.0)],"derivedFrom":[makeQuery(id+"F1.opExtrude","SWEPT_FACE",FACE,{"disambiguationData":[OSD([sQuery(id+"F0.wireOp",EDGE,"E0")])]}),makeQuery(id+"F7.opExtrude","SWEPT_FACE",FACE,{"disambiguationData":[OSD([sQuery(id+"F6.wireOp",EDGE,"E263")])]})]});
            var Q52;
            Q52=makeQuery(id+"F7.boolean.opBoolean","INTERSECT",EDGE,{"disambiguationData":[OD(1.0)],"derivedFrom":[makeQuery(id+"F1.opExtrude","SWEPT_FACE",FACE,{"disambiguationData":[OSD([sQuery(id+"F0.wireOp",EDGE,"E0")])]}),makeQuery(id+"F7.opExtrude","SWEPT_FACE",FACE,{"disambiguationData":[OSD([sQuery(id+"F6.wireOp",EDGE,"E264")])]})]});
            var Q53;
            Q53=makeQuery(id+"F7.boolean.opBoolean","INTERSECT",EDGE,{"disambiguationData":[OD(1.0)],"derivedFrom":[makeQuery(id+"F1.opExtrude","SWEPT_FACE",FACE,{"disambiguationData":[OSD([sQuery(id+"F0.wireOp",EDGE,"E0")])]}),makeQuery(id+"F7.opExtrude","SWEPT_FACE",FACE,{"disambiguationData":[OSD([sQuery(id+"F6.wireOp",EDGE,"E265")])]})]});
            var Q54;
            Q54=makeQuery(id+"F7.boolean.opBoolean","INTERSECT",EDGE,{"disambiguationData":[OD(1.0)],"derivedFrom":[makeQuery(id+"F1.opExtrude","SWEPT_FACE",FACE,{"disambiguationData":[OSD([sQuery(id+"F0.wireOp",EDGE,"E0")])]}),makeQuery(id+"F7.opExtrude","SWEPT_FACE",FACE,{"disambiguationData":[OSD([sQuery(id+"F6.wireOp",EDGE,"E276")])]})]});
            var Q55;
            Q55=makeQuery(id+"F7.boolean.opBoolean","INTERSECT",EDGE,{"disambiguationData":[OD(1.0)],"derivedFrom":[makeQuery(id+"F1.opExtrude","SWEPT_FACE",FACE,{"disambiguationData":[OSD([sQuery(id+"F0.wireOp",EDGE,"E0")])]}),makeQuery(id+"F7.opExtrude","SWEPT_FACE",FACE,{"disambiguationData":[OSD([sQuery(id+"F6.wireOp",EDGE,"E277")])]})]});
            var Q56;
            Q56=makeQuery(id+"F7.boolean.opBoolean","INTERSECT",EDGE,{"disambiguationData":[OD(1.0)],"derivedFrom":[makeQuery(id+"F1.opExtrude","SWEPT_FACE",FACE,{"disambiguationData":[OSD([sQuery(id+"F0.wireOp",EDGE,"E0")])]}),makeQuery(id+"F7.opExtrude","SWEPT_FACE",FACE,{"disambiguationData":[OSD([sQuery(id+"F6.wireOp",EDGE,"E278")])]})]});
            var Q57;
            Q57=makeQuery(id+"F7.boolean.opBoolean","INTERSECT",EDGE,{"disambiguationData":[OD(0.0)],"derivedFrom":[makeQuery(id+"F1.opExtrude","SWEPT_FACE",FACE,{"disambiguationData":[OSD([sQuery(id+"F0.wireOp",EDGE,"E0")])]}),makeQuery(id+"F7.opExtrude","SWEPT_FACE",FACE,{"disambiguationData":[OSD([sQuery(id+"F6.wireOp",EDGE,"E283")])]})]});
            var Q58;
            Q58=makeQuery(id+"F7.boolean.opBoolean","INTERSECT",EDGE,{"disambiguationData":[OD(0.0)],"derivedFrom":[makeQuery(id+"F1.opExtrude","SWEPT_FACE",FACE,{"disambiguationData":[OSD([sQuery(id+"F0.wireOp",EDGE,"E0")])]}),makeQuery(id+"F7.opExtrude","SWEPT_FACE",FACE,{"disambiguationData":[OSD([sQuery(id+"F6.wireOp",EDGE,"E280"),sQuery(id+"F6.wireOp",EDGE,"E281")])]})]});
            var Q59;
            Q59=makeQuery(id+"F7.boolean.opBoolean","INTERSECT",EDGE,{"disambiguationData":[OD(0.0)],"derivedFrom":[makeQuery(id+"F1.opExtrude","SWEPT_FACE",FACE,{"disambiguationData":[OSD([sQuery(id+"F0.wireOp",EDGE,"E0")])]}),makeQuery(id+"F7.opExtrude","SWEPT_FACE",FACE,{"disambiguationData":[OSD([sQuery(id+"F6.wireOp",EDGE,"E282")])]})]});
            var Q60;
            Q60=makeQuery(id+"F5.boolean.opBoolean","INTERSECT",EDGE,{"disambiguationData":[OD(1.0)],"derivedFrom":[makeQuery(id+"F1.opExtrude","SWEPT_FACE",FACE,{"disambiguationData":[OSD([sQuery(id+"F0.wireOp",EDGE,"E0")])]}),makeQuery(id+"F5.opExtrude","SWEPT_FACE",FACE,{"disambiguationData":[OSD([sQuery(id+"F4.wireOp",EDGE,"E142")])]})]});
            var Q61;
            Q61=makeQuery(id+"F5.boolean.opBoolean","INTERSECT",EDGE,{"disambiguationData":[OD(1.0)],"derivedFrom":[makeQuery(id+"F1.opExtrude","SWEPT_FACE",FACE,{"disambiguationData":[OSD([sQuery(id+"F0.wireOp",EDGE,"E0")])]}),makeQuery(id+"F5.opExtrude","SWEPT_FACE",FACE,{"disambiguationData":[OSD([sQuery(id+"F4.wireOp",EDGE,"E139"),sQuery(id+"F4.wireOp",EDGE,"E140")])]})]});
            var Q62;
            Q62=makeQuery(id+"F5.boolean.opBoolean","INTERSECT",EDGE,{"disambiguationData":[OD(1.0)],"derivedFrom":[makeQuery(id+"F1.opExtrude","SWEPT_FACE",FACE,{"disambiguationData":[OSD([sQuery(id+"F0.wireOp",EDGE,"E0")])]}),makeQuery(id+"F5.opExtrude","SWEPT_FACE",FACE,{"disambiguationData":[OSD([sQuery(id+"F4.wireOp",EDGE,"E141")])]})]});
            var Q63;
            Q63=makeQuery(id+"F7.boolean.opBoolean","INTERSECT",EDGE,{"disambiguationData":[OD(1.0)],"derivedFrom":[makeQuery(id+"F1.opExtrude","SWEPT_FACE",FACE,{"disambiguationData":[OSD([sQuery(id+"F0.wireOp",EDGE,"E0")])]}),makeQuery(id+"F7.opExtrude","SWEPT_FACE",FACE,{"disambiguationData":[OSD([sQuery(id+"F6.wireOp",EDGE,"E280"),sQuery(id+"F6.wireOp",EDGE,"E281")])]})]});
            var Q64;
            Q64=makeQuery(id+"F7.boolean.opBoolean","INTERSECT",EDGE,{"disambiguationData":[OD(1.0)],"derivedFrom":[makeQuery(id+"F1.opExtrude","SWEPT_FACE",FACE,{"disambiguationData":[OSD([sQuery(id+"F0.wireOp",EDGE,"E0")])]}),makeQuery(id+"F7.opExtrude","SWEPT_FACE",FACE,{"disambiguationData":[OSD([sQuery(id+"F6.wireOp",EDGE,"E282")])]})]});
            var Q65;
            Q65=makeQuery(id+"F5.boolean.opBoolean","INTERSECT",EDGE,{"disambiguationData":[OD(0.0)],"derivedFrom":[makeQuery(id+"F1.opExtrude","SWEPT_FACE",FACE,{"disambiguationData":[OSD([sQuery(id+"F0.wireOp",EDGE,"E0")])]}),makeQuery(id+"F5.opExtrude","SWEPT_FACE",FACE,{"disambiguationData":[OSD([sQuery(id+"F4.wireOp",EDGE,"E141")])]})]});
            var Q66;
            Q66=makeQuery(id+"F5.boolean.opBoolean","INTERSECT",EDGE,{"disambiguationData":[OD(0.0)],"derivedFrom":[makeQuery(id+"F1.opExtrude","SWEPT_FACE",FACE,{"disambiguationData":[OSD([sQuery(id+"F0.wireOp",EDGE,"E0")])]}),makeQuery(id+"F5.opExtrude","SWEPT_FACE",FACE,{"disambiguationData":[OSD([sQuery(id+"F4.wireOp",EDGE,"E139"),sQuery(id+"F4.wireOp",EDGE,"E140")])]})]});
            var Q67;
            Q67=makeQuery(id+"F5.boolean.opBoolean","INTERSECT",EDGE,{"disambiguationData":[OD(0.0)],"derivedFrom":[makeQuery(id+"F1.opExtrude","SWEPT_FACE",FACE,{"disambiguationData":[OSD([sQuery(id+"F0.wireOp",EDGE,"E0")])]}),makeQuery(id+"F5.opExtrude","SWEPT_FACE",FACE,{"disambiguationData":[OSD([sQuery(id+"F4.wireOp",EDGE,"E142")])]})]});
            fillet(context, id + "F16", {"entities" : qUnion([Q0, Q1, Q2, Q3, Q4, Q5, Q6, Q7, Q8, Q9, Q10, Q11, Q12, Q13, Q14, Q15, Q16, Q17, Q18, Q19, Q20, Q21, Q22, Q23, Q24, Q25, Q26, Q27, Q28, Q29, Q30, Q31, Q32, Q33, Q34, Q35, Q36, Q37, Q38, Q39, Q40, Q41, Q42, Q43, Q44, Q45, Q46, Q47, Q48, Q49, Q50, Q51, Q52, Q53, Q54, Q55, Q56, Q57, Q58, Q59, Q60, Q61, Q62, Q63, Q64, Q65, Q66, Q67]), "radius" : 0.4 * mm, "tangentPropagation" : true, "allowEdgeOverflow" : false});
        }
    });
